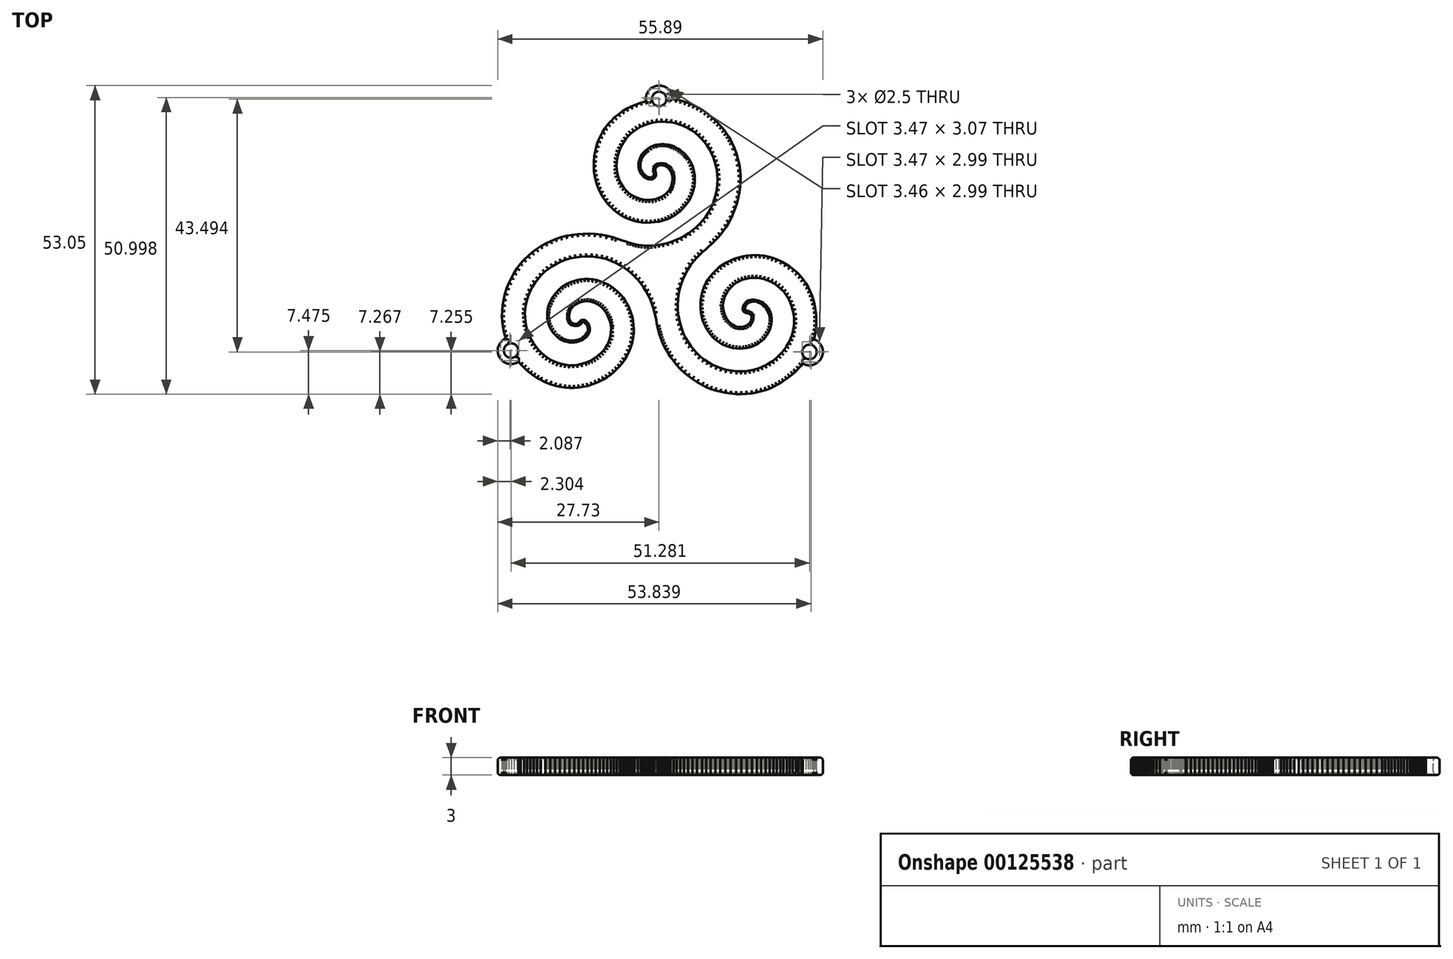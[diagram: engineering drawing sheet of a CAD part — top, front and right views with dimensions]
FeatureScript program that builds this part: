
annotation { "Feature Type Name" : "Feature", "Feature Type Description" : "" }
export const myFeature = defineFeature(function(context is Context, id is Id, definition is map)
    precondition{}
    {
        {
            var Q0;
            Q0=qCreatedBy(makeId("Top.planeOp"),FACE);
            var sketch = newSketch(context, id + "F0", { "sketchPlane" : qUnion([Q0])});
            skLineSegment(sketch, "E0", {"start": v(-0.47, 25.3) * mm, "end": v(-1.4, 25.16) * mm});
            skLineSegment(sketch, "E1", {"start": v(-1.4, 25.16) * mm, "end": v(-2.3, 24.96) * mm});
            skLineSegment(sketch, "E2", {"start": v(-2.3, 24.96) * mm, "end": v(-3.16, 24.7) * mm});
            skLineSegment(sketch, "E3", {"start": v(-3.16, 24.7) * mm, "end": v(-4, 24.4) * mm});
            skLineSegment(sketch, "E4", {"start": v(-4, 24.4) * mm, "end": v(-4.8, 24.06) * mm});
            skLineSegment(sketch, "E5", {"start": v(-4.8, 24.06) * mm, "end": v(-5.57, 23.66) * mm});
            skLineSegment(sketch, "E6", {"start": v(-5.57, 23.66) * mm, "end": v(-6.3, 23.22) * mm});
            skLineSegment(sketch, "E7", {"start": v(-6.3, 23.22) * mm, "end": v(-7, 22.73) * mm});
            skLineSegment(sketch, "E8", {"start": v(-7, 22.73) * mm, "end": v(-7.64, 22.2) * mm});
            skLineSegment(sketch, "E9", {"start": v(-7.64, 22.2) * mm, "end": v(-8.24, 21.61) * mm});
            skLineSegment(sketch, "E10", {"start": v(-8.24, 21.61) * mm, "end": v(-8.8, 20.99) * mm});
            skLineSegment(sketch, "E11", {"start": v(-8.8, 20.99) * mm, "end": v(-9.3, 20.32) * mm});
            skLineSegment(sketch, "E12", {"start": v(-9.3, 20.32) * mm, "end": v(-9.76, 19.61) * mm});
            skLineSegment(sketch, "E13", {"start": v(-9.76, 19.61) * mm, "end": v(-10.15, 18.86) * mm});
            skLineSegment(sketch, "E14", {"start": v(-10.15, 18.86) * mm, "end": v(-10.5, 18.07) * mm});
            skLineSegment(sketch, "E15", {"start": v(-10.5, 18.07) * mm, "end": v(-10.78, 17.24) * mm});
            skLineSegment(sketch, "E16", {"start": v(-10.78, 17.24) * mm, "end": v(-11, 16.37) * mm});
            skLineSegment(sketch, "E17", {"start": v(-11, 16.37) * mm, "end": v(-11.16, 15.47) * mm});
            skLineSegment(sketch, "E18", {"start": v(-11.16, 15.47) * mm, "end": v(-11.24, 14.63) * mm});
            skLineSegment(sketch, "E19", {"start": v(-11.24, 14.63) * mm, "end": v(-11.25, 13.8) * mm});
            skLineSegment(sketch, "E20", {"start": v(-11.25, 13.8) * mm, "end": v(-11.2, 12.98) * mm});
            skLineSegment(sketch, "E21", {"start": v(-11.2, 12.98) * mm, "end": v(-11.08, 12.18) * mm});
            skLineSegment(sketch, "E22", {"start": v(-11.08, 12.18) * mm, "end": v(-10.91, 11.4) * mm});
            skLineSegment(sketch, "E23", {"start": v(-10.91, 11.4) * mm, "end": v(-10.68, 10.64) * mm});
            skLineSegment(sketch, "E24", {"start": v(-10.68, 10.64) * mm, "end": v(-10.4, 9.9) * mm});
            skLineSegment(sketch, "E25", {"start": v(-10.4, 9.9) * mm, "end": v(-10.07, 9.2) * mm});
            skLineSegment(sketch, "E26", {"start": v(-10.07, 9.2) * mm, "end": v(-9.68, 8.53) * mm});
            skLineSegment(sketch, "E27", {"start": v(-9.68, 8.53) * mm, "end": v(-9.25, 7.89) * mm});
            skLineSegment(sketch, "E28", {"start": v(-9.25, 7.89) * mm, "end": v(-8.78, 7.29) * mm});
            skLineSegment(sketch, "E29", {"start": v(-8.78, 7.29) * mm, "end": v(-8.27, 6.73) * mm});
            skLineSegment(sketch, "E30", {"start": v(-8.27, 6.73) * mm, "end": v(-7.71, 6.22) * mm});
            skLineSegment(sketch, "E31", {"start": v(-7.71, 6.22) * mm, "end": v(-7.12, 5.75) * mm});
            skLineSegment(sketch, "E32", {"start": v(-7.12, 5.75) * mm, "end": v(-6.5, 5.33) * mm});
            skLineSegment(sketch, "E33", {"start": v(-6.5, 5.33) * mm, "end": v(-5.85, 4.97) * mm});
            skLineSegment(sketch, "E34", {"start": v(-5.85, 4.97) * mm, "end": v(-5.17, 4.67) * mm});
            skLineSegment(sketch, "E35", {"start": v(-5.17, 4.67) * mm, "end": v(-4.46, 4.42) * mm});
            skLineSegment(sketch, "E36", {"start": v(-4.46, 4.42) * mm, "end": v(-3.73, 4.24) * mm});
            skLineSegment(sketch, "E37", {"start": v(-3.73, 4.24) * mm, "end": v(-2.98, 4.12) * mm});
            skLineSegment(sketch, "E38", {"start": v(-2.98, 4.12) * mm, "end": v(-2.2, 4.08) * mm});
            skLineSegment(sketch, "E39", {"start": v(-2.2, 4.08) * mm, "end": v(-1.44, 4.1) * mm});
            skLineSegment(sketch, "E40", {"start": v(-1.44, 4.1) * mm, "end": v(-0.72, 4.15) * mm});
            skLineSegment(sketch, "E41", {"start": v(-0.72, 4.15) * mm, "end": v(-0.04, 4.26) * mm});
            skLineSegment(sketch, "E42", {"start": v(-0.04, 4.26) * mm, "end": v(0.6, 4.42) * mm});
            skLineSegment(sketch, "E43", {"start": v(0.6, 4.42) * mm, "end": v(1.2, 4.61) * mm});
            skLineSegment(sketch, "E44", {"start": v(1.2, 4.61) * mm, "end": v(1.75, 4.85) * mm});
            skLineSegment(sketch, "E45", {"start": v(1.75, 4.85) * mm, "end": v(2.28, 5.12) * mm});
            skLineSegment(sketch, "E46", {"start": v(2.28, 5.12) * mm, "end": v(2.77, 5.42) * mm});
            skLineSegment(sketch, "E47", {"start": v(2.77, 5.42) * mm, "end": v(3.23, 5.75) * mm});
            skLineSegment(sketch, "E48", {"start": v(3.23, 5.75) * mm, "end": v(3.66, 6.12) * mm});
            skLineSegment(sketch, "E49", {"start": v(3.66, 6.12) * mm, "end": v(4.06, 6.5) * mm});
            skLineSegment(sketch, "E50", {"start": v(4.06, 6.5) * mm, "end": v(4.43, 6.91) * mm});
            skLineSegment(sketch, "E51", {"start": v(4.43, 6.91) * mm, "end": v(4.77, 7.34) * mm});
            skLineSegment(sketch, "E52", {"start": v(4.77, 7.34) * mm, "end": v(5.13, 7.87) * mm});
            skLineSegment(sketch, "E53", {"start": v(5.13, 7.87) * mm, "end": v(5.44, 8.43) * mm});
            skLineSegment(sketch, "E54", {"start": v(5.44, 8.43) * mm, "end": v(5.7, 9.02) * mm});
            skLineSegment(sketch, "E55", {"start": v(5.7, 9.02) * mm, "end": v(5.9, 9.63) * mm});
            skLineSegment(sketch, "E56", {"start": v(5.9, 9.63) * mm, "end": v(6.03, 10.25) * mm});
            skLineSegment(sketch, "E57", {"start": v(6.03, 10.25) * mm, "end": v(6.11, 10.89) * mm});
            skLineSegment(sketch, "E58", {"start": v(6.11, 10.89) * mm, "end": v(6.14, 11.53) * mm});
            skLineSegment(sketch, "E59", {"start": v(6.14, 11.53) * mm, "end": v(6.1, 12.17) * mm});
            skLineSegment(sketch, "E60", {"start": v(6.1, 12.17) * mm, "end": v(6.01, 12.8) * mm});
            skLineSegment(sketch, "E61", {"start": v(6.01, 12.8) * mm, "end": v(5.86, 13.43) * mm});
            skLineSegment(sketch, "E62", {"start": v(5.86, 13.43) * mm, "end": v(5.64, 14.04) * mm});
            skLineSegment(sketch, "E63", {"start": v(5.64, 14.04) * mm, "end": v(5.36, 14.62) * mm});
            skLineSegment(sketch, "E64", {"start": v(5.36, 14.62) * mm, "end": v(5.02, 15.18) * mm});
            skLineSegment(sketch, "E65", {"start": v(5.02, 15.18) * mm, "end": v(4.78, 15.5) * mm});
            skLineSegment(sketch, "E66", {"start": v(4.78, 15.5) * mm, "end": v(4.5, 15.82) * mm});
            skLineSegment(sketch, "E67", {"start": v(4.5, 15.82) * mm, "end": v(4.2, 16.12) * mm});
            skLineSegment(sketch, "E68", {"start": v(4.2, 16.12) * mm, "end": v(3.85, 16.4) * mm});
            skLineSegment(sketch, "E69", {"start": v(3.85, 16.4) * mm, "end": v(3.48, 16.67) * mm});
            skLineSegment(sketch, "E70", {"start": v(3.48, 16.67) * mm, "end": v(3.09, 16.9) * mm});
            skLineSegment(sketch, "E71", {"start": v(3.09, 16.9) * mm, "end": v(2.67, 17.12) * mm});
            skLineSegment(sketch, "E72", {"start": v(2.67, 17.12) * mm, "end": v(2.23, 17.3) * mm});
            skLineSegment(sketch, "E73", {"start": v(2.23, 17.3) * mm, "end": v(1.78, 17.44) * mm});
            skLineSegment(sketch, "E74", {"start": v(1.78, 17.44) * mm, "end": v(1.31, 17.54) * mm});
            skLineSegment(sketch, "E75", {"start": v(1.31, 17.54) * mm, "end": v(0.83, 17.6) * mm});
            skLineSegment(sketch, "E76", {"start": v(0.83, 17.6) * mm, "end": v(0.35, 17.6) * mm});
            skLineSegment(sketch, "E77", {"start": v(0.35, 17.6) * mm, "end": v(-0.14, 17.55) * mm});
            skLineSegment(sketch, "E78", {"start": v(-0.14, 17.55) * mm, "end": v(-0.63, 17.44) * mm});
            skLineSegment(sketch, "E79", {"start": v(-0.63, 17.44) * mm, "end": v(-1.12, 17.26) * mm});
            skLineSegment(sketch, "E80", {"start": v(-1.12, 17.26) * mm, "end": v(-1.6, 17.02) * mm});
            skLineSegment(sketch, "E81", {"start": v(-1.6, 17.02) * mm, "end": v(-2.09, 16.7) * mm});
            skLineSegment(sketch, "E82", {"start": v(-2.09, 16.7) * mm, "end": v(-2.3, 16.53) * mm});
            skLineSegment(sketch, "E83", {"start": v(-2.3, 16.53) * mm, "end": v(-2.53, 16.31) * mm});
            skLineSegment(sketch, "E84", {"start": v(-2.53, 16.31) * mm, "end": v(-2.75, 16.07) * mm});
            skLineSegment(sketch, "E85", {"start": v(-2.75, 16.07) * mm, "end": v(-2.96, 15.79) * mm});
            skLineSegment(sketch, "E86", {"start": v(-2.96, 15.79) * mm, "end": v(-3.15, 15.48) * mm});
            skLineSegment(sketch, "E87", {"start": v(-3.15, 15.48) * mm, "end": v(-3.3, 15.14) * mm});
            skLineSegment(sketch, "E88", {"start": v(-3.3, 15.14) * mm, "end": v(-3.44, 14.79) * mm});
            skLineSegment(sketch, "E89", {"start": v(-3.44, 14.79) * mm, "end": v(-3.52, 14.4) * mm});
            skLineSegment(sketch, "E90", {"start": v(-3.52, 14.4) * mm, "end": v(-3.56, 14.01) * mm});
            skLineSegment(sketch, "E91", {"start": v(-3.56, 14.01) * mm, "end": v(-3.54, 13.6) * mm});
            skLineSegment(sketch, "E92", {"start": v(-3.54, 13.6) * mm, "end": v(-3.45, 13.17) * mm});
            skLineSegment(sketch, "E93", {"start": v(-3.45, 13.17) * mm, "end": v(-3.32, 12.8) * mm});
            skLineSegment(sketch, "E94", {"start": v(-3.32, 12.8) * mm, "end": v(-3.14, 12.5) * mm});
            skLineSegment(sketch, "E95", {"start": v(-3.14, 12.5) * mm, "end": v(-2.93, 12.22) * mm});
            skLineSegment(sketch, "E96", {"start": v(-2.93, 12.22) * mm, "end": v(-2.69, 11.99) * mm});
            skLineSegment(sketch, "E97", {"start": v(-2.69, 11.99) * mm, "end": v(-2.43, 11.8) * mm});
            skLineSegment(sketch, "E98", {"start": v(-2.43, 11.8) * mm, "end": v(-2.16, 11.66) * mm});
            skLineSegment(sketch, "E99", {"start": v(-2.16, 11.66) * mm, "end": v(-1.89, 11.57) * mm});
            skLineSegment(sketch, "E100", {"start": v(-1.89, 11.57) * mm, "end": v(-1.62, 11.52) * mm});
            skLineSegment(sketch, "E101", {"start": v(-1.62, 11.52) * mm, "end": v(-1.36, 11.52) * mm});
            skLineSegment(sketch, "E102", {"start": v(-1.36, 11.52) * mm, "end": v(-1.13, 11.56) * mm});
            skLineSegment(sketch, "E103", {"start": v(-1.13, 11.56) * mm, "end": v(-0.92, 11.65) * mm});
            skLineSegment(sketch, "E104", {"start": v(-0.92, 11.65) * mm, "end": v(-0.74, 11.79) * mm});
            skLineSegment(sketch, "E105", {"start": v(-0.74, 11.79) * mm, "end": v(-0.61, 11.97) * mm});
            skLineSegment(sketch, "E106", {"start": v(-0.61, 11.97) * mm, "end": v(-0.53, 12.2) * mm});
            skLineSegment(sketch, "E107", {"start": v(-0.53, 12.2) * mm, "end": v(-0.52, 12.33) * mm});
            skLineSegment(sketch, "E108", {"start": v(-0.52, 12.33) * mm, "end": v(-0.54, 12.48) * mm});
            skLineSegment(sketch, "E109", {"start": v(-0.54, 12.48) * mm, "end": v(-0.57, 12.62) * mm});
            skLineSegment(sketch, "E110", {"start": v(-0.57, 12.62) * mm, "end": v(-0.6, 12.78) * mm});
            skLineSegment(sketch, "E111", {"start": v(-0.6, 12.78) * mm, "end": v(-0.64, 12.94) * mm});
            skLineSegment(sketch, "E112", {"start": v(-0.64, 12.94) * mm, "end": v(-0.67, 13.1) * mm});
            skLineSegment(sketch, "E113", {"start": v(-0.67, 13.1) * mm, "end": v(-0.67, 13.25) * mm});
            skLineSegment(sketch, "E114", {"start": v(-0.67, 13.25) * mm, "end": v(-0.64, 13.4) * mm});
            skLineSegment(sketch, "E115", {"start": v(-0.64, 13.4) * mm, "end": v(-0.58, 13.55) * mm});
            skLineSegment(sketch, "E116", {"start": v(-0.58, 13.55) * mm, "end": v(-0.47, 13.68) * mm});
            skLineSegment(sketch, "E117", {"start": v(-0.47, 13.68) * mm, "end": v(-0.31, 13.8) * mm});
            skLineSegment(sketch, "E118", {"start": v(-0.31, 13.8) * mm, "end": v(-0.08, 13.9) * mm});
            skLineSegment(sketch, "E119", {"start": v(-0.08, 13.9) * mm, "end": v(0.21, 13.97) * mm});
            skLineSegment(sketch, "E120", {"start": v(0.21, 13.97) * mm, "end": v(0.5, 13.97) * mm});
            skLineSegment(sketch, "E121", {"start": v(0.5, 13.97) * mm, "end": v(0.77, 13.92) * mm});
            skLineSegment(sketch, "E122", {"start": v(0.77, 13.92) * mm, "end": v(1.02, 13.83) * mm});
            skLineSegment(sketch, "E123", {"start": v(1.02, 13.83) * mm, "end": v(1.25, 13.7) * mm});
            skLineSegment(sketch, "E124", {"start": v(1.25, 13.7) * mm, "end": v(1.45, 13.56) * mm});
            skLineSegment(sketch, "E125", {"start": v(1.45, 13.56) * mm, "end": v(1.62, 13.4) * mm});
            skLineSegment(sketch, "E126", {"start": v(1.62, 13.4) * mm, "end": v(1.76, 13.26) * mm});
            skLineSegment(sketch, "E127", {"start": v(1.76, 13.26) * mm, "end": v(1.97, 12.96) * mm});
            skLineSegment(sketch, "E128", {"start": v(1.97, 12.96) * mm, "end": v(2.12, 12.63) * mm});
            skLineSegment(sketch, "E129", {"start": v(2.12, 12.63) * mm, "end": v(2.23, 12.27) * mm});
            skLineSegment(sketch, "E130", {"start": v(2.23, 12.27) * mm, "end": v(2.29, 11.9) * mm});
            skLineSegment(sketch, "E131", {"start": v(2.29, 11.9) * mm, "end": v(2.3, 11.53) * mm});
            skLineSegment(sketch, "E132", {"start": v(2.3, 11.53) * mm, "end": v(2.27, 11.16) * mm});
            skLineSegment(sketch, "E133", {"start": v(2.27, 11.16) * mm, "end": v(2.2, 10.8) * mm});
            skLineSegment(sketch, "E134", {"start": v(2.2, 10.8) * mm, "end": v(2.1, 10.44) * mm});
            skLineSegment(sketch, "E135", {"start": v(2.1, 10.44) * mm, "end": v(1.96, 10.1) * mm});
            skLineSegment(sketch, "E136", {"start": v(1.96, 10.1) * mm, "end": v(1.8, 9.8) * mm});
            skLineSegment(sketch, "E137", {"start": v(1.8, 9.8) * mm, "end": v(1.6, 9.53) * mm});
            skLineSegment(sketch, "E138", {"start": v(1.6, 9.53) * mm, "end": v(1.21, 9.12) * mm});
            skLineSegment(sketch, "E139", {"start": v(1.21, 9.12) * mm, "end": v(0.8, 8.78) * mm});
            skLineSegment(sketch, "E140", {"start": v(0.8, 8.78) * mm, "end": v(0.34, 8.5) * mm});
            skLineSegment(sketch, "E141", {"start": v(0.34, 8.5) * mm, "end": v(-0.14, 8.28) * mm});
            skLineSegment(sketch, "E142", {"start": v(-0.14, 8.28) * mm, "end": v(-0.64, 8.13) * mm});
            skLineSegment(sketch, "E143", {"start": v(-0.64, 8.13) * mm, "end": v(-1.16, 8.03) * mm});
            skLineSegment(sketch, "E144", {"start": v(-1.16, 8.03) * mm, "end": v(-1.69, 7.98) * mm});
            skLineSegment(sketch, "E145", {"start": v(-1.69, 7.98) * mm, "end": v(-2.22, 8) * mm});
            skLineSegment(sketch, "E146", {"start": v(-2.22, 8) * mm, "end": v(-2.75, 8.06) * mm});
            skLineSegment(sketch, "E147", {"start": v(-2.75, 8.06) * mm, "end": v(-3.27, 8.18) * mm});
            skLineSegment(sketch, "E148", {"start": v(-3.27, 8.18) * mm, "end": v(-3.78, 8.35) * mm});
            skLineSegment(sketch, "E149", {"start": v(-3.78, 8.35) * mm, "end": v(-4.27, 8.57) * mm});
            skLineSegment(sketch, "E150", {"start": v(-4.27, 8.57) * mm, "end": v(-4.73, 8.84) * mm});
            skLineSegment(sketch, "E151", {"start": v(-4.73, 8.84) * mm, "end": v(-5.17, 9.16) * mm});
            skLineSegment(sketch, "E152", {"start": v(-5.17, 9.16) * mm, "end": v(-5.57, 9.52) * mm});
            skLineSegment(sketch, "E153", {"start": v(-5.57, 9.52) * mm, "end": v(-5.99, 9.98) * mm});
            skLineSegment(sketch, "E154", {"start": v(-5.99, 9.98) * mm, "end": v(-6.34, 10.47) * mm});
            skLineSegment(sketch, "E155", {"start": v(-6.34, 10.47) * mm, "end": v(-6.64, 10.99) * mm});
            skLineSegment(sketch, "E156", {"start": v(-6.64, 10.99) * mm, "end": v(-6.89, 11.53) * mm});
            skLineSegment(sketch, "E157", {"start": v(-6.89, 11.53) * mm, "end": v(-7.08, 12.1) * mm});
            skLineSegment(sketch, "E158", {"start": v(-7.08, 12.1) * mm, "end": v(-7.21, 12.68) * mm});
            skLineSegment(sketch, "E159", {"start": v(-7.21, 12.68) * mm, "end": v(-7.3, 13.27) * mm});
            skLineSegment(sketch, "E160", {"start": v(-7.3, 13.27) * mm, "end": v(-7.32, 13.87) * mm});
            skLineSegment(sketch, "E161", {"start": v(-7.32, 13.87) * mm, "end": v(-7.3, 14.47) * mm});
            skLineSegment(sketch, "E162", {"start": v(-7.3, 14.47) * mm, "end": v(-7.22, 15.07) * mm});
            skLineSegment(sketch, "E163", {"start": v(-7.22, 15.07) * mm, "end": v(-7.1, 15.67) * mm});
            skLineSegment(sketch, "E164", {"start": v(-7.1, 15.67) * mm, "end": v(-6.92, 16.26) * mm});
            skLineSegment(sketch, "E165", {"start": v(-6.92, 16.26) * mm, "end": v(-6.7, 16.84) * mm});
            skLineSegment(sketch, "E166", {"start": v(-6.7, 16.84) * mm, "end": v(-6.42, 17.4) * mm});
            skLineSegment(sketch, "E167", {"start": v(-6.42, 17.4) * mm, "end": v(-6.1, 17.95) * mm});
            skLineSegment(sketch, "E168", {"start": v(-6.1, 17.95) * mm, "end": v(-5.73, 18.47) * mm});
            skLineSegment(sketch, "E169", {"start": v(-5.73, 18.47) * mm, "end": v(-5.32, 18.96) * mm});
            skLineSegment(sketch, "E170", {"start": v(-5.32, 18.96) * mm, "end": v(-4.85, 19.41) * mm});
            skLineSegment(sketch, "E171", {"start": v(-4.85, 19.41) * mm, "end": v(-4.35, 19.84) * mm});
            skLineSegment(sketch, "E172", {"start": v(-4.35, 19.84) * mm, "end": v(-3.8, 20.22) * mm});
            skLineSegment(sketch, "E173", {"start": v(-3.8, 20.22) * mm, "end": v(-3.2, 20.55) * mm});
            skLineSegment(sketch, "E174", {"start": v(-3.2, 20.55) * mm, "end": v(-2.57, 20.84) * mm});
            skLineSegment(sketch, "E175", {"start": v(-2.57, 20.84) * mm, "end": v(-1.89, 21.08) * mm});
            skLineSegment(sketch, "E176", {"start": v(-1.89, 21.08) * mm, "end": v(-1.17, 21.26) * mm});
            skLineSegment(sketch, "E177", {"start": v(-1.17, 21.26) * mm, "end": v(-0.4, 21.38) * mm});
            skLineSegment(sketch, "E178", {"start": v(-0.4, 21.38) * mm, "end": v(0.42, 21.43) * mm});
            skLineSegment(sketch, "E179", {"start": v(0.42, 21.43) * mm, "end": v(1.23, 21.42) * mm});
            skLineSegment(sketch, "E180", {"start": v(1.23, 21.42) * mm, "end": v(2.02, 21.33) * mm});
            skLineSegment(sketch, "E181", {"start": v(2.02, 21.33) * mm, "end": v(2.78, 21.18) * mm});
            skLineSegment(sketch, "E182", {"start": v(2.78, 21.18) * mm, "end": v(3.52, 20.97) * mm});
            skLineSegment(sketch, "E183", {"start": v(3.52, 20.97) * mm, "end": v(4.23, 20.7) * mm});
            skLineSegment(sketch, "E184", {"start": v(4.23, 20.7) * mm, "end": v(4.9, 20.36) * mm});
            skLineSegment(sketch, "E185", {"start": v(4.9, 20.36) * mm, "end": v(5.55, 19.98) * mm});
            skLineSegment(sketch, "E186", {"start": v(5.55, 19.98) * mm, "end": v(6.16, 19.54) * mm});
            skLineSegment(sketch, "E187", {"start": v(6.16, 19.54) * mm, "end": v(6.74, 19.06) * mm});
            skLineSegment(sketch, "E188", {"start": v(6.74, 19.06) * mm, "end": v(7.28, 18.53) * mm});
            skLineSegment(sketch, "E189", {"start": v(7.28, 18.53) * mm, "end": v(7.77, 17.97) * mm});
            skLineSegment(sketch, "E190", {"start": v(7.77, 17.97) * mm, "end": v(8.22, 17.36) * mm});
            skLineSegment(sketch, "E191", {"start": v(8.22, 17.36) * mm, "end": v(8.63, 16.72) * mm});
            skLineSegment(sketch, "E192", {"start": v(8.63, 16.72) * mm, "end": v(8.99, 16.05) * mm});
            skLineSegment(sketch, "E193", {"start": v(8.99, 16.05) * mm, "end": v(9.3, 15.35) * mm});
            skLineSegment(sketch, "E194", {"start": v(9.3, 15.35) * mm, "end": v(9.56, 14.63) * mm});
            skLineSegment(sketch, "E195", {"start": v(9.56, 14.63) * mm, "end": v(9.76, 13.88) * mm});
            skLineSegment(sketch, "E196", {"start": v(9.76, 13.88) * mm, "end": v(9.91, 13.12) * mm});
            skLineSegment(sketch, "E197", {"start": v(9.91, 13.12) * mm, "end": v(10, 12.34) * mm});
            skLineSegment(sketch, "E198", {"start": v(10, 12.34) * mm, "end": v(10.04, 11.54) * mm});
            skLineSegment(sketch, "E199", {"start": v(10.04, 11.54) * mm, "end": v(10, 10.64) * mm});
            skLineSegment(sketch, "E200", {"start": v(10, 10.64) * mm, "end": v(9.9, 9.77) * mm});
            skLineSegment(sketch, "E201", {"start": v(9.9, 9.77) * mm, "end": v(9.73, 8.92) * mm});
            skLineSegment(sketch, "E202", {"start": v(9.73, 8.92) * mm, "end": v(9.5, 8.1) * mm});
            skLineSegment(sketch, "E203", {"start": v(9.5, 8.1) * mm, "end": v(9.2, 7.32) * mm});
            skLineSegment(sketch, "E204", {"start": v(9.2, 7.32) * mm, "end": v(8.86, 6.56) * mm});
            skLineSegment(sketch, "E205", {"start": v(8.86, 6.56) * mm, "end": v(8.45, 5.84) * mm});
            skLineSegment(sketch, "E206", {"start": v(8.45, 5.84) * mm, "end": v(8, 5.15) * mm});
            skLineSegment(sketch, "E207", {"start": v(8, 5.15) * mm, "end": v(7.5, 4.5) * mm});
            skLineSegment(sketch, "E208", {"start": v(7.5, 4.5) * mm, "end": v(6.95, 3.88) * mm});
            skLineSegment(sketch, "E209", {"start": v(6.95, 3.88) * mm, "end": v(6.37, 3.31) * mm});
            skLineSegment(sketch, "E210", {"start": v(6.37, 3.31) * mm, "end": v(5.75, 2.78) * mm});
            skLineSegment(sketch, "E211", {"start": v(5.75, 2.78) * mm, "end": v(5.09, 2.3) * mm});
            skLineSegment(sketch, "E212", {"start": v(5.09, 2.3) * mm, "end": v(4.4, 1.85) * mm});
            skLineSegment(sketch, "E213", {"start": v(4.4, 1.85) * mm, "end": v(3.69, 1.46) * mm});
            skLineSegment(sketch, "E214", {"start": v(3.69, 1.46) * mm, "end": v(2.95, 1.12) * mm});
            skLineSegment(sketch, "E215", {"start": v(2.95, 1.12) * mm, "end": v(2.19, 0.82) * mm});
            skLineSegment(sketch, "E216", {"start": v(2.19, 0.82) * mm, "end": v(1.4, 0.58) * mm});
            skLineSegment(sketch, "E217", {"start": v(1.4, 0.58) * mm, "end": v(0.61, 0.4) * mm});
            skLineSegment(sketch, "E218", {"start": v(0.61, 0.4) * mm, "end": v(-0.1, 0.27) * mm});
            skLineSegment(sketch, "E219", {"start": v(-0.1, 0.27) * mm, "end": v(-0.75, 0.19) * mm});
            skLineSegment(sketch, "E220", {"start": v(-0.75, 0.19) * mm, "end": v(-1.36, 0.14) * mm});
            skLineSegment(sketch, "E221", {"start": v(-1.36, 0.14) * mm, "end": v(-1.93, 0.12) * mm});
            skLineSegment(sketch, "E222", {"start": v(-1.93, 0.12) * mm, "end": v(-2.46, 0.14) * mm});
            skLineSegment(sketch, "E223", {"start": v(-2.46, 0.14) * mm, "end": v(-2.98, 0.18) * mm});
            skLineSegment(sketch, "E224", {"start": v(-2.98, 0.18) * mm, "end": v(-3.47, 0.25) * mm});
            skLineSegment(sketch, "E225", {"start": v(-3.47, 0.25) * mm, "end": v(-3.94, 0.34) * mm});
            skLineSegment(sketch, "E226", {"start": v(-3.94, 0.34) * mm, "end": v(-4.41, 0.45) * mm});
            skLineSegment(sketch, "E227", {"start": v(-4.41, 0.45) * mm, "end": v(-4.88, 0.58) * mm});
            skLineSegment(sketch, "E228", {"start": v(-4.88, 0.58) * mm, "end": v(-5.35, 0.72) * mm});
            skLineSegment(sketch, "E229", {"start": v(-5.35, 0.72) * mm, "end": v(-5.83, 0.87) * mm});
            skLineSegment(sketch, "E230", {"start": v(-5.83, 0.87) * mm, "end": v(-6.33, 1.03) * mm});
            skLineSegment(sketch, "E231", {"start": v(-6.33, 1.03) * mm, "end": v(-6.85, 1.2) * mm});
            skLineSegment(sketch, "E232", {"start": v(-6.85, 1.2) * mm, "end": v(-7.4, 1.38) * mm});
            skLineSegment(sketch, "E233", {"start": v(-7.4, 1.38) * mm, "end": v(-7.99, 1.55) * mm});
            skLineSegment(sketch, "E234", {"start": v(-7.99, 1.55) * mm, "end": v(-9, 1.8) * mm});
            skLineSegment(sketch, "E235", {"start": v(-9, 1.8) * mm, "end": v(-10.02, 2) * mm});
            skLineSegment(sketch, "E236", {"start": v(-10.02, 2) * mm, "end": v(-11.03, 2.12) * mm});
            skLineSegment(sketch, "E237", {"start": v(-11.03, 2.12) * mm, "end": v(-12.04, 2.18) * mm});
            skLineSegment(sketch, "E238", {"start": v(-12.04, 2.18) * mm, "end": v(-13.03, 2.18) * mm});
            skLineSegment(sketch, "E239", {"start": v(-13.03, 2.18) * mm, "end": v(-14.01, 2.12) * mm});
            skLineSegment(sketch, "E240", {"start": v(-14.01, 2.12) * mm, "end": v(-14.98, 2) * mm});
            skLineSegment(sketch, "E241", {"start": v(-14.98, 2) * mm, "end": v(-15.93, 1.8) * mm});
            skLineSegment(sketch, "E242", {"start": v(-15.93, 1.8) * mm, "end": v(-16.86, 1.56) * mm});
            skLineSegment(sketch, "E243", {"start": v(-16.86, 1.56) * mm, "end": v(-17.76, 1.27) * mm});
            skLineSegment(sketch, "E244", {"start": v(-17.76, 1.27) * mm, "end": v(-18.64, 0.91) * mm});
            skLineSegment(sketch, "E245", {"start": v(-18.64, 0.91) * mm, "end": v(-19.49, 0.5) * mm});
            skLineSegment(sketch, "E246", {"start": v(-19.49, 0.5) * mm, "end": v(-20.3, 0.04) * mm});
            skLineSegment(sketch, "E247", {"start": v(-20.3, 0.04) * mm, "end": v(-21.1, -0.47) * mm});
            skLineSegment(sketch, "E248", {"start": v(-21.1, -0.47) * mm, "end": v(-21.84, -1.04) * mm});
            skLineSegment(sketch, "E249", {"start": v(-21.84, -1.04) * mm, "end": v(-22.55, -1.65) * mm});
            skLineSegment(sketch, "E250", {"start": v(-22.55, -1.65) * mm, "end": v(-23.22, -2.31) * mm});
            skLineSegment(sketch, "E251", {"start": v(-23.22, -2.31) * mm, "end": v(-23.84, -3.02) * mm});
            skLineSegment(sketch, "E252", {"start": v(-23.84, -3.02) * mm, "end": v(-24.41, -3.77) * mm});
            skLineSegment(sketch, "E253", {"start": v(-24.41, -3.77) * mm, "end": v(-24.94, -4.57) * mm});
            skLineSegment(sketch, "E254", {"start": v(-24.94, -4.57) * mm, "end": v(-25.41, -5.4) * mm});
            skLineSegment(sketch, "E255", {"start": v(-25.41, -5.4) * mm, "end": v(-25.83, -6.29) * mm});
            skLineSegment(sketch, "E256", {"start": v(-25.83, -6.29) * mm, "end": v(-26.2, -7.2) * mm});
            skLineSegment(sketch, "E257", {"start": v(-26.2, -7.2) * mm, "end": v(-26.5, -8.17) * mm});
            skLineSegment(sketch, "E258", {"start": v(-26.5, -8.17) * mm, "end": v(-26.74, -9.17) * mm});
            skLineSegment(sketch, "E259", {"start": v(-26.74, -9.17) * mm, "end": v(-26.9, -10.14) * mm});
            skLineSegment(sketch, "E260", {"start": v(-26.9, -10.14) * mm, "end": v(-26.99, -11.1) * mm});
            skLineSegment(sketch, "E261", {"start": v(-26.99, -11.1) * mm, "end": v(-27.01, -12.02) * mm});
            skLineSegment(sketch, "E262", {"start": v(-27.01, -12.02) * mm, "end": v(-26.97, -12.92) * mm});
            skLineSegment(sketch, "E263", {"start": v(-26.97, -12.92) * mm, "end": v(-26.87, -13.8) * mm});
            skLineSegment(sketch, "E264", {"start": v(-26.87, -13.8) * mm, "end": v(-26.7, -14.64) * mm});
            skLineSegment(sketch, "E265", {"start": v(-26.7, -14.64) * mm, "end": v(-26.49, -15.46) * mm});
            skLineSegment(sketch, "E266", {"start": v(-26.49, -15.46) * mm, "end": v(-26.22, -16.25) * mm});
            skLineSegment(sketch, "E267", {"start": v(-26.22, -16.25) * mm, "end": v(-25.91, -17) * mm});
            skLineSegment(sketch, "E268", {"start": v(-25.91, -17) * mm, "end": v(-25.55, -17.73) * mm});
            skLineSegment(sketch, "E269", {"start": v(-25.55, -17.73) * mm, "end": v(-25.16, -18.42) * mm});
            skLineSegment(sketch, "E270", {"start": v(-25.16, -18.42) * mm, "end": v(-24.72, -19.08) * mm});
            skLineSegment(sketch, "E271", {"start": v(-24.72, -19.08) * mm, "end": v(-24.26, -19.7) * mm});
            skLineSegment(sketch, "E272", {"start": v(-24.26, -19.7) * mm, "end": v(-23.76, -20.28) * mm});
            skLineSegment(sketch, "E273", {"start": v(-23.76, -20.28) * mm, "end": v(-23.24, -20.83) * mm});
            skLineSegment(sketch, "E274", {"start": v(-23.24, -20.83) * mm, "end": v(-22.7, -21.33) * mm});
            skLineSegment(sketch, "E275", {"start": v(-22.7, -21.33) * mm, "end": v(-22.14, -21.8) * mm});
            skLineSegment(sketch, "E276", {"start": v(-22.14, -21.8) * mm, "end": v(-21.57, -22.22) * mm});
            skLineSegment(sketch, "E277", {"start": v(-21.57, -22.22) * mm, "end": v(-20.98, -22.6) * mm});
            skLineSegment(sketch, "E278", {"start": v(-20.98, -22.6) * mm, "end": v(-20.38, -22.94) * mm});
            skLineSegment(sketch, "E279", {"start": v(-20.38, -22.94) * mm, "end": v(-19.55, -23.35) * mm});
            skLineSegment(sketch, "E280", {"start": v(-19.55, -23.35) * mm, "end": v(-18.7, -23.68) * mm});
            skLineSegment(sketch, "E281", {"start": v(-18.7, -23.68) * mm, "end": v(-17.87, -23.94) * mm});
            skLineSegment(sketch, "E282", {"start": v(-17.87, -23.94) * mm, "end": v(-17.05, -24.13) * mm});
            skLineSegment(sketch, "E283", {"start": v(-17.05, -24.13) * mm, "end": v(-16.22, -24.25) * mm});
            skLineSegment(sketch, "E284", {"start": v(-16.22, -24.25) * mm, "end": v(-15.41, -24.32) * mm});
            skLineSegment(sketch, "E285", {"start": v(-15.41, -24.32) * mm, "end": v(-14.61, -24.32) * mm});
            skLineSegment(sketch, "E286", {"start": v(-14.61, -24.32) * mm, "end": v(-13.83, -24.26) * mm});
            skLineSegment(sketch, "E287", {"start": v(-13.83, -24.26) * mm, "end": v(-13.06, -24.15) * mm});
            skLineSegment(sketch, "E288", {"start": v(-13.06, -24.15) * mm, "end": v(-12.31, -23.98) * mm});
            skLineSegment(sketch, "E289", {"start": v(-12.31, -23.98) * mm, "end": v(-11.58, -23.77) * mm});
            skLineSegment(sketch, "E290", {"start": v(-11.58, -23.77) * mm, "end": v(-10.88, -23.5) * mm});
            skLineSegment(sketch, "E291", {"start": v(-10.88, -23.5) * mm, "end": v(-10.2, -23.2) * mm});
            skLineSegment(sketch, "E292", {"start": v(-10.2, -23.2) * mm, "end": v(-9.54, -22.86) * mm});
            skLineSegment(sketch, "E293", {"start": v(-9.54, -22.86) * mm, "end": v(-8.92, -22.47) * mm});
            skLineSegment(sketch, "E294", {"start": v(-8.92, -22.47) * mm, "end": v(-8.33, -22.05) * mm});
            skLineSegment(sketch, "E295", {"start": v(-8.33, -22.05) * mm, "end": v(-7.77, -21.6) * mm});
            skLineSegment(sketch, "E296", {"start": v(-7.77, -21.6) * mm, "end": v(-7.25, -21.1) * mm});
            skLineSegment(sketch, "E297", {"start": v(-7.25, -21.1) * mm, "end": v(-6.77, -20.59) * mm});
            skLineSegment(sketch, "E298", {"start": v(-6.77, -20.59) * mm, "end": v(-6.33, -20.05) * mm});
            skLineSegment(sketch, "E299", {"start": v(-6.33, -20.05) * mm, "end": v(-5.94, -19.48) * mm});
            skLineSegment(sketch, "E300", {"start": v(-5.94, -19.48) * mm, "end": v(-5.5, -18.75) * mm});
            skLineSegment(sketch, "E301", {"start": v(-5.5, -18.75) * mm, "end": v(-5.14, -18.01) * mm});
            skLineSegment(sketch, "E302", {"start": v(-5.14, -18.01) * mm, "end": v(-4.85, -17.26) * mm});
            skLineSegment(sketch, "E303", {"start": v(-4.85, -17.26) * mm, "end": v(-4.63, -16.5) * mm});
            skLineSegment(sketch, "E304", {"start": v(-4.63, -16.5) * mm, "end": v(-4.48, -15.75) * mm});
            skLineSegment(sketch, "E305", {"start": v(-4.48, -15.75) * mm, "end": v(-4.4, -15) * mm});
            skLineSegment(sketch, "E306", {"start": v(-4.4, -15) * mm, "end": v(-4.37, -14.24) * mm});
            skLineSegment(sketch, "E307", {"start": v(-4.37, -14.24) * mm, "end": v(-4.4, -13.5) * mm});
            skLineSegment(sketch, "E308", {"start": v(-4.4, -13.5) * mm, "end": v(-4.5, -12.78) * mm});
            skLineSegment(sketch, "E309", {"start": v(-4.5, -12.78) * mm, "end": v(-4.65, -12.06) * mm});
            skLineSegment(sketch, "E310", {"start": v(-4.65, -12.06) * mm, "end": v(-4.85, -11.37) * mm});
            skLineSegment(sketch, "E311", {"start": v(-4.85, -11.37) * mm, "end": v(-5.1, -10.7) * mm});
            skLineSegment(sketch, "E312", {"start": v(-5.1, -10.7) * mm, "end": v(-5.4, -10.06) * mm});
            skLineSegment(sketch, "E313", {"start": v(-5.4, -10.06) * mm, "end": v(-5.76, -9.44) * mm});
            skLineSegment(sketch, "E314", {"start": v(-5.76, -9.44) * mm, "end": v(-6.16, -8.86) * mm});
            skLineSegment(sketch, "E315", {"start": v(-6.16, -8.86) * mm, "end": v(-6.6, -8.32) * mm});
            skLineSegment(sketch, "E316", {"start": v(-6.6, -8.32) * mm, "end": v(-7.07, -7.81) * mm});
            skLineSegment(sketch, "E317", {"start": v(-7.07, -7.81) * mm, "end": v(-7.6, -7.35) * mm});
            skLineSegment(sketch, "E318", {"start": v(-7.6, -7.35) * mm, "end": v(-8.15, -6.94) * mm});
            skLineSegment(sketch, "E319", {"start": v(-8.15, -6.94) * mm, "end": v(-8.73, -6.58) * mm});
            skLineSegment(sketch, "E320", {"start": v(-8.73, -6.58) * mm, "end": v(-9.36, -6.27) * mm});
            skLineSegment(sketch, "E321", {"start": v(-9.36, -6.27) * mm, "end": v(-10, -6.02) * mm});
            skLineSegment(sketch, "E322", {"start": v(-10, -6.02) * mm, "end": v(-10.73, -5.82) * mm});
            skLineSegment(sketch, "E323", {"start": v(-10.73, -5.82) * mm, "end": v(-11.44, -5.68) * mm});
            skLineSegment(sketch, "E324", {"start": v(-11.44, -5.68) * mm, "end": v(-12.14, -5.61) * mm});
            skLineSegment(sketch, "E325", {"start": v(-12.14, -5.61) * mm, "end": v(-12.8, -5.61) * mm});
            skLineSegment(sketch, "E326", {"start": v(-12.8, -5.61) * mm, "end": v(-13.46, -5.67) * mm});
            skLineSegment(sketch, "E327", {"start": v(-13.46, -5.67) * mm, "end": v(-14.08, -5.78) * mm});
            skLineSegment(sketch, "E328", {"start": v(-14.08, -5.78) * mm, "end": v(-14.68, -5.95) * mm});
            skLineSegment(sketch, "E329", {"start": v(-14.68, -5.95) * mm, "end": v(-15.26, -6.16) * mm});
            skLineSegment(sketch, "E330", {"start": v(-15.26, -6.16) * mm, "end": v(-15.8, -6.43) * mm});
            skLineSegment(sketch, "E331", {"start": v(-15.8, -6.43) * mm, "end": v(-16.3, -6.73) * mm});
            skLineSegment(sketch, "E332", {"start": v(-16.3, -6.73) * mm, "end": v(-16.79, -7.07) * mm});
            skLineSegment(sketch, "E333", {"start": v(-16.79, -7.07) * mm, "end": v(-17.23, -7.45) * mm});
            skLineSegment(sketch, "E334", {"start": v(-17.23, -7.45) * mm, "end": v(-17.63, -7.86) * mm});
            skLineSegment(sketch, "E335", {"start": v(-17.63, -7.86) * mm, "end": v(-18, -8.3) * mm});
            skLineSegment(sketch, "E336", {"start": v(-18, -8.3) * mm, "end": v(-18.31, -8.76) * mm});
            skLineSegment(sketch, "E337", {"start": v(-18.31, -8.76) * mm, "end": v(-18.59, -9.24) * mm});
            skLineSegment(sketch, "E338", {"start": v(-18.59, -9.24) * mm, "end": v(-18.82, -9.74) * mm});
            skLineSegment(sketch, "E339", {"start": v(-18.82, -9.74) * mm, "end": v(-19, -10.25) * mm});
            skLineSegment(sketch, "E340", {"start": v(-19, -10.25) * mm, "end": v(-19.14, -10.78) * mm});
            skLineSegment(sketch, "E341", {"start": v(-19.14, -10.78) * mm, "end": v(-19.22, -11.3) * mm});
            skLineSegment(sketch, "E342", {"start": v(-19.22, -11.3) * mm, "end": v(-19.25, -11.84) * mm});
            skLineSegment(sketch, "E343", {"start": v(-19.25, -11.84) * mm, "end": v(-19.23, -12.37) * mm});
            skLineSegment(sketch, "E344", {"start": v(-19.23, -12.37) * mm, "end": v(-19.14, -12.9) * mm});
            skLineSegment(sketch, "E345", {"start": v(-19.14, -12.9) * mm, "end": v(-19, -13.41) * mm});
            skLineSegment(sketch, "E346", {"start": v(-19, -13.41) * mm, "end": v(-18.8, -13.92) * mm});
            skLineSegment(sketch, "E347", {"start": v(-18.8, -13.92) * mm, "end": v(-18.53, -14.41) * mm});
            skLineSegment(sketch, "E348", {"start": v(-18.53, -14.41) * mm, "end": v(-18.2, -14.88) * mm});
            skLineSegment(sketch, "E349", {"start": v(-18.2, -14.88) * mm, "end": v(-17.8, -15.33) * mm});
            skLineSegment(sketch, "E350", {"start": v(-17.8, -15.33) * mm, "end": v(-17.43, -15.66) * mm});
            skLineSegment(sketch, "E351", {"start": v(-17.43, -15.66) * mm, "end": v(-17.05, -15.93) * mm});
            skLineSegment(sketch, "E352", {"start": v(-17.05, -15.93) * mm, "end": v(-16.65, -16.14) * mm});
            skLineSegment(sketch, "E353", {"start": v(-16.65, -16.14) * mm, "end": v(-16.24, -16.3) * mm});
            skLineSegment(sketch, "E354", {"start": v(-16.24, -16.3) * mm, "end": v(-15.82, -16.42) * mm});
            skLineSegment(sketch, "E355", {"start": v(-15.82, -16.42) * mm, "end": v(-15.4, -16.5) * mm});
            skLineSegment(sketch, "E356", {"start": v(-15.4, -16.5) * mm, "end": v(-15, -16.51) * mm});
            skLineSegment(sketch, "E357", {"start": v(-15, -16.51) * mm, "end": v(-14.58, -16.5) * mm});
            skLineSegment(sketch, "E358", {"start": v(-14.58, -16.5) * mm, "end": v(-14.19, -16.44) * mm});
            skLineSegment(sketch, "E359", {"start": v(-14.19, -16.44) * mm, "end": v(-13.8, -16.34) * mm});
            skLineSegment(sketch, "E360", {"start": v(-13.8, -16.34) * mm, "end": v(-13.45, -16.21) * mm});
            skLineSegment(sketch, "E361", {"start": v(-13.45, -16.21) * mm, "end": v(-13.12, -16.05) * mm});
            skLineSegment(sketch, "E362", {"start": v(-13.12, -16.05) * mm, "end": v(-12.82, -15.85) * mm});
            skLineSegment(sketch, "E363", {"start": v(-12.82, -15.85) * mm, "end": v(-12.55, -15.62) * mm});
            skLineSegment(sketch, "E364", {"start": v(-12.55, -15.62) * mm, "end": v(-12.33, -15.37) * mm});
            skLineSegment(sketch, "E365", {"start": v(-12.33, -15.37) * mm, "end": v(-12.15, -15.1) * mm});
            skLineSegment(sketch, "E366", {"start": v(-12.15, -15.1) * mm, "end": v(-12.02, -14.8) * mm});
            skLineSegment(sketch, "E367", {"start": v(-12.02, -14.8) * mm, "end": v(-11.95, -14.47) * mm});
            skLineSegment(sketch, "E368", {"start": v(-11.95, -14.47) * mm, "end": v(-11.93, -14.13) * mm});
            skLineSegment(sketch, "E369", {"start": v(-11.93, -14.13) * mm, "end": v(-11.98, -13.77) * mm});
            skLineSegment(sketch, "E370", {"start": v(-11.98, -13.77) * mm, "end": v(-12.1, -13.4) * mm});
            skLineSegment(sketch, "E371", {"start": v(-12.1, -13.4) * mm, "end": v(-12.17, -13.24) * mm});
            skLineSegment(sketch, "E372", {"start": v(-12.17, -13.24) * mm, "end": v(-12.28, -13.08) * mm});
            skLineSegment(sketch, "E373", {"start": v(-12.28, -13.08) * mm, "end": v(-12.4, -12.94) * mm});
            skLineSegment(sketch, "E374", {"start": v(-12.4, -12.94) * mm, "end": v(-12.55, -12.8) * mm});
            skLineSegment(sketch, "E375", {"start": v(-12.55, -12.8) * mm, "end": v(-12.71, -12.7) * mm});
            skLineSegment(sketch, "E376", {"start": v(-12.71, -12.7) * mm, "end": v(-12.89, -12.64) * mm});
            skLineSegment(sketch, "E377", {"start": v(-12.89, -12.64) * mm, "end": v(-13.07, -12.62) * mm});
            skLineSegment(sketch, "E378", {"start": v(-13.07, -12.62) * mm, "end": v(-13.25, -12.64) * mm});
            skLineSegment(sketch, "E379", {"start": v(-13.25, -12.64) * mm, "end": v(-13.44, -12.72) * mm});
            skLineSegment(sketch, "E380", {"start": v(-13.44, -12.72) * mm, "end": v(-13.62, -12.87) * mm});
            skLineSegment(sketch, "E381", {"start": v(-13.62, -12.87) * mm, "end": v(-13.72, -12.98) * mm});
            skLineSegment(sketch, "E382", {"start": v(-13.72, -12.98) * mm, "end": v(-13.8, -13.08) * mm});
            skLineSegment(sketch, "E383", {"start": v(-13.8, -13.08) * mm, "end": v(-13.87, -13.17) * mm});
            skLineSegment(sketch, "E384", {"start": v(-13.87, -13.17) * mm, "end": v(-13.95, -13.24) * mm});
            skLineSegment(sketch, "E385", {"start": v(-13.95, -13.24) * mm, "end": v(-14.05, -13.3) * mm});
            skLineSegment(sketch, "E386", {"start": v(-14.05, -13.3) * mm, "end": v(-14.19, -13.33) * mm});
            skLineSegment(sketch, "E387", {"start": v(-14.19, -13.33) * mm, "end": v(-14.38, -13.34) * mm});
            skLineSegment(sketch, "E388", {"start": v(-14.38, -13.34) * mm, "end": v(-14.65, -13.3) * mm});
            skLineSegment(sketch, "E389", {"start": v(-14.65, -13.3) * mm, "end": v(-14.88, -13.2) * mm});
            skLineSegment(sketch, "E390", {"start": v(-14.88, -13.2) * mm, "end": v(-15.08, -13.06) * mm});
            skLineSegment(sketch, "E391", {"start": v(-15.08, -13.06) * mm, "end": v(-15.24, -12.87) * mm});
            skLineSegment(sketch, "E392", {"start": v(-15.24, -12.87) * mm, "end": v(-15.36, -12.65) * mm});
            skLineSegment(sketch, "E393", {"start": v(-15.36, -12.65) * mm, "end": v(-15.45, -12.39) * mm});
            skLineSegment(sketch, "E394", {"start": v(-15.45, -12.39) * mm, "end": v(-15.5, -12.1) * mm});
            skLineSegment(sketch, "E395", {"start": v(-15.5, -12.1) * mm, "end": v(-15.49, -11.81) * mm});
            skLineSegment(sketch, "E396", {"start": v(-15.49, -11.81) * mm, "end": v(-15.44, -11.5) * mm});
            skLineSegment(sketch, "E397", {"start": v(-15.44, -11.5) * mm, "end": v(-15.35, -11.2) * mm});
            skLineSegment(sketch, "E398", {"start": v(-15.35, -11.2) * mm, "end": v(-15.2, -10.89) * mm});
            skLineSegment(sketch, "E399", {"start": v(-15.2, -10.89) * mm, "end": v(-15.02, -10.6) * mm});
            skLineSegment(sketch, "E400", {"start": v(-15.02, -10.6) * mm, "end": v(-14.77, -10.31) * mm});
            skLineSegment(sketch, "E401", {"start": v(-14.77, -10.31) * mm, "end": v(-14.47, -10.06) * mm});
            skLineSegment(sketch, "E402", {"start": v(-14.47, -10.06) * mm, "end": v(-14.12, -9.84) * mm});
            skLineSegment(sketch, "E403", {"start": v(-14.12, -9.84) * mm, "end": v(-13.7, -9.65) * mm});
            skLineSegment(sketch, "E404", {"start": v(-13.7, -9.65) * mm, "end": v(-13.22, -9.5) * mm});
            skLineSegment(sketch, "E405", {"start": v(-13.22, -9.5) * mm, "end": v(-12.76, -9.43) * mm});
            skLineSegment(sketch, "E406", {"start": v(-12.76, -9.43) * mm, "end": v(-12.3, -9.42) * mm});
            skLineSegment(sketch, "E407", {"start": v(-12.3, -9.42) * mm, "end": v(-11.86, -9.47) * mm});
            skLineSegment(sketch, "E408", {"start": v(-11.86, -9.47) * mm, "end": v(-11.43, -9.57) * mm});
            skLineSegment(sketch, "E409", {"start": v(-11.43, -9.57) * mm, "end": v(-11.02, -9.72) * mm});
            skLineSegment(sketch, "E410", {"start": v(-11.02, -9.72) * mm, "end": v(-10.64, -9.92) * mm});
            skLineSegment(sketch, "E411", {"start": v(-10.64, -9.92) * mm, "end": v(-10.27, -10.17) * mm});
            skLineSegment(sketch, "E412", {"start": v(-10.27, -10.17) * mm, "end": v(-9.93, -10.45) * mm});
            skLineSegment(sketch, "E413", {"start": v(-9.93, -10.45) * mm, "end": v(-9.62, -10.77) * mm});
            skLineSegment(sketch, "E414", {"start": v(-9.62, -10.77) * mm, "end": v(-9.33, -11.12) * mm});
            skLineSegment(sketch, "E415", {"start": v(-9.33, -11.12) * mm, "end": v(-9.08, -11.5) * mm});
            skLineSegment(sketch, "E416", {"start": v(-9.08, -11.5) * mm, "end": v(-8.85, -11.9) * mm});
            skLineSegment(sketch, "E417", {"start": v(-8.85, -11.9) * mm, "end": v(-8.66, -12.3) * mm});
            skLineSegment(sketch, "E418", {"start": v(-8.66, -12.3) * mm, "end": v(-8.5, -12.74) * mm});
            skLineSegment(sketch, "E419", {"start": v(-8.5, -12.74) * mm, "end": v(-8.38, -13.18) * mm});
            skLineSegment(sketch, "E420", {"start": v(-8.38, -13.18) * mm, "end": v(-8.3, -13.63) * mm});
            skLineSegment(sketch, "E421", {"start": v(-8.3, -13.63) * mm, "end": v(-8.27, -14.07) * mm});
            skLineSegment(sketch, "E422", {"start": v(-8.27, -14.07) * mm, "end": v(-8.28, -14.71) * mm});
            skLineSegment(sketch, "E423", {"start": v(-8.28, -14.71) * mm, "end": v(-8.36, -15.32) * mm});
            skLineSegment(sketch, "E424", {"start": v(-8.36, -15.32) * mm, "end": v(-8.5, -15.9) * mm});
            skLineSegment(sketch, "E425", {"start": v(-8.5, -15.9) * mm, "end": v(-8.7, -16.45) * mm});
            skLineSegment(sketch, "E426", {"start": v(-8.7, -16.45) * mm, "end": v(-8.96, -16.96) * mm});
            skLineSegment(sketch, "E427", {"start": v(-8.96, -16.96) * mm, "end": v(-9.26, -17.45) * mm});
            skLineSegment(sketch, "E428", {"start": v(-9.26, -17.45) * mm, "end": v(-9.6, -17.9) * mm});
            skLineSegment(sketch, "E429", {"start": v(-9.6, -17.9) * mm, "end": v(-9.97, -18.3) * mm});
            skLineSegment(sketch, "E430", {"start": v(-9.97, -18.3) * mm, "end": v(-10.38, -18.69) * mm});
            skLineSegment(sketch, "E431", {"start": v(-10.38, -18.69) * mm, "end": v(-10.81, -19.03) * mm});
            skLineSegment(sketch, "E432", {"start": v(-10.81, -19.03) * mm, "end": v(-11.26, -19.33) * mm});
            skLineSegment(sketch, "E433", {"start": v(-11.26, -19.33) * mm, "end": v(-11.72, -19.6) * mm});
            skLineSegment(sketch, "E434", {"start": v(-11.72, -19.6) * mm, "end": v(-12.2, -19.82) * mm});
            skLineSegment(sketch, "E435", {"start": v(-12.2, -19.82) * mm, "end": v(-12.66, -20) * mm});
            skLineSegment(sketch, "E436", {"start": v(-12.66, -20) * mm, "end": v(-13.38, -20.22) * mm});
            skLineSegment(sketch, "E437", {"start": v(-13.38, -20.22) * mm, "end": v(-14.1, -20.36) * mm});
            skLineSegment(sketch, "E438", {"start": v(-14.1, -20.36) * mm, "end": v(-14.8, -20.43) * mm});
            skLineSegment(sketch, "E439", {"start": v(-14.8, -20.43) * mm, "end": v(-15.48, -20.43) * mm});
            skLineSegment(sketch, "E440", {"start": v(-15.48, -20.43) * mm, "end": v(-16.16, -20.36) * mm});
            skLineSegment(sketch, "E441", {"start": v(-16.16, -20.36) * mm, "end": v(-16.81, -20.22) * mm});
            skLineSegment(sketch, "E442", {"start": v(-16.81, -20.22) * mm, "end": v(-17.45, -20.03) * mm});
            skLineSegment(sketch, "E443", {"start": v(-17.45, -20.03) * mm, "end": v(-18.06, -19.78) * mm});
            skLineSegment(sketch, "E444", {"start": v(-18.06, -19.78) * mm, "end": v(-18.65, -19.48) * mm});
            skLineSegment(sketch, "E445", {"start": v(-18.65, -19.48) * mm, "end": v(-19.21, -19.13) * mm});
            skLineSegment(sketch, "E446", {"start": v(-19.21, -19.13) * mm, "end": v(-19.75, -18.73) * mm});
            skLineSegment(sketch, "E447", {"start": v(-19.75, -18.73) * mm, "end": v(-20.25, -18.29) * mm});
            skLineSegment(sketch, "E448", {"start": v(-20.25, -18.29) * mm, "end": v(-20.72, -17.8) * mm});
            skLineSegment(sketch, "E449", {"start": v(-20.72, -17.8) * mm, "end": v(-21.15, -17.29) * mm});
            skLineSegment(sketch, "E450", {"start": v(-21.15, -17.29) * mm, "end": v(-21.55, -16.73) * mm});
            skLineSegment(sketch, "E451", {"start": v(-21.55, -16.73) * mm, "end": v(-21.9, -16.15) * mm});
            skLineSegment(sketch, "E452", {"start": v(-21.9, -16.15) * mm, "end": v(-22.21, -15.54) * mm});
            skLineSegment(sketch, "E453", {"start": v(-22.21, -15.54) * mm, "end": v(-22.48, -14.91) * mm});
            skLineSegment(sketch, "E454", {"start": v(-22.48, -14.91) * mm, "end": v(-22.7, -14.26) * mm});
            skLineSegment(sketch, "E455", {"start": v(-22.7, -14.26) * mm, "end": v(-22.87, -13.6) * mm});
            skLineSegment(sketch, "E456", {"start": v(-22.87, -13.6) * mm, "end": v(-23, -12.9) * mm});
            skLineSegment(sketch, "E457", {"start": v(-23, -12.9) * mm, "end": v(-23.06, -12.21) * mm});
            skLineSegment(sketch, "E458", {"start": v(-23.06, -12.21) * mm, "end": v(-23.07, -11.51) * mm});
            skLineSegment(sketch, "E459", {"start": v(-23.07, -11.51) * mm, "end": v(-23.03, -10.8) * mm});
            skLineSegment(sketch, "E460", {"start": v(-23.03, -10.8) * mm, "end": v(-22.9, -9.98) * mm});
            skLineSegment(sketch, "E461", {"start": v(-22.9, -9.98) * mm, "end": v(-22.7, -9.17) * mm});
            skLineSegment(sketch, "E462", {"start": v(-22.7, -9.17) * mm, "end": v(-22.45, -8.39) * mm});
            skLineSegment(sketch, "E463", {"start": v(-22.45, -8.39) * mm, "end": v(-22.13, -7.63) * mm});
            skLineSegment(sketch, "E464", {"start": v(-22.13, -7.63) * mm, "end": v(-21.75, -6.91) * mm});
            skLineSegment(sketch, "E465", {"start": v(-21.75, -6.91) * mm, "end": v(-21.32, -6.22) * mm});
            skLineSegment(sketch, "E466", {"start": v(-21.32, -6.22) * mm, "end": v(-20.83, -5.58) * mm});
            skLineSegment(sketch, "E467", {"start": v(-20.83, -5.58) * mm, "end": v(-20.29, -4.97) * mm});
            skLineSegment(sketch, "E468", {"start": v(-20.29, -4.97) * mm, "end": v(-19.7, -4.4) * mm});
            skLineSegment(sketch, "E469", {"start": v(-19.7, -4.4) * mm, "end": v(-19.06, -3.88) * mm});
            skLineSegment(sketch, "E470", {"start": v(-19.06, -3.88) * mm, "end": v(-18.38, -3.4) * mm});
            skLineSegment(sketch, "E471", {"start": v(-18.38, -3.4) * mm, "end": v(-17.65, -2.99) * mm});
            skLineSegment(sketch, "E472", {"start": v(-17.65, -2.99) * mm, "end": v(-16.89, -2.62) * mm});
            skLineSegment(sketch, "E473", {"start": v(-16.89, -2.62) * mm, "end": v(-16.09, -2.32) * mm});
            skLineSegment(sketch, "E474", {"start": v(-16.09, -2.32) * mm, "end": v(-15.25, -2.07) * mm});
            skLineSegment(sketch, "E475", {"start": v(-15.25, -2.07) * mm, "end": v(-14.38, -1.88) * mm});
            skLineSegment(sketch, "E476", {"start": v(-14.38, -1.88) * mm, "end": v(-13.48, -1.76) * mm});
            skLineSegment(sketch, "E477", {"start": v(-13.48, -1.76) * mm, "end": v(-12.56, -1.71) * mm});
            skLineSegment(sketch, "E478", {"start": v(-12.56, -1.71) * mm, "end": v(-11.6, -1.73) * mm});
            skLineSegment(sketch, "E479", {"start": v(-11.6, -1.73) * mm, "end": v(-10.74, -1.82) * mm});
            skLineSegment(sketch, "E480", {"start": v(-10.74, -1.82) * mm, "end": v(-9.9, -1.97) * mm});
            skLineSegment(sketch, "E481", {"start": v(-9.9, -1.97) * mm, "end": v(-9.1, -2.18) * mm});
            skLineSegment(sketch, "E482", {"start": v(-9.1, -2.18) * mm, "end": v(-8.3, -2.46) * mm});
            skLineSegment(sketch, "E483", {"start": v(-8.3, -2.46) * mm, "end": v(-7.55, -2.78) * mm});
            skLineSegment(sketch, "E484", {"start": v(-7.55, -2.78) * mm, "end": v(-6.82, -3.16) * mm});
            skLineSegment(sketch, "E485", {"start": v(-6.82, -3.16) * mm, "end": v(-6.13, -3.6) * mm});
            skLineSegment(sketch, "E486", {"start": v(-6.13, -3.6) * mm, "end": v(-5.46, -4.07) * mm});
            skLineSegment(sketch, "E487", {"start": v(-5.46, -4.07) * mm, "end": v(-4.83, -4.59) * mm});
            skLineSegment(sketch, "E488", {"start": v(-4.83, -4.59) * mm, "end": v(-4.24, -5.15) * mm});
            skLineSegment(sketch, "E489", {"start": v(-4.24, -5.15) * mm, "end": v(-3.69, -5.74) * mm});
            skLineSegment(sketch, "E490", {"start": v(-3.69, -5.74) * mm, "end": v(-3.17, -6.37) * mm});
            skLineSegment(sketch, "E491", {"start": v(-3.17, -6.37) * mm, "end": v(-2.7, -7.02) * mm});
            skLineSegment(sketch, "E492", {"start": v(-2.7, -7.02) * mm, "end": v(-2.26, -7.7) * mm});
            skLineSegment(sketch, "E493", {"start": v(-2.26, -7.7) * mm, "end": v(-1.87, -8.41) * mm});
            skLineSegment(sketch, "E494", {"start": v(-1.87, -8.41) * mm, "end": v(-1.53, -9.14) * mm});
            skLineSegment(sketch, "E495", {"start": v(-1.53, -9.14) * mm, "end": v(-1.23, -9.88) * mm});
            skLineSegment(sketch, "E496", {"start": v(-1.23, -9.88) * mm, "end": v(-0.98, -10.63) * mm});
            skLineSegment(sketch, "E497", {"start": v(-0.98, -10.63) * mm, "end": v(-0.78, -11.4) * mm});
            skLineSegment(sketch, "E498", {"start": v(-0.78, -11.4) * mm, "end": v(-0.64, -12.04) * mm});
            skLineSegment(sketch, "E499", {"start": v(-0.64, -12.04) * mm, "end": v(-0.51, -12.65) * mm});
            skLineSegment(sketch, "E500", {"start": v(-0.51, -12.65) * mm, "end": v(-0.4, -13.22) * mm});
            skLineSegment(sketch, "E501", {"start": v(-0.4, -13.22) * mm, "end": v(-0.28, -13.76) * mm});
            skLineSegment(sketch, "E502", {"start": v(-0.28, -13.76) * mm, "end": v(-0.17, -14.28) * mm});
            skLineSegment(sketch, "E503", {"start": v(-0.17, -14.28) * mm, "end": v(-0.04, -14.78) * mm});
            skLineSegment(sketch, "E504", {"start": v(-0.04, -14.78) * mm, "end": v(0.1, -15.27) * mm});
            skLineSegment(sketch, "E505", {"start": v(0.1, -15.27) * mm, "end": v(0.25, -15.76) * mm});
            skLineSegment(sketch, "E506", {"start": v(0.25, -15.76) * mm, "end": v(0.43, -16.26) * mm});
            skLineSegment(sketch, "E507", {"start": v(0.43, -16.26) * mm, "end": v(0.65, -16.76) * mm});
            skLineSegment(sketch, "E508", {"start": v(0.65, -16.76) * mm, "end": v(0.9, -17.28) * mm});
            skLineSegment(sketch, "E509", {"start": v(0.9, -17.28) * mm, "end": v(1.2, -17.82) * mm});
            skLineSegment(sketch, "E510", {"start": v(1.2, -17.82) * mm, "end": v(1.54, -18.38) * mm});
            skLineSegment(sketch, "E511", {"start": v(1.54, -18.38) * mm, "end": v(1.93, -18.99) * mm});
            skLineSegment(sketch, "E512", {"start": v(1.93, -18.99) * mm, "end": v(2.47, -19.72) * mm});
            skLineSegment(sketch, "E513", {"start": v(2.47, -19.72) * mm, "end": v(3.03, -20.42) * mm});
            skLineSegment(sketch, "E514", {"start": v(3.03, -20.42) * mm, "end": v(3.63, -21.06) * mm});
            skLineSegment(sketch, "E515", {"start": v(3.63, -21.06) * mm, "end": v(4.27, -21.67) * mm});
            skLineSegment(sketch, "E516", {"start": v(4.27, -21.67) * mm, "end": v(4.96, -22.25) * mm});
            skLineSegment(sketch, "E517", {"start": v(4.96, -22.25) * mm, "end": v(5.7, -22.8) * mm});
            skLineSegment(sketch, "E518", {"start": v(5.7, -22.8) * mm, "end": v(6.5, -23.33) * mm});
            skLineSegment(sketch, "E519", {"start": v(6.5, -23.33) * mm, "end": v(7.39, -23.83) * mm});
            skLineSegment(sketch, "E520", {"start": v(7.39, -23.83) * mm, "end": v(8.1, -24.18) * mm});
            skLineSegment(sketch, "E521", {"start": v(8.1, -24.18) * mm, "end": v(8.86, -24.5) * mm});
            skLineSegment(sketch, "E522", {"start": v(8.86, -24.5) * mm, "end": v(9.67, -24.76) * mm});
            skLineSegment(sketch, "E523", {"start": v(9.67, -24.76) * mm, "end": v(10.52, -25) * mm});
            skLineSegment(sketch, "E524", {"start": v(10.52, -25) * mm, "end": v(11.4, -25.17) * mm});
            skLineSegment(sketch, "E525", {"start": v(11.4, -25.17) * mm, "end": v(12.3, -25.3) * mm});
            skLineSegment(sketch, "E526", {"start": v(12.3, -25.3) * mm, "end": v(13.21, -25.38) * mm});
            skLineSegment(sketch, "E527", {"start": v(13.21, -25.38) * mm, "end": v(14.13, -25.4) * mm});
            skLineSegment(sketch, "E528", {"start": v(14.13, -25.4) * mm, "end": v(15.04, -25.36) * mm});
            skLineSegment(sketch, "E529", {"start": v(15.04, -25.36) * mm, "end": v(15.94, -25.25) * mm});
            skLineSegment(sketch, "E530", {"start": v(15.94, -25.25) * mm, "end": v(16.79, -25.1) * mm});
            skLineSegment(sketch, "E531", {"start": v(16.79, -25.1) * mm, "end": v(17.57, -24.9) * mm});
            skLineSegment(sketch, "E532", {"start": v(17.57, -24.9) * mm, "end": v(18.3, -24.68) * mm});
            skLineSegment(sketch, "E533", {"start": v(18.3, -24.68) * mm, "end": v(18.99, -24.43) * mm});
            skLineSegment(sketch, "E534", {"start": v(18.99, -24.43) * mm, "end": v(19.63, -24.15) * mm});
            skLineSegment(sketch, "E535", {"start": v(19.63, -24.15) * mm, "end": v(20.24, -23.84) * mm});
            skLineSegment(sketch, "E536", {"start": v(20.24, -23.84) * mm, "end": v(20.82, -23.5) * mm});
            skLineSegment(sketch, "E537", {"start": v(20.82, -23.5) * mm, "end": v(21.37, -23.14) * mm});
            skLineSegment(sketch, "E538", {"start": v(21.37, -23.14) * mm, "end": v(21.91, -22.76) * mm});
            skLineSegment(sketch, "E539", {"start": v(21.91, -22.76) * mm, "end": v(22.44, -22.37) * mm});
            skLineSegment(sketch, "E540", {"start": v(22.44, -22.37) * mm, "end": v(22.96, -21.95) * mm});
            skLineSegment(sketch, "E541", {"start": v(22.96, -21.95) * mm, "end": v(23.49, -21.49) * mm});
            skLineSegment(sketch, "E542", {"start": v(23.49, -21.49) * mm, "end": v(23.98, -20.98) * mm});
            skLineSegment(sketch, "E543", {"start": v(23.98, -20.98) * mm, "end": v(24.44, -20.44) * mm});
            skLineSegment(sketch, "E544", {"start": v(24.44, -20.44) * mm, "end": v(24.87, -19.86) * mm});
            skLineSegment(sketch, "E545", {"start": v(24.87, -19.86) * mm, "end": v(25.26, -19.25) * mm});
            skLineSegment(sketch, "E546", {"start": v(25.26, -19.25) * mm, "end": v(25.61, -18.62) * mm});
            skLineSegment(sketch, "E547", {"start": v(25.61, -18.62) * mm, "end": v(25.93, -17.95) * mm});
            skLineSegment(sketch, "E548", {"start": v(25.93, -17.95) * mm, "end": v(26.2, -17.27) * mm});
            skLineSegment(sketch, "E549", {"start": v(26.2, -17.27) * mm, "end": v(26.44, -16.57) * mm});
            skLineSegment(sketch, "E550", {"start": v(26.44, -16.57) * mm, "end": v(26.64, -15.85) * mm});
            skLineSegment(sketch, "E551", {"start": v(26.64, -15.85) * mm, "end": v(26.8, -15.11) * mm});
            skLineSegment(sketch, "E552", {"start": v(26.8, -15.11) * mm, "end": v(26.9, -14.37) * mm});
            skLineSegment(sketch, "E553", {"start": v(26.9, -14.37) * mm, "end": v(26.98, -13.62) * mm});
            skLineSegment(sketch, "E554", {"start": v(26.98, -13.62) * mm, "end": v(27.01, -12.86) * mm});
            skLineSegment(sketch, "E555", {"start": v(27.01, -12.86) * mm, "end": v(27, -12.1) * mm});
            skLineSegment(sketch, "E556", {"start": v(27, -12.1) * mm, "end": v(26.94, -11.35) * mm});
            skLineSegment(sketch, "E557", {"start": v(26.94, -11.35) * mm, "end": v(26.84, -10.6) * mm});
            skLineSegment(sketch, "E558", {"start": v(26.84, -10.6) * mm, "end": v(26.69, -9.86) * mm});
            skLineSegment(sketch, "E559", {"start": v(26.69, -9.86) * mm, "end": v(26.5, -9.12) * mm});
            skLineSegment(sketch, "E560", {"start": v(26.5, -9.12) * mm, "end": v(26.25, -8.4) * mm});
            skLineSegment(sketch, "E561", {"start": v(26.25, -8.4) * mm, "end": v(25.95, -7.7) * mm});
            skLineSegment(sketch, "E562", {"start": v(25.95, -7.7) * mm, "end": v(25.61, -7.02) * mm});
            skLineSegment(sketch, "E563", {"start": v(25.61, -7.02) * mm, "end": v(25.22, -6.36) * mm});
            skLineSegment(sketch, "E564", {"start": v(25.22, -6.36) * mm, "end": v(24.78, -5.72) * mm});
            skLineSegment(sketch, "E565", {"start": v(24.78, -5.72) * mm, "end": v(24.29, -5.11) * mm});
            skLineSegment(sketch, "E566", {"start": v(24.29, -5.11) * mm, "end": v(23.74, -4.54) * mm});
            skLineSegment(sketch, "E567", {"start": v(23.74, -4.54) * mm, "end": v(23.15, -4) * mm});
            skLineSegment(sketch, "E568", {"start": v(23.15, -4) * mm, "end": v(22.5, -3.49) * mm});
            skLineSegment(sketch, "E569", {"start": v(22.5, -3.49) * mm, "end": v(21.79, -3.03) * mm});
            skLineSegment(sketch, "E570", {"start": v(21.79, -3.03) * mm, "end": v(21.03, -2.6) * mm});
            skLineSegment(sketch, "E571", {"start": v(21.03, -2.6) * mm, "end": v(20.21, -2.23) * mm});
            skLineSegment(sketch, "E572", {"start": v(20.21, -2.23) * mm, "end": v(19.5, -1.97) * mm});
            skLineSegment(sketch, "E573", {"start": v(19.5, -1.97) * mm, "end": v(18.78, -1.77) * mm});
            skLineSegment(sketch, "E574", {"start": v(18.78, -1.77) * mm, "end": v(18.05, -1.62) * mm});
            skLineSegment(sketch, "E575", {"start": v(18.05, -1.62) * mm, "end": v(17.3, -1.53) * mm});
            skLineSegment(sketch, "E576", {"start": v(17.3, -1.53) * mm, "end": v(16.57, -1.5) * mm});
            skLineSegment(sketch, "E577", {"start": v(16.57, -1.5) * mm, "end": v(15.83, -1.52) * mm});
            skLineSegment(sketch, "E578", {"start": v(15.83, -1.52) * mm, "end": v(15.09, -1.6) * mm});
            skLineSegment(sketch, "E579", {"start": v(15.09, -1.6) * mm, "end": v(14.36, -1.72) * mm});
            skLineSegment(sketch, "E580", {"start": v(14.36, -1.72) * mm, "end": v(13.65, -1.9) * mm});
            skLineSegment(sketch, "E581", {"start": v(13.65, -1.9) * mm, "end": v(12.95, -2.12) * mm});
            skLineSegment(sketch, "E582", {"start": v(12.95, -2.12) * mm, "end": v(12.27, -2.4) * mm});
            skLineSegment(sketch, "E583", {"start": v(12.27, -2.4) * mm, "end": v(11.62, -2.73) * mm});
            skLineSegment(sketch, "E584", {"start": v(11.62, -2.73) * mm, "end": v(11, -3.1) * mm});
            skLineSegment(sketch, "E585", {"start": v(11, -3.1) * mm, "end": v(10.4, -3.53) * mm});
            skLineSegment(sketch, "E586", {"start": v(10.4, -3.53) * mm, "end": v(9.84, -4) * mm});
            skLineSegment(sketch, "E587", {"start": v(9.84, -4) * mm, "end": v(9.32, -4.51) * mm});
            skLineSegment(sketch, "E588", {"start": v(9.32, -4.51) * mm, "end": v(8.85, -5.07) * mm});
            skLineSegment(sketch, "E589", {"start": v(8.85, -5.07) * mm, "end": v(8.42, -5.67) * mm});
            skLineSegment(sketch, "E590", {"start": v(8.42, -5.67) * mm, "end": v(8.05, -6.32) * mm});
            skLineSegment(sketch, "E591", {"start": v(8.05, -6.32) * mm, "end": v(7.73, -7) * mm});
            skLineSegment(sketch, "E592", {"start": v(7.73, -7) * mm, "end": v(7.47, -7.74) * mm});
            skLineSegment(sketch, "E593", {"start": v(7.47, -7.74) * mm, "end": v(7.28, -8.5) * mm});
            skLineSegment(sketch, "E594", {"start": v(7.28, -8.5) * mm, "end": v(7.15, -9.25) * mm});
            skLineSegment(sketch, "E595", {"start": v(7.15, -9.25) * mm, "end": v(7.1, -9.98) * mm});
            skLineSegment(sketch, "E596", {"start": v(7.1, -9.98) * mm, "end": v(7.1, -10.68) * mm});
            skLineSegment(sketch, "E597", {"start": v(7.1, -10.68) * mm, "end": v(7.17, -11.36) * mm});
            skLineSegment(sketch, "E598", {"start": v(7.17, -11.36) * mm, "end": v(7.3, -12.01) * mm});
            skLineSegment(sketch, "E599", {"start": v(7.3, -12.01) * mm, "end": v(7.47, -12.64) * mm});
            skLineSegment(sketch, "E600", {"start": v(7.47, -12.64) * mm, "end": v(7.68, -13.23) * mm});
            skLineSegment(sketch, "E601", {"start": v(7.68, -13.23) * mm, "end": v(7.94, -13.79) * mm});
            skLineSegment(sketch, "E602", {"start": v(7.94, -13.79) * mm, "end": v(8.24, -14.31) * mm});
            skLineSegment(sketch, "E603", {"start": v(8.24, -14.31) * mm, "end": v(8.57, -14.8) * mm});
            skLineSegment(sketch, "E604", {"start": v(8.57, -14.8) * mm, "end": v(8.93, -15.26) * mm});
            skLineSegment(sketch, "E605", {"start": v(8.93, -15.26) * mm, "end": v(9.3, -15.67) * mm});
            skLineSegment(sketch, "E606", {"start": v(9.3, -15.67) * mm, "end": v(9.71, -16.04) * mm});
            skLineSegment(sketch, "E607", {"start": v(9.71, -16.04) * mm, "end": v(10.26, -16.46) * mm});
            skLineSegment(sketch, "E608", {"start": v(10.26, -16.46) * mm, "end": v(10.83, -16.8) * mm});
            skLineSegment(sketch, "E609", {"start": v(10.83, -16.8) * mm, "end": v(11.42, -17.1) * mm});
            skLineSegment(sketch, "E610", {"start": v(11.42, -17.1) * mm, "end": v(12.02, -17.3) * mm});
            skLineSegment(sketch, "E611", {"start": v(12.02, -17.3) * mm, "end": v(12.62, -17.46) * mm});
            skLineSegment(sketch, "E612", {"start": v(12.62, -17.46) * mm, "end": v(13.23, -17.55) * mm});
            skLineSegment(sketch, "E613", {"start": v(13.23, -17.55) * mm, "end": v(13.84, -17.58) * mm});
            skLineSegment(sketch, "E614", {"start": v(13.84, -17.58) * mm, "end": v(14.44, -17.56) * mm});
            skLineSegment(sketch, "E615", {"start": v(14.44, -17.56) * mm, "end": v(15.03, -17.47) * mm});
            skLineSegment(sketch, "E616", {"start": v(15.03, -17.47) * mm, "end": v(15.6, -17.33) * mm});
            skLineSegment(sketch, "E617", {"start": v(15.6, -17.33) * mm, "end": v(16.15, -17.14) * mm});
            skLineSegment(sketch, "E618", {"start": v(16.15, -17.14) * mm, "end": v(16.67, -16.9) * mm});
            skLineSegment(sketch, "E619", {"start": v(16.67, -16.9) * mm, "end": v(17.16, -16.61) * mm});
            skLineSegment(sketch, "E620", {"start": v(17.16, -16.61) * mm, "end": v(17.61, -16.27) * mm});
            skLineSegment(sketch, "E621", {"start": v(17.61, -16.27) * mm, "end": v(18.02, -15.89) * mm});
            skLineSegment(sketch, "E622", {"start": v(18.02, -15.89) * mm, "end": v(18.39, -15.46) * mm});
            skLineSegment(sketch, "E623", {"start": v(18.39, -15.46) * mm, "end": v(18.7, -14.99) * mm});
            skLineSegment(sketch, "E624", {"start": v(18.7, -14.99) * mm, "end": v(18.95, -14.48) * mm});
            skLineSegment(sketch, "E625", {"start": v(18.95, -14.48) * mm, "end": v(19.15, -13.93) * mm});
            skLineSegment(sketch, "E626", {"start": v(19.15, -13.93) * mm, "end": v(19.27, -13.34) * mm});
            skLineSegment(sketch, "E627", {"start": v(19.27, -13.34) * mm, "end": v(19.33, -12.79) * mm});
            skLineSegment(sketch, "E628", {"start": v(19.33, -12.79) * mm, "end": v(19.32, -12.27) * mm});
            skLineSegment(sketch, "E629", {"start": v(19.32, -12.27) * mm, "end": v(19.25, -11.79) * mm});
            skLineSegment(sketch, "E630", {"start": v(19.25, -11.79) * mm, "end": v(19.13, -11.35) * mm});
            skLineSegment(sketch, "E631", {"start": v(19.13, -11.35) * mm, "end": v(18.96, -10.95) * mm});
            skLineSegment(sketch, "E632", {"start": v(18.96, -10.95) * mm, "end": v(18.75, -10.58) * mm});
            skLineSegment(sketch, "E633", {"start": v(18.75, -10.58) * mm, "end": v(18.5, -10.26) * mm});
            skLineSegment(sketch, "E634", {"start": v(18.5, -10.26) * mm, "end": v(18.23, -9.98) * mm});
            skLineSegment(sketch, "E635", {"start": v(18.23, -9.98) * mm, "end": v(17.93, -9.74) * mm});
            skLineSegment(sketch, "E636", {"start": v(17.93, -9.74) * mm, "end": v(17.6, -9.54) * mm});
            skLineSegment(sketch, "E637", {"start": v(17.6, -9.54) * mm, "end": v(17.28, -9.38) * mm});
            skLineSegment(sketch, "E638", {"start": v(17.28, -9.38) * mm, "end": v(16.94, -9.26) * mm});
            skLineSegment(sketch, "E639", {"start": v(16.94, -9.26) * mm, "end": v(16.6, -9.19) * mm});
            skLineSegment(sketch, "E640", {"start": v(16.6, -9.19) * mm, "end": v(16.26, -9.15) * mm});
            skLineSegment(sketch, "E641", {"start": v(16.26, -9.15) * mm, "end": v(15.94, -9.16) * mm});
            skLineSegment(sketch, "E642", {"start": v(15.94, -9.16) * mm, "end": v(15.63, -9.2) * mm});
            skLineSegment(sketch, "E643", {"start": v(15.63, -9.2) * mm, "end": v(15.34, -9.3) * mm});
            skLineSegment(sketch, "E644", {"start": v(15.34, -9.3) * mm, "end": v(15.08, -9.43) * mm});
            skLineSegment(sketch, "E645", {"start": v(15.08, -9.43) * mm, "end": v(14.85, -9.6) * mm});
            skLineSegment(sketch, "E646", {"start": v(14.85, -9.6) * mm, "end": v(14.66, -9.82) * mm});
            skLineSegment(sketch, "E647", {"start": v(14.66, -9.82) * mm, "end": v(14.52, -10.08) * mm});
            skLineSegment(sketch, "E648", {"start": v(14.52, -10.08) * mm, "end": v(14.43, -10.39) * mm});
            skLineSegment(sketch, "E649", {"start": v(14.43, -10.39) * mm, "end": v(14.39, -10.65) * mm});
            skLineSegment(sketch, "E650", {"start": v(14.39, -10.65) * mm, "end": v(14.39, -10.87) * mm});
            skLineSegment(sketch, "E651", {"start": v(14.39, -10.87) * mm, "end": v(14.42, -11.04) * mm});
            skLineSegment(sketch, "E652", {"start": v(14.42, -11.04) * mm, "end": v(14.48, -11.17) * mm});
            skLineSegment(sketch, "E653", {"start": v(14.48, -11.17) * mm, "end": v(14.57, -11.27) * mm});
            skLineSegment(sketch, "E654", {"start": v(14.57, -11.27) * mm, "end": v(14.68, -11.34) * mm});
            skLineSegment(sketch, "E655", {"start": v(14.68, -11.34) * mm, "end": v(14.8, -11.4) * mm});
            skLineSegment(sketch, "E656", {"start": v(14.8, -11.4) * mm, "end": v(14.94, -11.44) * mm});
            skLineSegment(sketch, "E657", {"start": v(14.94, -11.44) * mm, "end": v(15.08, -11.47) * mm});
            skLineSegment(sketch, "E658", {"start": v(15.08, -11.47) * mm, "end": v(15.21, -11.5) * mm});
            skLineSegment(sketch, "E659", {"start": v(15.21, -11.5) * mm, "end": v(15.34, -11.53) * mm});
            skLineSegment(sketch, "E660", {"start": v(15.34, -11.53) * mm, "end": v(15.46, -11.57) * mm});
            skLineSegment(sketch, "E661", {"start": v(15.46, -11.57) * mm, "end": v(15.57, -11.62) * mm});
            skLineSegment(sketch, "E662", {"start": v(15.57, -11.62) * mm, "end": v(15.72, -11.76) * mm});
            skLineSegment(sketch, "E663", {"start": v(15.72, -11.76) * mm, "end": v(15.82, -11.92) * mm});
            skLineSegment(sketch, "E664", {"start": v(15.82, -11.92) * mm, "end": v(15.88, -12.1) * mm});
            skLineSegment(sketch, "E665", {"start": v(15.88, -12.1) * mm, "end": v(15.89, -12.3) * mm});
            skLineSegment(sketch, "E666", {"start": v(15.89, -12.3) * mm, "end": v(15.86, -12.5) * mm});
            skLineSegment(sketch, "E667", {"start": v(15.86, -12.5) * mm, "end": v(15.8, -12.7) * mm});
            skLineSegment(sketch, "E668", {"start": v(15.8, -12.7) * mm, "end": v(15.71, -12.88) * mm});
            skLineSegment(sketch, "E669", {"start": v(15.71, -12.88) * mm, "end": v(15.6, -13.06) * mm});
            skLineSegment(sketch, "E670", {"start": v(15.6, -13.06) * mm, "end": v(15.48, -13.22) * mm});
            skLineSegment(sketch, "E671", {"start": v(15.48, -13.22) * mm, "end": v(15.35, -13.36) * mm});
            skLineSegment(sketch, "E672", {"start": v(15.35, -13.36) * mm, "end": v(15.04, -13.59) * mm});
            skLineSegment(sketch, "E673", {"start": v(15.04, -13.59) * mm, "end": v(14.7, -13.75) * mm});
            skLineSegment(sketch, "E674", {"start": v(14.7, -13.75) * mm, "end": v(14.37, -13.84) * mm});
            skLineSegment(sketch, "E675", {"start": v(14.37, -13.84) * mm, "end": v(14.02, -13.88) * mm});
            skLineSegment(sketch, "E676", {"start": v(14.02, -13.88) * mm, "end": v(13.67, -13.85) * mm});
            skLineSegment(sketch, "E677", {"start": v(13.67, -13.85) * mm, "end": v(13.32, -13.77) * mm});
            skLineSegment(sketch, "E678", {"start": v(13.32, -13.77) * mm, "end": v(12.98, -13.63) * mm});
            skLineSegment(sketch, "E679", {"start": v(12.98, -13.63) * mm, "end": v(12.65, -13.45) * mm});
            skLineSegment(sketch, "E680", {"start": v(12.65, -13.45) * mm, "end": v(12.33, -13.22) * mm});
            skLineSegment(sketch, "E681", {"start": v(12.33, -13.22) * mm, "end": v(12.04, -12.95) * mm});
            skLineSegment(sketch, "E682", {"start": v(12.04, -12.95) * mm, "end": v(11.77, -12.64) * mm});
            skLineSegment(sketch, "E683", {"start": v(11.77, -12.64) * mm, "end": v(11.54, -12.3) * mm});
            skLineSegment(sketch, "E684", {"start": v(11.54, -12.3) * mm, "end": v(11.33, -11.91) * mm});
            skLineSegment(sketch, "E685", {"start": v(11.33, -11.91) * mm, "end": v(11.17, -11.5) * mm});
            skLineSegment(sketch, "E686", {"start": v(11.17, -11.5) * mm, "end": v(11.05, -11.07) * mm});
            skLineSegment(sketch, "E687", {"start": v(11.05, -11.07) * mm, "end": v(10.98, -10.62) * mm});
            skLineSegment(sketch, "E688", {"start": v(10.98, -10.62) * mm, "end": v(10.96, -10.15) * mm});
            skLineSegment(sketch, "E689", {"start": v(10.96, -10.15) * mm, "end": v(11, -9.66) * mm});
            skLineSegment(sketch, "E690", {"start": v(11, -9.66) * mm, "end": v(11.1, -9.16) * mm});
            skLineSegment(sketch, "E691", {"start": v(11.1, -9.16) * mm, "end": v(11.27, -8.65) * mm});
            skLineSegment(sketch, "E692", {"start": v(11.27, -8.65) * mm, "end": v(11.49, -8.18) * mm});
            skLineSegment(sketch, "E693", {"start": v(11.49, -8.18) * mm, "end": v(11.76, -7.73) * mm});
            skLineSegment(sketch, "E694", {"start": v(11.76, -7.73) * mm, "end": v(12.07, -7.31) * mm});
            skLineSegment(sketch, "E695", {"start": v(12.07, -7.31) * mm, "end": v(12.44, -6.92) * mm});
            skLineSegment(sketch, "E696", {"start": v(12.44, -6.92) * mm, "end": v(12.85, -6.57) * mm});
            skLineSegment(sketch, "E697", {"start": v(12.85, -6.57) * mm, "end": v(13.3, -6.25) * mm});
            skLineSegment(sketch, "E698", {"start": v(13.3, -6.25) * mm, "end": v(13.79, -5.97) * mm});
            skLineSegment(sketch, "E699", {"start": v(13.79, -5.97) * mm, "end": v(14.3, -5.74) * mm});
            skLineSegment(sketch, "E700", {"start": v(14.3, -5.74) * mm, "end": v(14.86, -5.57) * mm});
            skLineSegment(sketch, "E701", {"start": v(14.86, -5.57) * mm, "end": v(15.44, -5.45) * mm});
            skLineSegment(sketch, "E702", {"start": v(15.44, -5.45) * mm, "end": v(16.05, -5.39) * mm});
            skLineSegment(sketch, "E703", {"start": v(16.05, -5.39) * mm, "end": v(16.68, -5.39) * mm});
            skLineSegment(sketch, "E704", {"start": v(16.68, -5.39) * mm, "end": v(17.33, -5.46) * mm});
            skLineSegment(sketch, "E705", {"start": v(17.33, -5.46) * mm, "end": v(18, -5.6) * mm});
            skLineSegment(sketch, "E706", {"start": v(18, -5.6) * mm, "end": v(18.65, -5.82) * mm});
            skLineSegment(sketch, "E707", {"start": v(18.65, -5.82) * mm, "end": v(19.27, -6.1) * mm});
            skLineSegment(sketch, "E708", {"start": v(19.27, -6.1) * mm, "end": v(19.85, -6.44) * mm});
            skLineSegment(sketch, "E709", {"start": v(19.85, -6.44) * mm, "end": v(20.4, -6.84) * mm});
            skLineSegment(sketch, "E710", {"start": v(20.4, -6.84) * mm, "end": v(20.92, -7.29) * mm});
            skLineSegment(sketch, "E711", {"start": v(20.92, -7.29) * mm, "end": v(21.4, -7.79) * mm});
            skLineSegment(sketch, "E712", {"start": v(21.4, -7.79) * mm, "end": v(21.82, -8.33) * mm});
            skLineSegment(sketch, "E713", {"start": v(21.82, -8.33) * mm, "end": v(22.2, -8.93) * mm});
            skLineSegment(sketch, "E714", {"start": v(22.2, -8.93) * mm, "end": v(22.51, -9.56) * mm});
            skLineSegment(sketch, "E715", {"start": v(22.51, -9.56) * mm, "end": v(22.77, -10.23) * mm});
            skLineSegment(sketch, "E716", {"start": v(22.77, -10.23) * mm, "end": v(22.97, -10.93) * mm});
            skLineSegment(sketch, "E717", {"start": v(22.97, -10.93) * mm, "end": v(23.11, -11.7) * mm});
            skLineSegment(sketch, "E718", {"start": v(23.11, -11.7) * mm, "end": v(23.18, -12.46) * mm});
            skLineSegment(sketch, "E719", {"start": v(23.18, -12.46) * mm, "end": v(23.18, -13.2) * mm});
            skLineSegment(sketch, "E720", {"start": v(23.18, -13.2) * mm, "end": v(23.11, -13.93) * mm});
            skLineSegment(sketch, "E721", {"start": v(23.11, -13.93) * mm, "end": v(22.98, -14.63) * mm});
            skLineSegment(sketch, "E722", {"start": v(22.98, -14.63) * mm, "end": v(22.78, -15.32) * mm});
            skLineSegment(sketch, "E723", {"start": v(22.78, -15.32) * mm, "end": v(22.53, -15.98) * mm});
            skLineSegment(sketch, "E724", {"start": v(22.53, -15.98) * mm, "end": v(22.23, -16.6) * mm});
            skLineSegment(sketch, "E725", {"start": v(22.23, -16.6) * mm, "end": v(21.87, -17.21) * mm});
            skLineSegment(sketch, "E726", {"start": v(21.87, -17.21) * mm, "end": v(21.47, -17.78) * mm});
            skLineSegment(sketch, "E727", {"start": v(21.47, -17.78) * mm, "end": v(21.02, -18.32) * mm});
            skLineSegment(sketch, "E728", {"start": v(21.02, -18.32) * mm, "end": v(20.53, -18.83) * mm});
            skLineSegment(sketch, "E729", {"start": v(20.53, -18.83) * mm, "end": v(20, -19.3) * mm});
            skLineSegment(sketch, "E730", {"start": v(20, -19.3) * mm, "end": v(19.43, -19.73) * mm});
            skLineSegment(sketch, "E731", {"start": v(19.43, -19.73) * mm, "end": v(18.84, -20.11) * mm});
            skLineSegment(sketch, "E732", {"start": v(18.84, -20.11) * mm, "end": v(18.21, -20.46) * mm});
            skLineSegment(sketch, "E733", {"start": v(18.21, -20.46) * mm, "end": v(17.56, -20.76) * mm});
            skLineSegment(sketch, "E734", {"start": v(17.56, -20.76) * mm, "end": v(16.89, -21) * mm});
            skLineSegment(sketch, "E735", {"start": v(16.89, -21) * mm, "end": v(16.2, -21.2) * mm});
            skLineSegment(sketch, "E736", {"start": v(16.2, -21.2) * mm, "end": v(15.5, -21.36) * mm});
            skLineSegment(sketch, "E737", {"start": v(15.5, -21.36) * mm, "end": v(14.77, -21.45) * mm});
            skLineSegment(sketch, "E738", {"start": v(14.77, -21.45) * mm, "end": v(14.04, -21.49) * mm});
            skLineSegment(sketch, "E739", {"start": v(14.04, -21.49) * mm, "end": v(13.3, -21.47) * mm});
            skLineSegment(sketch, "E740", {"start": v(13.3, -21.47) * mm, "end": v(12.4, -21.37) * mm});
            skLineSegment(sketch, "E741", {"start": v(12.4, -21.37) * mm, "end": v(11.53, -21.2) * mm});
            skLineSegment(sketch, "E742", {"start": v(11.53, -21.2) * mm, "end": v(10.69, -20.97) * mm});
            skLineSegment(sketch, "E743", {"start": v(10.69, -20.97) * mm, "end": v(9.89, -20.67) * mm});
            skLineSegment(sketch, "E744", {"start": v(9.89, -20.67) * mm, "end": v(9.12, -20.3) * mm});
            skLineSegment(sketch, "E745", {"start": v(9.12, -20.3) * mm, "end": v(8.4, -19.9) * mm});
            skLineSegment(sketch, "E746", {"start": v(8.4, -19.9) * mm, "end": v(7.7, -19.42) * mm});
            skLineSegment(sketch, "E747", {"start": v(7.7, -19.42) * mm, "end": v(7.06, -18.9) * mm});
            skLineSegment(sketch, "E748", {"start": v(7.06, -18.9) * mm, "end": v(6.46, -18.34) * mm});
            skLineSegment(sketch, "E749", {"start": v(6.46, -18.34) * mm, "end": v(5.9, -17.73) * mm});
            skLineSegment(sketch, "E750", {"start": v(5.9, -17.73) * mm, "end": v(5.4, -17.08) * mm});
            skLineSegment(sketch, "E751", {"start": v(5.4, -17.08) * mm, "end": v(4.94, -16.4) * mm});
            skLineSegment(sketch, "E752", {"start": v(4.94, -16.4) * mm, "end": v(4.53, -15.67) * mm});
            skLineSegment(sketch, "E753", {"start": v(4.53, -15.67) * mm, "end": v(4.17, -14.92) * mm});
            skLineSegment(sketch, "E754", {"start": v(4.17, -14.92) * mm, "end": v(3.86, -14.15) * mm});
            skLineSegment(sketch, "E755", {"start": v(3.86, -14.15) * mm, "end": v(3.61, -13.35) * mm});
            skLineSegment(sketch, "E756", {"start": v(3.61, -13.35) * mm, "end": v(3.42, -12.53) * mm});
            skLineSegment(sketch, "E757", {"start": v(3.42, -12.53) * mm, "end": v(3.28, -11.7) * mm});
            skLineSegment(sketch, "E758", {"start": v(3.28, -11.7) * mm, "end": v(3.2, -10.85) * mm});
            skLineSegment(sketch, "E759", {"start": v(3.2, -10.85) * mm, "end": v(3.19, -9.99) * mm});
            skLineSegment(sketch, "E760", {"start": v(3.19, -9.99) * mm, "end": v(3.23, -9.12) * mm});
            skLineSegment(sketch, "E761", {"start": v(3.23, -9.12) * mm, "end": v(3.34, -8.26) * mm});
            skLineSegment(sketch, "E762", {"start": v(3.34, -8.26) * mm, "end": v(3.52, -7.4) * mm});
            skLineSegment(sketch, "E763", {"start": v(3.52, -7.4) * mm, "end": v(3.76, -6.53) * mm});
            skLineSegment(sketch, "E764", {"start": v(3.76, -6.53) * mm, "end": v(4.08, -5.67) * mm});
            skLineSegment(sketch, "E765", {"start": v(4.08, -5.67) * mm, "end": v(4.46, -4.83) * mm});
            skLineSegment(sketch, "E766", {"start": v(4.46, -4.83) * mm, "end": v(4.91, -4) * mm});
            skLineSegment(sketch, "E767", {"start": v(4.91, -4) * mm, "end": v(5.44, -3.18) * mm});
            skLineSegment(sketch, "E768", {"start": v(5.44, -3.18) * mm, "end": v(5.92, -2.55) * mm});
            skLineSegment(sketch, "E769", {"start": v(5.92, -2.55) * mm, "end": v(6.42, -1.98) * mm});
            skLineSegment(sketch, "E770", {"start": v(6.42, -1.98) * mm, "end": v(6.93, -1.46) * mm});
            skLineSegment(sketch, "E771", {"start": v(6.93, -1.46) * mm, "end": v(7.46, -0.96) * mm});
            skLineSegment(sketch, "E772", {"start": v(7.46, -0.96) * mm, "end": v(7.99, -0.5) * mm});
            skLineSegment(sketch, "E773", {"start": v(7.99, -0.5) * mm, "end": v(8.52, -0.03) * mm});
            skLineSegment(sketch, "E774", {"start": v(8.52, -0.03) * mm, "end": v(9.05, 0.44) * mm});
            skLineSegment(sketch, "E775", {"start": v(9.05, 0.44) * mm, "end": v(9.56, 0.92) * mm});
            skLineSegment(sketch, "E776", {"start": v(9.56, 0.92) * mm, "end": v(10.07, 1.44) * mm});
            skLineSegment(sketch, "E777", {"start": v(10.07, 1.44) * mm, "end": v(10.56, 2) * mm});
            skLineSegment(sketch, "E778", {"start": v(10.56, 2) * mm, "end": v(11.08, 2.7) * mm});
            skLineSegment(sketch, "E779", {"start": v(11.08, 2.7) * mm, "end": v(11.57, 3.43) * mm});
            skLineSegment(sketch, "E780", {"start": v(11.57, 3.43) * mm, "end": v(12.03, 4.2) * mm});
            skLineSegment(sketch, "E781", {"start": v(12.03, 4.2) * mm, "end": v(12.44, 4.99) * mm});
            skLineSegment(sketch, "E782", {"start": v(12.44, 4.99) * mm, "end": v(12.8, 5.8) * mm});
            skLineSegment(sketch, "E783", {"start": v(12.8, 5.8) * mm, "end": v(13.13, 6.65) * mm});
            skLineSegment(sketch, "E784", {"start": v(13.13, 6.65) * mm, "end": v(13.4, 7.52) * mm});
            skLineSegment(sketch, "E785", {"start": v(13.4, 7.52) * mm, "end": v(13.62, 8.41) * mm});
            skLineSegment(sketch, "E786", {"start": v(13.62, 8.41) * mm, "end": v(13.8, 9.32) * mm});
            skLineSegment(sketch, "E787", {"start": v(13.8, 9.32) * mm, "end": v(13.9, 10.24) * mm});
            skLineSegment(sketch, "E788", {"start": v(13.9, 10.24) * mm, "end": v(13.97, 11.17) * mm});
            skLineSegment(sketch, "E789", {"start": v(13.97, 11.17) * mm, "end": v(13.96, 12.1) * mm});
            skLineSegment(sketch, "E790", {"start": v(13.96, 12.1) * mm, "end": v(13.9, 13.05) * mm});
            skLineSegment(sketch, "E791", {"start": v(13.9, 13.05) * mm, "end": v(13.76, 14) * mm});
            skLineSegment(sketch, "E792", {"start": v(13.76, 14) * mm, "end": v(13.57, 14.95) * mm});
            skLineSegment(sketch, "E793", {"start": v(13.57, 14.95) * mm, "end": v(13.3, 15.9) * mm});
            skLineSegment(sketch, "E794", {"start": v(13.3, 15.9) * mm, "end": v(12.96, 16.84) * mm});
            skLineSegment(sketch, "E795", {"start": v(12.96, 16.84) * mm, "end": v(12.54, 17.78) * mm});
            skLineSegment(sketch, "E796", {"start": v(12.54, 17.78) * mm, "end": v(12.26, 18.32) * mm});
            skLineSegment(sketch, "E797", {"start": v(12.26, 18.32) * mm, "end": v(11.94, 18.87) * mm});
            skLineSegment(sketch, "E798", {"start": v(11.94, 18.87) * mm, "end": v(11.57, 19.42) * mm});
            skLineSegment(sketch, "E799", {"start": v(11.57, 19.42) * mm, "end": v(11.17, 19.97) * mm});
            skLineSegment(sketch, "E800", {"start": v(11.17, 19.97) * mm, "end": v(10.73, 20.51) * mm});
            skLineSegment(sketch, "E801", {"start": v(10.73, 20.51) * mm, "end": v(10.26, 21.05) * mm});
            skLineSegment(sketch, "E802", {"start": v(10.26, 21.05) * mm, "end": v(9.75, 21.57) * mm});
            skLineSegment(sketch, "E803", {"start": v(9.75, 21.57) * mm, "end": v(9.2, 22.08) * mm});
            skLineSegment(sketch, "E804", {"start": v(9.2, 22.08) * mm, "end": v(8.62, 22.57) * mm});
            skLineSegment(sketch, "E805", {"start": v(8.62, 22.57) * mm, "end": v(8, 23.03) * mm});
            skLineSegment(sketch, "E806", {"start": v(8, 23.03) * mm, "end": v(7.37, 23.46) * mm});
            skLineSegment(sketch, "E807", {"start": v(7.37, 23.46) * mm, "end": v(6.7, 23.86) * mm});
            skLineSegment(sketch, "E808", {"start": v(6.7, 23.86) * mm, "end": v(6, 24.23) * mm});
            skLineSegment(sketch, "E809", {"start": v(6, 24.23) * mm, "end": v(5.27, 24.55) * mm});
            skLineSegment(sketch, "E810", {"start": v(5.27, 24.55) * mm, "end": v(4.52, 24.83) * mm});
            skLineSegment(sketch, "E811", {"start": v(4.52, 24.83) * mm, "end": v(3.74, 25.05) * mm});
            skLineSegment(sketch, "E812", {"start": v(3.74, 25.05) * mm, "end": v(2.94, 25.23) * mm});
            skLineSegment(sketch, "E813", {"start": v(2.94, 25.23) * mm, "end": v(2.12, 25.34) * mm});
            skLineSegment(sketch, "E814", {"start": v(2.12, 25.34) * mm, "end": v(1.27, 25.4) * mm});
            skLineSegment(sketch, "E815", {"start": v(1.27, 25.4) * mm, "end": v(0.41, 25.39) * mm});
            skLineSegment(sketch, "E816", {"start": v(0.41, 25.39) * mm, "end": v(-0.47, 25.3) * mm});
            skSolve(sketch);
        }
        {
            var Q0;
            Q0=makeQuery(id+"F0.imprint","IMPRINT",FACE,{"disambiguationData":[TD([[makeQuery(id+"F0.imprint","IMPRINT",EDGE,{"derivedFrom":sQuery(id+"F0.wireOp",EDGE,"E0")}),1.0]])]});
            extrude(context, id + "F1", {"entities" : qUnion([Q0]), "depth" : 3 * mm});
        }
        {
            var Q0;
            Q0=makeQuery(id+"F1.opExtrude","CAP_FACE",FACE,{"disambiguationData":[OSD([sQuery(id+"F0.wireOp",EDGE,"E0"),sQuery(id+"F0.wireOp",EDGE,"E1"),sQuery(id+"F0.wireOp",EDGE,"E2"),sQuery(id+"F0.wireOp",EDGE,"E3"),sQuery(id+"F0.wireOp",EDGE,"E4"),sQuery(id+"F0.wireOp",EDGE,"E5"),sQuery(id+"F0.wireOp",EDGE,"E6"),sQuery(id+"F0.wireOp",EDGE,"E7"),sQuery(id+"F0.wireOp",EDGE,"E8"),sQuery(id+"F0.wireOp",EDGE,"E9"),sQuery(id+"F0.wireOp",EDGE,"E10"),sQuery(id+"F0.wireOp",EDGE,"E11"),sQuery(id+"F0.wireOp",EDGE,"E12"),sQuery(id+"F0.wireOp",EDGE,"E13"),sQuery(id+"F0.wireOp",EDGE,"E14"),sQuery(id+"F0.wireOp",EDGE,"E15"),sQuery(id+"F0.wireOp",EDGE,"E16"),sQuery(id+"F0.wireOp",EDGE,"E17"),sQuery(id+"F0.wireOp",EDGE,"E18"),sQuery(id+"F0.wireOp",EDGE,"E19"),sQuery(id+"F0.wireOp",EDGE,"E20"),sQuery(id+"F0.wireOp",EDGE,"E21"),sQuery(id+"F0.wireOp",EDGE,"E22"),sQuery(id+"F0.wireOp",EDGE,"E23"),sQuery(id+"F0.wireOp",EDGE,"E24"),sQuery(id+"F0.wireOp",EDGE,"E25"),sQuery(id+"F0.wireOp",EDGE,"E26"),sQuery(id+"F0.wireOp",EDGE,"E27"),sQuery(id+"F0.wireOp",EDGE,"E28"),sQuery(id+"F0.wireOp",EDGE,"E29"),sQuery(id+"F0.wireOp",EDGE,"E30"),sQuery(id+"F0.wireOp",EDGE,"E31"),sQuery(id+"F0.wireOp",EDGE,"E32"),sQuery(id+"F0.wireOp",EDGE,"E33"),sQuery(id+"F0.wireOp",EDGE,"E34"),sQuery(id+"F0.wireOp",EDGE,"E35"),sQuery(id+"F0.wireOp",EDGE,"E36"),sQuery(id+"F0.wireOp",EDGE,"E37"),sQuery(id+"F0.wireOp",EDGE,"E38"),sQuery(id+"F0.wireOp",EDGE,"E39"),sQuery(id+"F0.wireOp",EDGE,"E40"),sQuery(id+"F0.wireOp",EDGE,"E41"),sQuery(id+"F0.wireOp",EDGE,"E42"),sQuery(id+"F0.wireOp",EDGE,"E43"),sQuery(id+"F0.wireOp",EDGE,"E44"),sQuery(id+"F0.wireOp",EDGE,"E45"),sQuery(id+"F0.wireOp",EDGE,"E46"),sQuery(id+"F0.wireOp",EDGE,"E47"),sQuery(id+"F0.wireOp",EDGE,"E48"),sQuery(id+"F0.wireOp",EDGE,"E49"),sQuery(id+"F0.wireOp",EDGE,"E50"),sQuery(id+"F0.wireOp",EDGE,"E51"),sQuery(id+"F0.wireOp",EDGE,"E52"),sQuery(id+"F0.wireOp",EDGE,"E53"),sQuery(id+"F0.wireOp",EDGE,"E54"),sQuery(id+"F0.wireOp",EDGE,"E55"),sQuery(id+"F0.wireOp",EDGE,"E56"),sQuery(id+"F0.wireOp",EDGE,"E57"),sQuery(id+"F0.wireOp",EDGE,"E58"),sQuery(id+"F0.wireOp",EDGE,"E59"),sQuery(id+"F0.wireOp",EDGE,"E60"),sQuery(id+"F0.wireOp",EDGE,"E61"),sQuery(id+"F0.wireOp",EDGE,"E62"),sQuery(id+"F0.wireOp",EDGE,"E63"),sQuery(id+"F0.wireOp",EDGE,"E64"),sQuery(id+"F0.wireOp",EDGE,"E65"),sQuery(id+"F0.wireOp",EDGE,"E66"),sQuery(id+"F0.wireOp",EDGE,"E67"),sQuery(id+"F0.wireOp",EDGE,"E68"),sQuery(id+"F0.wireOp",EDGE,"E69"),sQuery(id+"F0.wireOp",EDGE,"E70"),sQuery(id+"F0.wireOp",EDGE,"E71"),sQuery(id+"F0.wireOp",EDGE,"E72"),sQuery(id+"F0.wireOp",EDGE,"E73"),sQuery(id+"F0.wireOp",EDGE,"E74"),sQuery(id+"F0.wireOp",EDGE,"E75"),sQuery(id+"F0.wireOp",EDGE,"E76"),sQuery(id+"F0.wireOp",EDGE,"E77"),sQuery(id+"F0.wireOp",EDGE,"E78"),sQuery(id+"F0.wireOp",EDGE,"E79"),sQuery(id+"F0.wireOp",EDGE,"E80"),sQuery(id+"F0.wireOp",EDGE,"E81"),sQuery(id+"F0.wireOp",EDGE,"E82"),sQuery(id+"F0.wireOp",EDGE,"E83"),sQuery(id+"F0.wireOp",EDGE,"E84"),sQuery(id+"F0.wireOp",EDGE,"E85"),sQuery(id+"F0.wireOp",EDGE,"E86"),sQuery(id+"F0.wireOp",EDGE,"E87"),sQuery(id+"F0.wireOp",EDGE,"E88"),sQuery(id+"F0.wireOp",EDGE,"E89"),sQuery(id+"F0.wireOp",EDGE,"E90"),sQuery(id+"F0.wireOp",EDGE,"E91"),sQuery(id+"F0.wireOp",EDGE,"E92"),sQuery(id+"F0.wireOp",EDGE,"E93"),sQuery(id+"F0.wireOp",EDGE,"E94"),sQuery(id+"F0.wireOp",EDGE,"E95"),sQuery(id+"F0.wireOp",EDGE,"E96"),sQuery(id+"F0.wireOp",EDGE,"E97"),sQuery(id+"F0.wireOp",EDGE,"E98"),sQuery(id+"F0.wireOp",EDGE,"E99"),sQuery(id+"F0.wireOp",EDGE,"E100"),sQuery(id+"F0.wireOp",EDGE,"E101"),sQuery(id+"F0.wireOp",EDGE,"E102"),sQuery(id+"F0.wireOp",EDGE,"E103"),sQuery(id+"F0.wireOp",EDGE,"E104"),sQuery(id+"F0.wireOp",EDGE,"E105"),sQuery(id+"F0.wireOp",EDGE,"E106"),sQuery(id+"F0.wireOp",EDGE,"E107"),sQuery(id+"F0.wireOp",EDGE,"E108"),sQuery(id+"F0.wireOp",EDGE,"E109"),sQuery(id+"F0.wireOp",EDGE,"E110"),sQuery(id+"F0.wireOp",EDGE,"E111"),sQuery(id+"F0.wireOp",EDGE,"E112"),sQuery(id+"F0.wireOp",EDGE,"E113"),sQuery(id+"F0.wireOp",EDGE,"E114"),sQuery(id+"F0.wireOp",EDGE,"E115"),sQuery(id+"F0.wireOp",EDGE,"E116"),sQuery(id+"F0.wireOp",EDGE,"E117"),sQuery(id+"F0.wireOp",EDGE,"E118"),sQuery(id+"F0.wireOp",EDGE,"E119"),sQuery(id+"F0.wireOp",EDGE,"E120"),sQuery(id+"F0.wireOp",EDGE,"E121"),sQuery(id+"F0.wireOp",EDGE,"E122"),sQuery(id+"F0.wireOp",EDGE,"E123"),sQuery(id+"F0.wireOp",EDGE,"E124"),sQuery(id+"F0.wireOp",EDGE,"E125"),sQuery(id+"F0.wireOp",EDGE,"E126"),sQuery(id+"F0.wireOp",EDGE,"E127"),sQuery(id+"F0.wireOp",EDGE,"E128"),sQuery(id+"F0.wireOp",EDGE,"E129"),sQuery(id+"F0.wireOp",EDGE,"E130"),sQuery(id+"F0.wireOp",EDGE,"E131"),sQuery(id+"F0.wireOp",EDGE,"E132"),sQuery(id+"F0.wireOp",EDGE,"E133"),sQuery(id+"F0.wireOp",EDGE,"E134"),sQuery(id+"F0.wireOp",EDGE,"E135"),sQuery(id+"F0.wireOp",EDGE,"E136"),sQuery(id+"F0.wireOp",EDGE,"E137"),sQuery(id+"F0.wireOp",EDGE,"E138"),sQuery(id+"F0.wireOp",EDGE,"E139"),sQuery(id+"F0.wireOp",EDGE,"E140"),sQuery(id+"F0.wireOp",EDGE,"E141"),sQuery(id+"F0.wireOp",EDGE,"E142"),sQuery(id+"F0.wireOp",EDGE,"E143"),sQuery(id+"F0.wireOp",EDGE,"E144"),sQuery(id+"F0.wireOp",EDGE,"E145"),sQuery(id+"F0.wireOp",EDGE,"E146"),sQuery(id+"F0.wireOp",EDGE,"E147"),sQuery(id+"F0.wireOp",EDGE,"E148"),sQuery(id+"F0.wireOp",EDGE,"E149"),sQuery(id+"F0.wireOp",EDGE,"E150"),sQuery(id+"F0.wireOp",EDGE,"E151"),sQuery(id+"F0.wireOp",EDGE,"E152"),sQuery(id+"F0.wireOp",EDGE,"E153"),sQuery(id+"F0.wireOp",EDGE,"E154"),sQuery(id+"F0.wireOp",EDGE,"E155"),sQuery(id+"F0.wireOp",EDGE,"E156"),sQuery(id+"F0.wireOp",EDGE,"E157"),sQuery(id+"F0.wireOp",EDGE,"E158"),sQuery(id+"F0.wireOp",EDGE,"E159"),sQuery(id+"F0.wireOp",EDGE,"E160"),sQuery(id+"F0.wireOp",EDGE,"E161"),sQuery(id+"F0.wireOp",EDGE,"E162"),sQuery(id+"F0.wireOp",EDGE,"E163"),sQuery(id+"F0.wireOp",EDGE,"E164"),sQuery(id+"F0.wireOp",EDGE,"E165"),sQuery(id+"F0.wireOp",EDGE,"E166"),sQuery(id+"F0.wireOp",EDGE,"E167"),sQuery(id+"F0.wireOp",EDGE,"E168"),sQuery(id+"F0.wireOp",EDGE,"E169"),sQuery(id+"F0.wireOp",EDGE,"E170"),sQuery(id+"F0.wireOp",EDGE,"E171"),sQuery(id+"F0.wireOp",EDGE,"E172"),sQuery(id+"F0.wireOp",EDGE,"E173"),sQuery(id+"F0.wireOp",EDGE,"E174"),sQuery(id+"F0.wireOp",EDGE,"E175"),sQuery(id+"F0.wireOp",EDGE,"E176"),sQuery(id+"F0.wireOp",EDGE,"E177"),sQuery(id+"F0.wireOp",EDGE,"E178"),sQuery(id+"F0.wireOp",EDGE,"E179"),sQuery(id+"F0.wireOp",EDGE,"E180"),sQuery(id+"F0.wireOp",EDGE,"E181"),sQuery(id+"F0.wireOp",EDGE,"E182"),sQuery(id+"F0.wireOp",EDGE,"E183"),sQuery(id+"F0.wireOp",EDGE,"E184"),sQuery(id+"F0.wireOp",EDGE,"E185"),sQuery(id+"F0.wireOp",EDGE,"E186"),sQuery(id+"F0.wireOp",EDGE,"E187"),sQuery(id+"F0.wireOp",EDGE,"E188"),sQuery(id+"F0.wireOp",EDGE,"E189"),sQuery(id+"F0.wireOp",EDGE,"E190"),sQuery(id+"F0.wireOp",EDGE,"E191"),sQuery(id+"F0.wireOp",EDGE,"E192"),sQuery(id+"F0.wireOp",EDGE,"E193"),sQuery(id+"F0.wireOp",EDGE,"E194"),sQuery(id+"F0.wireOp",EDGE,"E195"),sQuery(id+"F0.wireOp",EDGE,"E196"),sQuery(id+"F0.wireOp",EDGE,"E197"),sQuery(id+"F0.wireOp",EDGE,"E198"),sQuery(id+"F0.wireOp",EDGE,"E199"),sQuery(id+"F0.wireOp",EDGE,"E200"),sQuery(id+"F0.wireOp",EDGE,"E201"),sQuery(id+"F0.wireOp",EDGE,"E202"),sQuery(id+"F0.wireOp",EDGE,"E203"),sQuery(id+"F0.wireOp",EDGE,"E204"),sQuery(id+"F0.wireOp",EDGE,"E205"),sQuery(id+"F0.wireOp",EDGE,"E206"),sQuery(id+"F0.wireOp",EDGE,"E207"),sQuery(id+"F0.wireOp",EDGE,"E208"),sQuery(id+"F0.wireOp",EDGE,"E209"),sQuery(id+"F0.wireOp",EDGE,"E210"),sQuery(id+"F0.wireOp",EDGE,"E211"),sQuery(id+"F0.wireOp",EDGE,"E212"),sQuery(id+"F0.wireOp",EDGE,"E213"),sQuery(id+"F0.wireOp",EDGE,"E214"),sQuery(id+"F0.wireOp",EDGE,"E215"),sQuery(id+"F0.wireOp",EDGE,"E216"),sQuery(id+"F0.wireOp",EDGE,"E217"),sQuery(id+"F0.wireOp",EDGE,"E218"),sQuery(id+"F0.wireOp",EDGE,"E219"),sQuery(id+"F0.wireOp",EDGE,"E220"),sQuery(id+"F0.wireOp",EDGE,"E221"),sQuery(id+"F0.wireOp",EDGE,"E222"),sQuery(id+"F0.wireOp",EDGE,"E223"),sQuery(id+"F0.wireOp",EDGE,"E224"),sQuery(id+"F0.wireOp",EDGE,"E225"),sQuery(id+"F0.wireOp",EDGE,"E226"),sQuery(id+"F0.wireOp",EDGE,"E227"),sQuery(id+"F0.wireOp",EDGE,"E228"),sQuery(id+"F0.wireOp",EDGE,"E229"),sQuery(id+"F0.wireOp",EDGE,"E230"),sQuery(id+"F0.wireOp",EDGE,"E231"),sQuery(id+"F0.wireOp",EDGE,"E232"),sQuery(id+"F0.wireOp",EDGE,"E233"),sQuery(id+"F0.wireOp",EDGE,"E234"),sQuery(id+"F0.wireOp",EDGE,"E235"),sQuery(id+"F0.wireOp",EDGE,"E236"),sQuery(id+"F0.wireOp",EDGE,"E237"),sQuery(id+"F0.wireOp",EDGE,"E238"),sQuery(id+"F0.wireOp",EDGE,"E239"),sQuery(id+"F0.wireOp",EDGE,"E240"),sQuery(id+"F0.wireOp",EDGE,"E241"),sQuery(id+"F0.wireOp",EDGE,"E242"),sQuery(id+"F0.wireOp",EDGE,"E243"),sQuery(id+"F0.wireOp",EDGE,"E244"),sQuery(id+"F0.wireOp",EDGE,"E245"),sQuery(id+"F0.wireOp",EDGE,"E246"),sQuery(id+"F0.wireOp",EDGE,"E247"),sQuery(id+"F0.wireOp",EDGE,"E248"),sQuery(id+"F0.wireOp",EDGE,"E249"),sQuery(id+"F0.wireOp",EDGE,"E250"),sQuery(id+"F0.wireOp",EDGE,"E251"),sQuery(id+"F0.wireOp",EDGE,"E252"),sQuery(id+"F0.wireOp",EDGE,"E253"),sQuery(id+"F0.wireOp",EDGE,"E254"),sQuery(id+"F0.wireOp",EDGE,"E255"),sQuery(id+"F0.wireOp",EDGE,"E256"),sQuery(id+"F0.wireOp",EDGE,"E257"),sQuery(id+"F0.wireOp",EDGE,"E258"),sQuery(id+"F0.wireOp",EDGE,"E259"),sQuery(id+"F0.wireOp",EDGE,"E260"),sQuery(id+"F0.wireOp",EDGE,"E261"),sQuery(id+"F0.wireOp",EDGE,"E262"),sQuery(id+"F0.wireOp",EDGE,"E263"),sQuery(id+"F0.wireOp",EDGE,"E264"),sQuery(id+"F0.wireOp",EDGE,"E265"),sQuery(id+"F0.wireOp",EDGE,"E266"),sQuery(id+"F0.wireOp",EDGE,"E267"),sQuery(id+"F0.wireOp",EDGE,"E268"),sQuery(id+"F0.wireOp",EDGE,"E269"),sQuery(id+"F0.wireOp",EDGE,"E270"),sQuery(id+"F0.wireOp",EDGE,"E271"),sQuery(id+"F0.wireOp",EDGE,"E272"),sQuery(id+"F0.wireOp",EDGE,"E273"),sQuery(id+"F0.wireOp",EDGE,"E274"),sQuery(id+"F0.wireOp",EDGE,"E275"),sQuery(id+"F0.wireOp",EDGE,"E276"),sQuery(id+"F0.wireOp",EDGE,"E277"),sQuery(id+"F0.wireOp",EDGE,"E278"),sQuery(id+"F0.wireOp",EDGE,"E279"),sQuery(id+"F0.wireOp",EDGE,"E280"),sQuery(id+"F0.wireOp",EDGE,"E281"),sQuery(id+"F0.wireOp",EDGE,"E282"),sQuery(id+"F0.wireOp",EDGE,"E283"),sQuery(id+"F0.wireOp",EDGE,"E284"),sQuery(id+"F0.wireOp",EDGE,"E285"),sQuery(id+"F0.wireOp",EDGE,"E286"),sQuery(id+"F0.wireOp",EDGE,"E287"),sQuery(id+"F0.wireOp",EDGE,"E288"),sQuery(id+"F0.wireOp",EDGE,"E289"),sQuery(id+"F0.wireOp",EDGE,"E290"),sQuery(id+"F0.wireOp",EDGE,"E291"),sQuery(id+"F0.wireOp",EDGE,"E292"),sQuery(id+"F0.wireOp",EDGE,"E293"),sQuery(id+"F0.wireOp",EDGE,"E294"),sQuery(id+"F0.wireOp",EDGE,"E295"),sQuery(id+"F0.wireOp",EDGE,"E296"),sQuery(id+"F0.wireOp",EDGE,"E297"),sQuery(id+"F0.wireOp",EDGE,"E298"),sQuery(id+"F0.wireOp",EDGE,"E299"),sQuery(id+"F0.wireOp",EDGE,"E300"),sQuery(id+"F0.wireOp",EDGE,"E301"),sQuery(id+"F0.wireOp",EDGE,"E302"),sQuery(id+"F0.wireOp",EDGE,"E303"),sQuery(id+"F0.wireOp",EDGE,"E304"),sQuery(id+"F0.wireOp",EDGE,"E305"),sQuery(id+"F0.wireOp",EDGE,"E306"),sQuery(id+"F0.wireOp",EDGE,"E307"),sQuery(id+"F0.wireOp",EDGE,"E308"),sQuery(id+"F0.wireOp",EDGE,"E309"),sQuery(id+"F0.wireOp",EDGE,"E310"),sQuery(id+"F0.wireOp",EDGE,"E311"),sQuery(id+"F0.wireOp",EDGE,"E312"),sQuery(id+"F0.wireOp",EDGE,"E313"),sQuery(id+"F0.wireOp",EDGE,"E314"),sQuery(id+"F0.wireOp",EDGE,"E315"),sQuery(id+"F0.wireOp",EDGE,"E316"),sQuery(id+"F0.wireOp",EDGE,"E317"),sQuery(id+"F0.wireOp",EDGE,"E318"),sQuery(id+"F0.wireOp",EDGE,"E319"),sQuery(id+"F0.wireOp",EDGE,"E320"),sQuery(id+"F0.wireOp",EDGE,"E321"),sQuery(id+"F0.wireOp",EDGE,"E322"),sQuery(id+"F0.wireOp",EDGE,"E323"),sQuery(id+"F0.wireOp",EDGE,"E324"),sQuery(id+"F0.wireOp",EDGE,"E325"),sQuery(id+"F0.wireOp",EDGE,"E326"),sQuery(id+"F0.wireOp",EDGE,"E327"),sQuery(id+"F0.wireOp",EDGE,"E328"),sQuery(id+"F0.wireOp",EDGE,"E329"),sQuery(id+"F0.wireOp",EDGE,"E330"),sQuery(id+"F0.wireOp",EDGE,"E331"),sQuery(id+"F0.wireOp",EDGE,"E332"),sQuery(id+"F0.wireOp",EDGE,"E333"),sQuery(id+"F0.wireOp",EDGE,"E334"),sQuery(id+"F0.wireOp",EDGE,"E335"),sQuery(id+"F0.wireOp",EDGE,"E336"),sQuery(id+"F0.wireOp",EDGE,"E337"),sQuery(id+"F0.wireOp",EDGE,"E338"),sQuery(id+"F0.wireOp",EDGE,"E339"),sQuery(id+"F0.wireOp",EDGE,"E340"),sQuery(id+"F0.wireOp",EDGE,"E341"),sQuery(id+"F0.wireOp",EDGE,"E342"),sQuery(id+"F0.wireOp",EDGE,"E343"),sQuery(id+"F0.wireOp",EDGE,"E344"),sQuery(id+"F0.wireOp",EDGE,"E345"),sQuery(id+"F0.wireOp",EDGE,"E346"),sQuery(id+"F0.wireOp",EDGE,"E347"),sQuery(id+"F0.wireOp",EDGE,"E348"),sQuery(id+"F0.wireOp",EDGE,"E349"),sQuery(id+"F0.wireOp",EDGE,"E350"),sQuery(id+"F0.wireOp",EDGE,"E351"),sQuery(id+"F0.wireOp",EDGE,"E352"),sQuery(id+"F0.wireOp",EDGE,"E353"),sQuery(id+"F0.wireOp",EDGE,"E354"),sQuery(id+"F0.wireOp",EDGE,"E355"),sQuery(id+"F0.wireOp",EDGE,"E356"),sQuery(id+"F0.wireOp",EDGE,"E357"),sQuery(id+"F0.wireOp",EDGE,"E358"),sQuery(id+"F0.wireOp",EDGE,"E359"),sQuery(id+"F0.wireOp",EDGE,"E360"),sQuery(id+"F0.wireOp",EDGE,"E361"),sQuery(id+"F0.wireOp",EDGE,"E362"),sQuery(id+"F0.wireOp",EDGE,"E363"),sQuery(id+"F0.wireOp",EDGE,"E364"),sQuery(id+"F0.wireOp",EDGE,"E365"),sQuery(id+"F0.wireOp",EDGE,"E366"),sQuery(id+"F0.wireOp",EDGE,"E367"),sQuery(id+"F0.wireOp",EDGE,"E368"),sQuery(id+"F0.wireOp",EDGE,"E369"),sQuery(id+"F0.wireOp",EDGE,"E370"),sQuery(id+"F0.wireOp",EDGE,"E371"),sQuery(id+"F0.wireOp",EDGE,"E372"),sQuery(id+"F0.wireOp",EDGE,"E373"),sQuery(id+"F0.wireOp",EDGE,"E374"),sQuery(id+"F0.wireOp",EDGE,"E375"),sQuery(id+"F0.wireOp",EDGE,"E376"),sQuery(id+"F0.wireOp",EDGE,"E377"),sQuery(id+"F0.wireOp",EDGE,"E378"),sQuery(id+"F0.wireOp",EDGE,"E379"),sQuery(id+"F0.wireOp",EDGE,"E380"),sQuery(id+"F0.wireOp",EDGE,"E381"),sQuery(id+"F0.wireOp",EDGE,"E382"),sQuery(id+"F0.wireOp",EDGE,"E383"),sQuery(id+"F0.wireOp",EDGE,"E384"),sQuery(id+"F0.wireOp",EDGE,"E385"),sQuery(id+"F0.wireOp",EDGE,"E386"),sQuery(id+"F0.wireOp",EDGE,"E387"),sQuery(id+"F0.wireOp",EDGE,"E388"),sQuery(id+"F0.wireOp",EDGE,"E389"),sQuery(id+"F0.wireOp",EDGE,"E390"),sQuery(id+"F0.wireOp",EDGE,"E391"),sQuery(id+"F0.wireOp",EDGE,"E392"),sQuery(id+"F0.wireOp",EDGE,"E393"),sQuery(id+"F0.wireOp",EDGE,"E394"),sQuery(id+"F0.wireOp",EDGE,"E395"),sQuery(id+"F0.wireOp",EDGE,"E396"),sQuery(id+"F0.wireOp",EDGE,"E397"),sQuery(id+"F0.wireOp",EDGE,"E398"),sQuery(id+"F0.wireOp",EDGE,"E399"),sQuery(id+"F0.wireOp",EDGE,"E400"),sQuery(id+"F0.wireOp",EDGE,"E401"),sQuery(id+"F0.wireOp",EDGE,"E402"),sQuery(id+"F0.wireOp",EDGE,"E403"),sQuery(id+"F0.wireOp",EDGE,"E404"),sQuery(id+"F0.wireOp",EDGE,"E405"),sQuery(id+"F0.wireOp",EDGE,"E406"),sQuery(id+"F0.wireOp",EDGE,"E407"),sQuery(id+"F0.wireOp",EDGE,"E408"),sQuery(id+"F0.wireOp",EDGE,"E409"),sQuery(id+"F0.wireOp",EDGE,"E410"),sQuery(id+"F0.wireOp",EDGE,"E411"),sQuery(id+"F0.wireOp",EDGE,"E412"),sQuery(id+"F0.wireOp",EDGE,"E413"),sQuery(id+"F0.wireOp",EDGE,"E414"),sQuery(id+"F0.wireOp",EDGE,"E415"),sQuery(id+"F0.wireOp",EDGE,"E416"),sQuery(id+"F0.wireOp",EDGE,"E417"),sQuery(id+"F0.wireOp",EDGE,"E418"),sQuery(id+"F0.wireOp",EDGE,"E419"),sQuery(id+"F0.wireOp",EDGE,"E420"),sQuery(id+"F0.wireOp",EDGE,"E421"),sQuery(id+"F0.wireOp",EDGE,"E422"),sQuery(id+"F0.wireOp",EDGE,"E423"),sQuery(id+"F0.wireOp",EDGE,"E424"),sQuery(id+"F0.wireOp",EDGE,"E425"),sQuery(id+"F0.wireOp",EDGE,"E426"),sQuery(id+"F0.wireOp",EDGE,"E427"),sQuery(id+"F0.wireOp",EDGE,"E428"),sQuery(id+"F0.wireOp",EDGE,"E429"),sQuery(id+"F0.wireOp",EDGE,"E430"),sQuery(id+"F0.wireOp",EDGE,"E431"),sQuery(id+"F0.wireOp",EDGE,"E432"),sQuery(id+"F0.wireOp",EDGE,"E433"),sQuery(id+"F0.wireOp",EDGE,"E434"),sQuery(id+"F0.wireOp",EDGE,"E435"),sQuery(id+"F0.wireOp",EDGE,"E436"),sQuery(id+"F0.wireOp",EDGE,"E437"),sQuery(id+"F0.wireOp",EDGE,"E438"),sQuery(id+"F0.wireOp",EDGE,"E439"),sQuery(id+"F0.wireOp",EDGE,"E440"),sQuery(id+"F0.wireOp",EDGE,"E441"),sQuery(id+"F0.wireOp",EDGE,"E442"),sQuery(id+"F0.wireOp",EDGE,"E443"),sQuery(id+"F0.wireOp",EDGE,"E444"),sQuery(id+"F0.wireOp",EDGE,"E445"),sQuery(id+"F0.wireOp",EDGE,"E446"),sQuery(id+"F0.wireOp",EDGE,"E447"),sQuery(id+"F0.wireOp",EDGE,"E448"),sQuery(id+"F0.wireOp",EDGE,"E449"),sQuery(id+"F0.wireOp",EDGE,"E450"),sQuery(id+"F0.wireOp",EDGE,"E451"),sQuery(id+"F0.wireOp",EDGE,"E452"),sQuery(id+"F0.wireOp",EDGE,"E453"),sQuery(id+"F0.wireOp",EDGE,"E454"),sQuery(id+"F0.wireOp",EDGE,"E455"),sQuery(id+"F0.wireOp",EDGE,"E456"),sQuery(id+"F0.wireOp",EDGE,"E457"),sQuery(id+"F0.wireOp",EDGE,"E458"),sQuery(id+"F0.wireOp",EDGE,"E459"),sQuery(id+"F0.wireOp",EDGE,"E460"),sQuery(id+"F0.wireOp",EDGE,"E461"),sQuery(id+"F0.wireOp",EDGE,"E462"),sQuery(id+"F0.wireOp",EDGE,"E463"),sQuery(id+"F0.wireOp",EDGE,"E464"),sQuery(id+"F0.wireOp",EDGE,"E465"),sQuery(id+"F0.wireOp",EDGE,"E466"),sQuery(id+"F0.wireOp",EDGE,"E467"),sQuery(id+"F0.wireOp",EDGE,"E468"),sQuery(id+"F0.wireOp",EDGE,"E469"),sQuery(id+"F0.wireOp",EDGE,"E470"),sQuery(id+"F0.wireOp",EDGE,"E471"),sQuery(id+"F0.wireOp",EDGE,"E472"),sQuery(id+"F0.wireOp",EDGE,"E473"),sQuery(id+"F0.wireOp",EDGE,"E474"),sQuery(id+"F0.wireOp",EDGE,"E475"),sQuery(id+"F0.wireOp",EDGE,"E476"),sQuery(id+"F0.wireOp",EDGE,"E477"),sQuery(id+"F0.wireOp",EDGE,"E478"),sQuery(id+"F0.wireOp",EDGE,"E479"),sQuery(id+"F0.wireOp",EDGE,"E480"),sQuery(id+"F0.wireOp",EDGE,"E481"),sQuery(id+"F0.wireOp",EDGE,"E482"),sQuery(id+"F0.wireOp",EDGE,"E483"),sQuery(id+"F0.wireOp",EDGE,"E484"),sQuery(id+"F0.wireOp",EDGE,"E485"),sQuery(id+"F0.wireOp",EDGE,"E486"),sQuery(id+"F0.wireOp",EDGE,"E487"),sQuery(id+"F0.wireOp",EDGE,"E488"),sQuery(id+"F0.wireOp",EDGE,"E489"),sQuery(id+"F0.wireOp",EDGE,"E490"),sQuery(id+"F0.wireOp",EDGE,"E491"),sQuery(id+"F0.wireOp",EDGE,"E492"),sQuery(id+"F0.wireOp",EDGE,"E493"),sQuery(id+"F0.wireOp",EDGE,"E494"),sQuery(id+"F0.wireOp",EDGE,"E495"),sQuery(id+"F0.wireOp",EDGE,"E496"),sQuery(id+"F0.wireOp",EDGE,"E497"),sQuery(id+"F0.wireOp",EDGE,"E498"),sQuery(id+"F0.wireOp",EDGE,"E499"),sQuery(id+"F0.wireOp",EDGE,"E500"),sQuery(id+"F0.wireOp",EDGE,"E501"),sQuery(id+"F0.wireOp",EDGE,"E502"),sQuery(id+"F0.wireOp",EDGE,"E503"),sQuery(id+"F0.wireOp",EDGE,"E504"),sQuery(id+"F0.wireOp",EDGE,"E505"),sQuery(id+"F0.wireOp",EDGE,"E506"),sQuery(id+"F0.wireOp",EDGE,"E507"),sQuery(id+"F0.wireOp",EDGE,"E508"),sQuery(id+"F0.wireOp",EDGE,"E509"),sQuery(id+"F0.wireOp",EDGE,"E510"),sQuery(id+"F0.wireOp",EDGE,"E511"),sQuery(id+"F0.wireOp",EDGE,"E512"),sQuery(id+"F0.wireOp",EDGE,"E513"),sQuery(id+"F0.wireOp",EDGE,"E514"),sQuery(id+"F0.wireOp",EDGE,"E515"),sQuery(id+"F0.wireOp",EDGE,"E516"),sQuery(id+"F0.wireOp",EDGE,"E517"),sQuery(id+"F0.wireOp",EDGE,"E518"),sQuery(id+"F0.wireOp",EDGE,"E519"),sQuery(id+"F0.wireOp",EDGE,"E520"),sQuery(id+"F0.wireOp",EDGE,"E521"),sQuery(id+"F0.wireOp",EDGE,"E522"),sQuery(id+"F0.wireOp",EDGE,"E523"),sQuery(id+"F0.wireOp",EDGE,"E524"),sQuery(id+"F0.wireOp",EDGE,"E525"),sQuery(id+"F0.wireOp",EDGE,"E526"),sQuery(id+"F0.wireOp",EDGE,"E527"),sQuery(id+"F0.wireOp",EDGE,"E528"),sQuery(id+"F0.wireOp",EDGE,"E529"),sQuery(id+"F0.wireOp",EDGE,"E530"),sQuery(id+"F0.wireOp",EDGE,"E531"),sQuery(id+"F0.wireOp",EDGE,"E532"),sQuery(id+"F0.wireOp",EDGE,"E533"),sQuery(id+"F0.wireOp",EDGE,"E534"),sQuery(id+"F0.wireOp",EDGE,"E535"),sQuery(id+"F0.wireOp",EDGE,"E536"),sQuery(id+"F0.wireOp",EDGE,"E537"),sQuery(id+"F0.wireOp",EDGE,"E538"),sQuery(id+"F0.wireOp",EDGE,"E539"),sQuery(id+"F0.wireOp",EDGE,"E540"),sQuery(id+"F0.wireOp",EDGE,"E541"),sQuery(id+"F0.wireOp",EDGE,"E542"),sQuery(id+"F0.wireOp",EDGE,"E543"),sQuery(id+"F0.wireOp",EDGE,"E544"),sQuery(id+"F0.wireOp",EDGE,"E545"),sQuery(id+"F0.wireOp",EDGE,"E546"),sQuery(id+"F0.wireOp",EDGE,"E547"),sQuery(id+"F0.wireOp",EDGE,"E548"),sQuery(id+"F0.wireOp",EDGE,"E549"),sQuery(id+"F0.wireOp",EDGE,"E550"),sQuery(id+"F0.wireOp",EDGE,"E551"),sQuery(id+"F0.wireOp",EDGE,"E552"),sQuery(id+"F0.wireOp",EDGE,"E553"),sQuery(id+"F0.wireOp",EDGE,"E554"),sQuery(id+"F0.wireOp",EDGE,"E555"),sQuery(id+"F0.wireOp",EDGE,"E556"),sQuery(id+"F0.wireOp",EDGE,"E557"),sQuery(id+"F0.wireOp",EDGE,"E558"),sQuery(id+"F0.wireOp",EDGE,"E559"),sQuery(id+"F0.wireOp",EDGE,"E560"),sQuery(id+"F0.wireOp",EDGE,"E561"),sQuery(id+"F0.wireOp",EDGE,"E562"),sQuery(id+"F0.wireOp",EDGE,"E563"),sQuery(id+"F0.wireOp",EDGE,"E564"),sQuery(id+"F0.wireOp",EDGE,"E565"),sQuery(id+"F0.wireOp",EDGE,"E566"),sQuery(id+"F0.wireOp",EDGE,"E567"),sQuery(id+"F0.wireOp",EDGE,"E568"),sQuery(id+"F0.wireOp",EDGE,"E569"),sQuery(id+"F0.wireOp",EDGE,"E570"),sQuery(id+"F0.wireOp",EDGE,"E571"),sQuery(id+"F0.wireOp",EDGE,"E572"),sQuery(id+"F0.wireOp",EDGE,"E573"),sQuery(id+"F0.wireOp",EDGE,"E574"),sQuery(id+"F0.wireOp",EDGE,"E575"),sQuery(id+"F0.wireOp",EDGE,"E576"),sQuery(id+"F0.wireOp",EDGE,"E577"),sQuery(id+"F0.wireOp",EDGE,"E578"),sQuery(id+"F0.wireOp",EDGE,"E579"),sQuery(id+"F0.wireOp",EDGE,"E580"),sQuery(id+"F0.wireOp",EDGE,"E581"),sQuery(id+"F0.wireOp",EDGE,"E582"),sQuery(id+"F0.wireOp",EDGE,"E583"),sQuery(id+"F0.wireOp",EDGE,"E584"),sQuery(id+"F0.wireOp",EDGE,"E585"),sQuery(id+"F0.wireOp",EDGE,"E586"),sQuery(id+"F0.wireOp",EDGE,"E587"),sQuery(id+"F0.wireOp",EDGE,"E588"),sQuery(id+"F0.wireOp",EDGE,"E589"),sQuery(id+"F0.wireOp",EDGE,"E590"),sQuery(id+"F0.wireOp",EDGE,"E591"),sQuery(id+"F0.wireOp",EDGE,"E592"),sQuery(id+"F0.wireOp",EDGE,"E593"),sQuery(id+"F0.wireOp",EDGE,"E594"),sQuery(id+"F0.wireOp",EDGE,"E595"),sQuery(id+"F0.wireOp",EDGE,"E596"),sQuery(id+"F0.wireOp",EDGE,"E597"),sQuery(id+"F0.wireOp",EDGE,"E598"),sQuery(id+"F0.wireOp",EDGE,"E599"),sQuery(id+"F0.wireOp",EDGE,"E600"),sQuery(id+"F0.wireOp",EDGE,"E601"),sQuery(id+"F0.wireOp",EDGE,"E602"),sQuery(id+"F0.wireOp",EDGE,"E603"),sQuery(id+"F0.wireOp",EDGE,"E604"),sQuery(id+"F0.wireOp",EDGE,"E605"),sQuery(id+"F0.wireOp",EDGE,"E606"),sQuery(id+"F0.wireOp",EDGE,"E607"),sQuery(id+"F0.wireOp",EDGE,"E608"),sQuery(id+"F0.wireOp",EDGE,"E609"),sQuery(id+"F0.wireOp",EDGE,"E610"),sQuery(id+"F0.wireOp",EDGE,"E611"),sQuery(id+"F0.wireOp",EDGE,"E612"),sQuery(id+"F0.wireOp",EDGE,"E613"),sQuery(id+"F0.wireOp",EDGE,"E614"),sQuery(id+"F0.wireOp",EDGE,"E615"),sQuery(id+"F0.wireOp",EDGE,"E616"),sQuery(id+"F0.wireOp",EDGE,"E617"),sQuery(id+"F0.wireOp",EDGE,"E618"),sQuery(id+"F0.wireOp",EDGE,"E619"),sQuery(id+"F0.wireOp",EDGE,"E620"),sQuery(id+"F0.wireOp",EDGE,"E621"),sQuery(id+"F0.wireOp",EDGE,"E622"),sQuery(id+"F0.wireOp",EDGE,"E623"),sQuery(id+"F0.wireOp",EDGE,"E624"),sQuery(id+"F0.wireOp",EDGE,"E625"),sQuery(id+"F0.wireOp",EDGE,"E626"),sQuery(id+"F0.wireOp",EDGE,"E627"),sQuery(id+"F0.wireOp",EDGE,"E628"),sQuery(id+"F0.wireOp",EDGE,"E629"),sQuery(id+"F0.wireOp",EDGE,"E630"),sQuery(id+"F0.wireOp",EDGE,"E631"),sQuery(id+"F0.wireOp",EDGE,"E632"),sQuery(id+"F0.wireOp",EDGE,"E633"),sQuery(id+"F0.wireOp",EDGE,"E634"),sQuery(id+"F0.wireOp",EDGE,"E635"),sQuery(id+"F0.wireOp",EDGE,"E636"),sQuery(id+"F0.wireOp",EDGE,"E637"),sQuery(id+"F0.wireOp",EDGE,"E638"),sQuery(id+"F0.wireOp",EDGE,"E639"),sQuery(id+"F0.wireOp",EDGE,"E640"),sQuery(id+"F0.wireOp",EDGE,"E641"),sQuery(id+"F0.wireOp",EDGE,"E642"),sQuery(id+"F0.wireOp",EDGE,"E643"),sQuery(id+"F0.wireOp",EDGE,"E644"),sQuery(id+"F0.wireOp",EDGE,"E645"),sQuery(id+"F0.wireOp",EDGE,"E646"),sQuery(id+"F0.wireOp",EDGE,"E647"),sQuery(id+"F0.wireOp",EDGE,"E648"),sQuery(id+"F0.wireOp",EDGE,"E649"),sQuery(id+"F0.wireOp",EDGE,"E650"),sQuery(id+"F0.wireOp",EDGE,"E651"),sQuery(id+"F0.wireOp",EDGE,"E652"),sQuery(id+"F0.wireOp",EDGE,"E653"),sQuery(id+"F0.wireOp",EDGE,"E654"),sQuery(id+"F0.wireOp",EDGE,"E655"),sQuery(id+"F0.wireOp",EDGE,"E656"),sQuery(id+"F0.wireOp",EDGE,"E657"),sQuery(id+"F0.wireOp",EDGE,"E658"),sQuery(id+"F0.wireOp",EDGE,"E659"),sQuery(id+"F0.wireOp",EDGE,"E660"),sQuery(id+"F0.wireOp",EDGE,"E661"),sQuery(id+"F0.wireOp",EDGE,"E662"),sQuery(id+"F0.wireOp",EDGE,"E663"),sQuery(id+"F0.wireOp",EDGE,"E664"),sQuery(id+"F0.wireOp",EDGE,"E665"),sQuery(id+"F0.wireOp",EDGE,"E666"),sQuery(id+"F0.wireOp",EDGE,"E667"),sQuery(id+"F0.wireOp",EDGE,"E668"),sQuery(id+"F0.wireOp",EDGE,"E669"),sQuery(id+"F0.wireOp",EDGE,"E670"),sQuery(id+"F0.wireOp",EDGE,"E671"),sQuery(id+"F0.wireOp",EDGE,"E672"),sQuery(id+"F0.wireOp",EDGE,"E673"),sQuery(id+"F0.wireOp",EDGE,"E674"),sQuery(id+"F0.wireOp",EDGE,"E675"),sQuery(id+"F0.wireOp",EDGE,"E676"),sQuery(id+"F0.wireOp",EDGE,"E677"),sQuery(id+"F0.wireOp",EDGE,"E678"),sQuery(id+"F0.wireOp",EDGE,"E679"),sQuery(id+"F0.wireOp",EDGE,"E680"),sQuery(id+"F0.wireOp",EDGE,"E681"),sQuery(id+"F0.wireOp",EDGE,"E682"),sQuery(id+"F0.wireOp",EDGE,"E683"),sQuery(id+"F0.wireOp",EDGE,"E684"),sQuery(id+"F0.wireOp",EDGE,"E685"),sQuery(id+"F0.wireOp",EDGE,"E686"),sQuery(id+"F0.wireOp",EDGE,"E687"),sQuery(id+"F0.wireOp",EDGE,"E688"),sQuery(id+"F0.wireOp",EDGE,"E689"),sQuery(id+"F0.wireOp",EDGE,"E690"),sQuery(id+"F0.wireOp",EDGE,"E691"),sQuery(id+"F0.wireOp",EDGE,"E692"),sQuery(id+"F0.wireOp",EDGE,"E693"),sQuery(id+"F0.wireOp",EDGE,"E694"),sQuery(id+"F0.wireOp",EDGE,"E695"),sQuery(id+"F0.wireOp",EDGE,"E696"),sQuery(id+"F0.wireOp",EDGE,"E697"),sQuery(id+"F0.wireOp",EDGE,"E698"),sQuery(id+"F0.wireOp",EDGE,"E699"),sQuery(id+"F0.wireOp",EDGE,"E700"),sQuery(id+"F0.wireOp",EDGE,"E701"),sQuery(id+"F0.wireOp",EDGE,"E702"),sQuery(id+"F0.wireOp",EDGE,"E703"),sQuery(id+"F0.wireOp",EDGE,"E704"),sQuery(id+"F0.wireOp",EDGE,"E705"),sQuery(id+"F0.wireOp",EDGE,"E706"),sQuery(id+"F0.wireOp",EDGE,"E707"),sQuery(id+"F0.wireOp",EDGE,"E708"),sQuery(id+"F0.wireOp",EDGE,"E709"),sQuery(id+"F0.wireOp",EDGE,"E710"),sQuery(id+"F0.wireOp",EDGE,"E711"),sQuery(id+"F0.wireOp",EDGE,"E712"),sQuery(id+"F0.wireOp",EDGE,"E713"),sQuery(id+"F0.wireOp",EDGE,"E714"),sQuery(id+"F0.wireOp",EDGE,"E715"),sQuery(id+"F0.wireOp",EDGE,"E716"),sQuery(id+"F0.wireOp",EDGE,"E717"),sQuery(id+"F0.wireOp",EDGE,"E718"),sQuery(id+"F0.wireOp",EDGE,"E719"),sQuery(id+"F0.wireOp",EDGE,"E720"),sQuery(id+"F0.wireOp",EDGE,"E721"),sQuery(id+"F0.wireOp",EDGE,"E722"),sQuery(id+"F0.wireOp",EDGE,"E723"),sQuery(id+"F0.wireOp",EDGE,"E724"),sQuery(id+"F0.wireOp",EDGE,"E725"),sQuery(id+"F0.wireOp",EDGE,"E726"),sQuery(id+"F0.wireOp",EDGE,"E727"),sQuery(id+"F0.wireOp",EDGE,"E728"),sQuery(id+"F0.wireOp",EDGE,"E729"),sQuery(id+"F0.wireOp",EDGE,"E730"),sQuery(id+"F0.wireOp",EDGE,"E731"),sQuery(id+"F0.wireOp",EDGE,"E732"),sQuery(id+"F0.wireOp",EDGE,"E733"),sQuery(id+"F0.wireOp",EDGE,"E734"),sQuery(id+"F0.wireOp",EDGE,"E735"),sQuery(id+"F0.wireOp",EDGE,"E736"),sQuery(id+"F0.wireOp",EDGE,"E737"),sQuery(id+"F0.wireOp",EDGE,"E738"),sQuery(id+"F0.wireOp",EDGE,"E739"),sQuery(id+"F0.wireOp",EDGE,"E740"),sQuery(id+"F0.wireOp",EDGE,"E741"),sQuery(id+"F0.wireOp",EDGE,"E742"),sQuery(id+"F0.wireOp",EDGE,"E743"),sQuery(id+"F0.wireOp",EDGE,"E744"),sQuery(id+"F0.wireOp",EDGE,"E745"),sQuery(id+"F0.wireOp",EDGE,"E746"),sQuery(id+"F0.wireOp",EDGE,"E747"),sQuery(id+"F0.wireOp",EDGE,"E748"),sQuery(id+"F0.wireOp",EDGE,"E749"),sQuery(id+"F0.wireOp",EDGE,"E750"),sQuery(id+"F0.wireOp",EDGE,"E751"),sQuery(id+"F0.wireOp",EDGE,"E752"),sQuery(id+"F0.wireOp",EDGE,"E753"),sQuery(id+"F0.wireOp",EDGE,"E754"),sQuery(id+"F0.wireOp",EDGE,"E755"),sQuery(id+"F0.wireOp",EDGE,"E756"),sQuery(id+"F0.wireOp",EDGE,"E757"),sQuery(id+"F0.wireOp",EDGE,"E758"),sQuery(id+"F0.wireOp",EDGE,"E759"),sQuery(id+"F0.wireOp",EDGE,"E760"),sQuery(id+"F0.wireOp",EDGE,"E761"),sQuery(id+"F0.wireOp",EDGE,"E762"),sQuery(id+"F0.wireOp",EDGE,"E763"),sQuery(id+"F0.wireOp",EDGE,"E764"),sQuery(id+"F0.wireOp",EDGE,"E765"),sQuery(id+"F0.wireOp",EDGE,"E766"),sQuery(id+"F0.wireOp",EDGE,"E767"),sQuery(id+"F0.wireOp",EDGE,"E768"),sQuery(id+"F0.wireOp",EDGE,"E769"),sQuery(id+"F0.wireOp",EDGE,"E770"),sQuery(id+"F0.wireOp",EDGE,"E771"),sQuery(id+"F0.wireOp",EDGE,"E772"),sQuery(id+"F0.wireOp",EDGE,"E773"),sQuery(id+"F0.wireOp",EDGE,"E774"),sQuery(id+"F0.wireOp",EDGE,"E775"),sQuery(id+"F0.wireOp",EDGE,"E776"),sQuery(id+"F0.wireOp",EDGE,"E777"),sQuery(id+"F0.wireOp",EDGE,"E778"),sQuery(id+"F0.wireOp",EDGE,"E779"),sQuery(id+"F0.wireOp",EDGE,"E780"),sQuery(id+"F0.wireOp",EDGE,"E781"),sQuery(id+"F0.wireOp",EDGE,"E782"),sQuery(id+"F0.wireOp",EDGE,"E783"),sQuery(id+"F0.wireOp",EDGE,"E784"),sQuery(id+"F0.wireOp",EDGE,"E785"),sQuery(id+"F0.wireOp",EDGE,"E786"),sQuery(id+"F0.wireOp",EDGE,"E787"),sQuery(id+"F0.wireOp",EDGE,"E788"),sQuery(id+"F0.wireOp",EDGE,"E789"),sQuery(id+"F0.wireOp",EDGE,"E790"),sQuery(id+"F0.wireOp",EDGE,"E791"),sQuery(id+"F0.wireOp",EDGE,"E792"),sQuery(id+"F0.wireOp",EDGE,"E793"),sQuery(id+"F0.wireOp",EDGE,"E794"),sQuery(id+"F0.wireOp",EDGE,"E795"),sQuery(id+"F0.wireOp",EDGE,"E796"),sQuery(id+"F0.wireOp",EDGE,"E797"),sQuery(id+"F0.wireOp",EDGE,"E798"),sQuery(id+"F0.wireOp",EDGE,"E799"),sQuery(id+"F0.wireOp",EDGE,"E800"),sQuery(id+"F0.wireOp",EDGE,"E801"),sQuery(id+"F0.wireOp",EDGE,"E802"),sQuery(id+"F0.wireOp",EDGE,"E803"),sQuery(id+"F0.wireOp",EDGE,"E804"),sQuery(id+"F0.wireOp",EDGE,"E805"),sQuery(id+"F0.wireOp",EDGE,"E806"),sQuery(id+"F0.wireOp",EDGE,"E807"),sQuery(id+"F0.wireOp",EDGE,"E808"),sQuery(id+"F0.wireOp",EDGE,"E809"),sQuery(id+"F0.wireOp",EDGE,"E810"),sQuery(id+"F0.wireOp",EDGE,"E811"),sQuery(id+"F0.wireOp",EDGE,"E812"),sQuery(id+"F0.wireOp",EDGE,"E813"),sQuery(id+"F0.wireOp",EDGE,"E814"),sQuery(id+"F0.wireOp",EDGE,"E815"),sQuery(id+"F0.wireOp",EDGE,"E816")])],"isStart":false});
            var sketch = newSketch(context, id + "F2", { "sketchPlane" : qUnion([Q0])});
            skLineSegment(sketch, "E817", {"start": v(0, 31.25) * mm, "end": v(0, -3.23) * mm, "construction": true});
            skLineSegment(sketch, "E818", {"start": v(0, -3.23) * mm, "end": v(-37.38, -24.8) * mm, "construction": true});
            skLineSegment(sketch, "E819", {"start": v(0, -3.23) * mm, "end": v(36.68, -24.4) * mm, "construction": true});
            skCircle(sketch, "E820", {"center": v(-25.45, -17.92) * mm, "radius": 2.3 * mm});
            skCircle(sketch, "E821", {"center": v(0, 25.35) * mm, "radius": 1.25 * mm});
            skCircle(sketch, "E822", {"center": v(25.84, -18.15) * mm, "radius": 1.25 * mm});
            skCircle(sketch, "E823", {"center": v(25.84, -18.15) * mm, "radius": 2.3 * mm});
            skCircle(sketch, "E824", {"center": v(0, 25.35) * mm, "radius": 2.3 * mm});
            skCircle(sketch, "E825", {"center": v(-25.45, -17.92) * mm, "radius": 1.25 * mm});
            skSolve(sketch);
        }
        {
            var Q0;
            {var subQ1=makeQuery(id+"F1.opExtrude","CAP_EDGE",EDGE,{"disambiguationData":[OSD([sQuery(id+"F0.wireOp",EDGE,"E266")])],"isStart":false});var subQ5=sQuery(id+"F2.wireOp",EDGE,"E820");var subQ6=makeQuery(id+"F2.imprint","INTERSECT",VERTEX,{"derivedFrom":[subQ1,subQ5]});Q0=makeQuery(id+"F2.imprint","IMPRINT",FACE,{"disambiguationData":[TD([[makeQuery(id+"F2.imprint","IMPRINT",EDGE,{"disambiguationData":[TD([[subQ6,-1.0]])],"derivedFrom":subQ5}),1.0]])]});}
            var Q1;
            {var subQ0=sQuery(id+"F2.wireOp",EDGE,"E821");var subQ1=makeQuery(id+"F1.opExtrude","CAP_EDGE",EDGE,{"disambiguationData":[OSD([sQuery(id+"F0.wireOp",EDGE,"E1")])],"isStart":false});var subQ2=makeQuery(id+"F2.imprint","INTERSECT",VERTEX,{"derivedFrom":[subQ1,subQ0]});Q1=makeQuery(id+"F2.imprint","IMPRINT",FACE,{"disambiguationData":[TD([[makeQuery(id+"F2.imprint","IMPRINT",EDGE,{"disambiguationData":[TD([[subQ2,1.0]])],"derivedFrom":subQ0}),-1.0]])]});}
            var Q2;
            {var subQ0=makeQuery(id+"F1.opExtrude","CAP_EDGE",EDGE,{"disambiguationData":[OSD([sQuery(id+"F0.wireOp",EDGE,"E545")])],"isStart":false});var subQ3=sQuery(id+"F2.wireOp",EDGE,"E822");var subQ4=makeQuery(id+"F2.imprint","INTERSECT",VERTEX,{"derivedFrom":[subQ0,subQ3]});Q2=makeQuery(id+"F2.imprint","IMPRINT",FACE,{"disambiguationData":[TD([[makeQuery(id+"F2.imprint","IMPRINT",EDGE,{"disambiguationData":[TD([[subQ4,-1.0]])],"derivedFrom":subQ3}),-1.0]])]});}
            extrude(context, id + "F3", {"entities" : qUnion([Q0, Q1, Q2]), "operationType" : NewBodyOperationType.ADD, "oppositeDirection" : true, "depth" : 3 * mm});
        }
        {
            var Q0;
            {var subQ0=sQuery(id+"F0.wireOp",EDGE,"E550");var subQ1=sQuery(id+"F0.wireOp",EDGE,"E549");var subQ2=sQuery(id+"F0.wireOp",EDGE,"E545");var subQ3=sQuery(id+"F0.wireOp",EDGE,"E544");var subQ4=sQuery(id+"F0.wireOp",EDGE,"E814");var subQ5=sQuery(id+"F0.wireOp",EDGE,"E1");var subQ6=sQuery(id+"F0.wireOp",EDGE,"E271");var subQ7=sQuery(id+"F0.wireOp",EDGE,"E267");var subQ8=sQuery(id+"F0.wireOp",EDGE,"E266");Q0=makeQuery(id+"F3.boolean.opBoolean","MERGE",FACE,{"derivedFrom":[makeQuery(id+"F1.opExtrude","CAP_FACE",FACE,{"disambiguationData":[OSD([sQuery(id+"F0.wireOp",EDGE,"E0"),subQ5,sQuery(id+"F0.wireOp",EDGE,"E2"),sQuery(id+"F0.wireOp",EDGE,"E3"),sQuery(id+"F0.wireOp",EDGE,"E4"),sQuery(id+"F0.wireOp",EDGE,"E5"),sQuery(id+"F0.wireOp",EDGE,"E6"),sQuery(id+"F0.wireOp",EDGE,"E7"),sQuery(id+"F0.wireOp",EDGE,"E8"),sQuery(id+"F0.wireOp",EDGE,"E9"),sQuery(id+"F0.wireOp",EDGE,"E10"),sQuery(id+"F0.wireOp",EDGE,"E11"),sQuery(id+"F0.wireOp",EDGE,"E12"),sQuery(id+"F0.wireOp",EDGE,"E13"),sQuery(id+"F0.wireOp",EDGE,"E14"),sQuery(id+"F0.wireOp",EDGE,"E15"),sQuery(id+"F0.wireOp",EDGE,"E16"),sQuery(id+"F0.wireOp",EDGE,"E17"),sQuery(id+"F0.wireOp",EDGE,"E18"),sQuery(id+"F0.wireOp",EDGE,"E19"),sQuery(id+"F0.wireOp",EDGE,"E20"),sQuery(id+"F0.wireOp",EDGE,"E21"),sQuery(id+"F0.wireOp",EDGE,"E22"),sQuery(id+"F0.wireOp",EDGE,"E23"),sQuery(id+"F0.wireOp",EDGE,"E24"),sQuery(id+"F0.wireOp",EDGE,"E25"),sQuery(id+"F0.wireOp",EDGE,"E26"),sQuery(id+"F0.wireOp",EDGE,"E27"),sQuery(id+"F0.wireOp",EDGE,"E28"),sQuery(id+"F0.wireOp",EDGE,"E29"),sQuery(id+"F0.wireOp",EDGE,"E30"),sQuery(id+"F0.wireOp",EDGE,"E31"),sQuery(id+"F0.wireOp",EDGE,"E32"),sQuery(id+"F0.wireOp",EDGE,"E33"),sQuery(id+"F0.wireOp",EDGE,"E34"),sQuery(id+"F0.wireOp",EDGE,"E35"),sQuery(id+"F0.wireOp",EDGE,"E36"),sQuery(id+"F0.wireOp",EDGE,"E37"),sQuery(id+"F0.wireOp",EDGE,"E38"),sQuery(id+"F0.wireOp",EDGE,"E39"),sQuery(id+"F0.wireOp",EDGE,"E40"),sQuery(id+"F0.wireOp",EDGE,"E41"),sQuery(id+"F0.wireOp",EDGE,"E42"),sQuery(id+"F0.wireOp",EDGE,"E43"),sQuery(id+"F0.wireOp",EDGE,"E44"),sQuery(id+"F0.wireOp",EDGE,"E45"),sQuery(id+"F0.wireOp",EDGE,"E46"),sQuery(id+"F0.wireOp",EDGE,"E47"),sQuery(id+"F0.wireOp",EDGE,"E48"),sQuery(id+"F0.wireOp",EDGE,"E49"),sQuery(id+"F0.wireOp",EDGE,"E50"),sQuery(id+"F0.wireOp",EDGE,"E51"),sQuery(id+"F0.wireOp",EDGE,"E52"),sQuery(id+"F0.wireOp",EDGE,"E53"),sQuery(id+"F0.wireOp",EDGE,"E54"),sQuery(id+"F0.wireOp",EDGE,"E55"),sQuery(id+"F0.wireOp",EDGE,"E56"),sQuery(id+"F0.wireOp",EDGE,"E57"),sQuery(id+"F0.wireOp",EDGE,"E58"),sQuery(id+"F0.wireOp",EDGE,"E59"),sQuery(id+"F0.wireOp",EDGE,"E60"),sQuery(id+"F0.wireOp",EDGE,"E61"),sQuery(id+"F0.wireOp",EDGE,"E62"),sQuery(id+"F0.wireOp",EDGE,"E63"),sQuery(id+"F0.wireOp",EDGE,"E64"),sQuery(id+"F0.wireOp",EDGE,"E65"),sQuery(id+"F0.wireOp",EDGE,"E66"),sQuery(id+"F0.wireOp",EDGE,"E67"),sQuery(id+"F0.wireOp",EDGE,"E68"),sQuery(id+"F0.wireOp",EDGE,"E69"),sQuery(id+"F0.wireOp",EDGE,"E70"),sQuery(id+"F0.wireOp",EDGE,"E71"),sQuery(id+"F0.wireOp",EDGE,"E72"),sQuery(id+"F0.wireOp",EDGE,"E73"),sQuery(id+"F0.wireOp",EDGE,"E74"),sQuery(id+"F0.wireOp",EDGE,"E75"),sQuery(id+"F0.wireOp",EDGE,"E76"),sQuery(id+"F0.wireOp",EDGE,"E77"),sQuery(id+"F0.wireOp",EDGE,"E78"),sQuery(id+"F0.wireOp",EDGE,"E79"),sQuery(id+"F0.wireOp",EDGE,"E80"),sQuery(id+"F0.wireOp",EDGE,"E81"),sQuery(id+"F0.wireOp",EDGE,"E82"),sQuery(id+"F0.wireOp",EDGE,"E83"),sQuery(id+"F0.wireOp",EDGE,"E84"),sQuery(id+"F0.wireOp",EDGE,"E85"),sQuery(id+"F0.wireOp",EDGE,"E86"),sQuery(id+"F0.wireOp",EDGE,"E87"),sQuery(id+"F0.wireOp",EDGE,"E88"),sQuery(id+"F0.wireOp",EDGE,"E89"),sQuery(id+"F0.wireOp",EDGE,"E90"),sQuery(id+"F0.wireOp",EDGE,"E91"),sQuery(id+"F0.wireOp",EDGE,"E92"),sQuery(id+"F0.wireOp",EDGE,"E93"),sQuery(id+"F0.wireOp",EDGE,"E94"),sQuery(id+"F0.wireOp",EDGE,"E95"),sQuery(id+"F0.wireOp",EDGE,"E96"),sQuery(id+"F0.wireOp",EDGE,"E97"),sQuery(id+"F0.wireOp",EDGE,"E98"),sQuery(id+"F0.wireOp",EDGE,"E99"),sQuery(id+"F0.wireOp",EDGE,"E100"),sQuery(id+"F0.wireOp",EDGE,"E101"),sQuery(id+"F0.wireOp",EDGE,"E102"),sQuery(id+"F0.wireOp",EDGE,"E103"),sQuery(id+"F0.wireOp",EDGE,"E104"),sQuery(id+"F0.wireOp",EDGE,"E105"),sQuery(id+"F0.wireOp",EDGE,"E106"),sQuery(id+"F0.wireOp",EDGE,"E107"),sQuery(id+"F0.wireOp",EDGE,"E108"),sQuery(id+"F0.wireOp",EDGE,"E109"),sQuery(id+"F0.wireOp",EDGE,"E110"),sQuery(id+"F0.wireOp",EDGE,"E111"),sQuery(id+"F0.wireOp",EDGE,"E112"),sQuery(id+"F0.wireOp",EDGE,"E113"),sQuery(id+"F0.wireOp",EDGE,"E114"),sQuery(id+"F0.wireOp",EDGE,"E115"),sQuery(id+"F0.wireOp",EDGE,"E116"),sQuery(id+"F0.wireOp",EDGE,"E117"),sQuery(id+"F0.wireOp",EDGE,"E118"),sQuery(id+"F0.wireOp",EDGE,"E119"),sQuery(id+"F0.wireOp",EDGE,"E120"),sQuery(id+"F0.wireOp",EDGE,"E121"),sQuery(id+"F0.wireOp",EDGE,"E122"),sQuery(id+"F0.wireOp",EDGE,"E123"),sQuery(id+"F0.wireOp",EDGE,"E124"),sQuery(id+"F0.wireOp",EDGE,"E125"),sQuery(id+"F0.wireOp",EDGE,"E126"),sQuery(id+"F0.wireOp",EDGE,"E127"),sQuery(id+"F0.wireOp",EDGE,"E128"),sQuery(id+"F0.wireOp",EDGE,"E129"),sQuery(id+"F0.wireOp",EDGE,"E130"),sQuery(id+"F0.wireOp",EDGE,"E131"),sQuery(id+"F0.wireOp",EDGE,"E132"),sQuery(id+"F0.wireOp",EDGE,"E133"),sQuery(id+"F0.wireOp",EDGE,"E134"),sQuery(id+"F0.wireOp",EDGE,"E135"),sQuery(id+"F0.wireOp",EDGE,"E136"),sQuery(id+"F0.wireOp",EDGE,"E137"),sQuery(id+"F0.wireOp",EDGE,"E138"),sQuery(id+"F0.wireOp",EDGE,"E139"),sQuery(id+"F0.wireOp",EDGE,"E140"),sQuery(id+"F0.wireOp",EDGE,"E141"),sQuery(id+"F0.wireOp",EDGE,"E142"),sQuery(id+"F0.wireOp",EDGE,"E143"),sQuery(id+"F0.wireOp",EDGE,"E144"),sQuery(id+"F0.wireOp",EDGE,"E145"),sQuery(id+"F0.wireOp",EDGE,"E146"),sQuery(id+"F0.wireOp",EDGE,"E147"),sQuery(id+"F0.wireOp",EDGE,"E148"),sQuery(id+"F0.wireOp",EDGE,"E149"),sQuery(id+"F0.wireOp",EDGE,"E150"),sQuery(id+"F0.wireOp",EDGE,"E151"),sQuery(id+"F0.wireOp",EDGE,"E152"),sQuery(id+"F0.wireOp",EDGE,"E153"),sQuery(id+"F0.wireOp",EDGE,"E154"),sQuery(id+"F0.wireOp",EDGE,"E155"),sQuery(id+"F0.wireOp",EDGE,"E156"),sQuery(id+"F0.wireOp",EDGE,"E157"),sQuery(id+"F0.wireOp",EDGE,"E158"),sQuery(id+"F0.wireOp",EDGE,"E159"),sQuery(id+"F0.wireOp",EDGE,"E160"),sQuery(id+"F0.wireOp",EDGE,"E161"),sQuery(id+"F0.wireOp",EDGE,"E162"),sQuery(id+"F0.wireOp",EDGE,"E163"),sQuery(id+"F0.wireOp",EDGE,"E164"),sQuery(id+"F0.wireOp",EDGE,"E165"),sQuery(id+"F0.wireOp",EDGE,"E166"),sQuery(id+"F0.wireOp",EDGE,"E167"),sQuery(id+"F0.wireOp",EDGE,"E168"),sQuery(id+"F0.wireOp",EDGE,"E169"),sQuery(id+"F0.wireOp",EDGE,"E170"),sQuery(id+"F0.wireOp",EDGE,"E171"),sQuery(id+"F0.wireOp",EDGE,"E172"),sQuery(id+"F0.wireOp",EDGE,"E173"),sQuery(id+"F0.wireOp",EDGE,"E174"),sQuery(id+"F0.wireOp",EDGE,"E175"),sQuery(id+"F0.wireOp",EDGE,"E176"),sQuery(id+"F0.wireOp",EDGE,"E177"),sQuery(id+"F0.wireOp",EDGE,"E178"),sQuery(id+"F0.wireOp",EDGE,"E179"),sQuery(id+"F0.wireOp",EDGE,"E180"),sQuery(id+"F0.wireOp",EDGE,"E181"),sQuery(id+"F0.wireOp",EDGE,"E182"),sQuery(id+"F0.wireOp",EDGE,"E183"),sQuery(id+"F0.wireOp",EDGE,"E184"),sQuery(id+"F0.wireOp",EDGE,"E185"),sQuery(id+"F0.wireOp",EDGE,"E186"),sQuery(id+"F0.wireOp",EDGE,"E187"),sQuery(id+"F0.wireOp",EDGE,"E188"),sQuery(id+"F0.wireOp",EDGE,"E189"),sQuery(id+"F0.wireOp",EDGE,"E190"),sQuery(id+"F0.wireOp",EDGE,"E191"),sQuery(id+"F0.wireOp",EDGE,"E192"),sQuery(id+"F0.wireOp",EDGE,"E193"),sQuery(id+"F0.wireOp",EDGE,"E194"),sQuery(id+"F0.wireOp",EDGE,"E195"),sQuery(id+"F0.wireOp",EDGE,"E196"),sQuery(id+"F0.wireOp",EDGE,"E197"),sQuery(id+"F0.wireOp",EDGE,"E198"),sQuery(id+"F0.wireOp",EDGE,"E199"),sQuery(id+"F0.wireOp",EDGE,"E200"),sQuery(id+"F0.wireOp",EDGE,"E201"),sQuery(id+"F0.wireOp",EDGE,"E202"),sQuery(id+"F0.wireOp",EDGE,"E203"),sQuery(id+"F0.wireOp",EDGE,"E204"),sQuery(id+"F0.wireOp",EDGE,"E205"),sQuery(id+"F0.wireOp",EDGE,"E206"),sQuery(id+"F0.wireOp",EDGE,"E207"),sQuery(id+"F0.wireOp",EDGE,"E208"),sQuery(id+"F0.wireOp",EDGE,"E209"),sQuery(id+"F0.wireOp",EDGE,"E210"),sQuery(id+"F0.wireOp",EDGE,"E211"),sQuery(id+"F0.wireOp",EDGE,"E212"),sQuery(id+"F0.wireOp",EDGE,"E213"),sQuery(id+"F0.wireOp",EDGE,"E214"),sQuery(id+"F0.wireOp",EDGE,"E215"),sQuery(id+"F0.wireOp",EDGE,"E216"),sQuery(id+"F0.wireOp",EDGE,"E217"),sQuery(id+"F0.wireOp",EDGE,"E218"),sQuery(id+"F0.wireOp",EDGE,"E219"),sQuery(id+"F0.wireOp",EDGE,"E220"),sQuery(id+"F0.wireOp",EDGE,"E221"),sQuery(id+"F0.wireOp",EDGE,"E222"),sQuery(id+"F0.wireOp",EDGE,"E223"),sQuery(id+"F0.wireOp",EDGE,"E224"),sQuery(id+"F0.wireOp",EDGE,"E225"),sQuery(id+"F0.wireOp",EDGE,"E226"),sQuery(id+"F0.wireOp",EDGE,"E227"),sQuery(id+"F0.wireOp",EDGE,"E228"),sQuery(id+"F0.wireOp",EDGE,"E229"),sQuery(id+"F0.wireOp",EDGE,"E230"),sQuery(id+"F0.wireOp",EDGE,"E231"),sQuery(id+"F0.wireOp",EDGE,"E232"),sQuery(id+"F0.wireOp",EDGE,"E233"),sQuery(id+"F0.wireOp",EDGE,"E234"),sQuery(id+"F0.wireOp",EDGE,"E235"),sQuery(id+"F0.wireOp",EDGE,"E236"),sQuery(id+"F0.wireOp",EDGE,"E237"),sQuery(id+"F0.wireOp",EDGE,"E238"),sQuery(id+"F0.wireOp",EDGE,"E239"),sQuery(id+"F0.wireOp",EDGE,"E240"),sQuery(id+"F0.wireOp",EDGE,"E241"),sQuery(id+"F0.wireOp",EDGE,"E242"),sQuery(id+"F0.wireOp",EDGE,"E243"),sQuery(id+"F0.wireOp",EDGE,"E244"),sQuery(id+"F0.wireOp",EDGE,"E245"),sQuery(id+"F0.wireOp",EDGE,"E246"),sQuery(id+"F0.wireOp",EDGE,"E247"),sQuery(id+"F0.wireOp",EDGE,"E248"),sQuery(id+"F0.wireOp",EDGE,"E249"),sQuery(id+"F0.wireOp",EDGE,"E250"),sQuery(id+"F0.wireOp",EDGE,"E251"),sQuery(id+"F0.wireOp",EDGE,"E252"),sQuery(id+"F0.wireOp",EDGE,"E253"),sQuery(id+"F0.wireOp",EDGE,"E254"),sQuery(id+"F0.wireOp",EDGE,"E255"),sQuery(id+"F0.wireOp",EDGE,"E256"),sQuery(id+"F0.wireOp",EDGE,"E257"),sQuery(id+"F0.wireOp",EDGE,"E258"),sQuery(id+"F0.wireOp",EDGE,"E259"),sQuery(id+"F0.wireOp",EDGE,"E260"),sQuery(id+"F0.wireOp",EDGE,"E261"),sQuery(id+"F0.wireOp",EDGE,"E262"),sQuery(id+"F0.wireOp",EDGE,"E263"),sQuery(id+"F0.wireOp",EDGE,"E264"),sQuery(id+"F0.wireOp",EDGE,"E265"),subQ8,subQ7,sQuery(id+"F0.wireOp",EDGE,"E268"),sQuery(id+"F0.wireOp",EDGE,"E269"),sQuery(id+"F0.wireOp",EDGE,"E270"),subQ6,sQuery(id+"F0.wireOp",EDGE,"E272"),sQuery(id+"F0.wireOp",EDGE,"E273"),sQuery(id+"F0.wireOp",EDGE,"E274"),sQuery(id+"F0.wireOp",EDGE,"E275"),sQuery(id+"F0.wireOp",EDGE,"E276"),sQuery(id+"F0.wireOp",EDGE,"E277"),sQuery(id+"F0.wireOp",EDGE,"E278"),sQuery(id+"F0.wireOp",EDGE,"E279"),sQuery(id+"F0.wireOp",EDGE,"E280"),sQuery(id+"F0.wireOp",EDGE,"E281"),sQuery(id+"F0.wireOp",EDGE,"E282"),sQuery(id+"F0.wireOp",EDGE,"E283"),sQuery(id+"F0.wireOp",EDGE,"E284"),sQuery(id+"F0.wireOp",EDGE,"E285"),sQuery(id+"F0.wireOp",EDGE,"E286"),sQuery(id+"F0.wireOp",EDGE,"E287"),sQuery(id+"F0.wireOp",EDGE,"E288"),sQuery(id+"F0.wireOp",EDGE,"E289"),sQuery(id+"F0.wireOp",EDGE,"E290"),sQuery(id+"F0.wireOp",EDGE,"E291"),sQuery(id+"F0.wireOp",EDGE,"E292"),sQuery(id+"F0.wireOp",EDGE,"E293"),sQuery(id+"F0.wireOp",EDGE,"E294"),sQuery(id+"F0.wireOp",EDGE,"E295"),sQuery(id+"F0.wireOp",EDGE,"E296"),sQuery(id+"F0.wireOp",EDGE,"E297"),sQuery(id+"F0.wireOp",EDGE,"E298"),sQuery(id+"F0.wireOp",EDGE,"E299"),sQuery(id+"F0.wireOp",EDGE,"E300"),sQuery(id+"F0.wireOp",EDGE,"E301"),sQuery(id+"F0.wireOp",EDGE,"E302"),sQuery(id+"F0.wireOp",EDGE,"E303"),sQuery(id+"F0.wireOp",EDGE,"E304"),sQuery(id+"F0.wireOp",EDGE,"E305"),sQuery(id+"F0.wireOp",EDGE,"E306"),sQuery(id+"F0.wireOp",EDGE,"E307"),sQuery(id+"F0.wireOp",EDGE,"E308"),sQuery(id+"F0.wireOp",EDGE,"E309"),sQuery(id+"F0.wireOp",EDGE,"E310"),sQuery(id+"F0.wireOp",EDGE,"E311"),sQuery(id+"F0.wireOp",EDGE,"E312"),sQuery(id+"F0.wireOp",EDGE,"E313"),sQuery(id+"F0.wireOp",EDGE,"E314"),sQuery(id+"F0.wireOp",EDGE,"E315"),sQuery(id+"F0.wireOp",EDGE,"E316"),sQuery(id+"F0.wireOp",EDGE,"E317"),sQuery(id+"F0.wireOp",EDGE,"E318"),sQuery(id+"F0.wireOp",EDGE,"E319"),sQuery(id+"F0.wireOp",EDGE,"E320"),sQuery(id+"F0.wireOp",EDGE,"E321"),sQuery(id+"F0.wireOp",EDGE,"E322"),sQuery(id+"F0.wireOp",EDGE,"E323"),sQuery(id+"F0.wireOp",EDGE,"E324"),sQuery(id+"F0.wireOp",EDGE,"E325"),sQuery(id+"F0.wireOp",EDGE,"E326"),sQuery(id+"F0.wireOp",EDGE,"E327"),sQuery(id+"F0.wireOp",EDGE,"E328"),sQuery(id+"F0.wireOp",EDGE,"E329"),sQuery(id+"F0.wireOp",EDGE,"E330"),sQuery(id+"F0.wireOp",EDGE,"E331"),sQuery(id+"F0.wireOp",EDGE,"E332"),sQuery(id+"F0.wireOp",EDGE,"E333"),sQuery(id+"F0.wireOp",EDGE,"E334"),sQuery(id+"F0.wireOp",EDGE,"E335"),sQuery(id+"F0.wireOp",EDGE,"E336"),sQuery(id+"F0.wireOp",EDGE,"E337"),sQuery(id+"F0.wireOp",EDGE,"E338"),sQuery(id+"F0.wireOp",EDGE,"E339"),sQuery(id+"F0.wireOp",EDGE,"E340"),sQuery(id+"F0.wireOp",EDGE,"E341"),sQuery(id+"F0.wireOp",EDGE,"E342"),sQuery(id+"F0.wireOp",EDGE,"E343"),sQuery(id+"F0.wireOp",EDGE,"E344"),sQuery(id+"F0.wireOp",EDGE,"E345"),sQuery(id+"F0.wireOp",EDGE,"E346"),sQuery(id+"F0.wireOp",EDGE,"E347"),sQuery(id+"F0.wireOp",EDGE,"E348"),sQuery(id+"F0.wireOp",EDGE,"E349"),sQuery(id+"F0.wireOp",EDGE,"E350"),sQuery(id+"F0.wireOp",EDGE,"E351"),sQuery(id+"F0.wireOp",EDGE,"E352"),sQuery(id+"F0.wireOp",EDGE,"E353"),sQuery(id+"F0.wireOp",EDGE,"E354"),sQuery(id+"F0.wireOp",EDGE,"E355"),sQuery(id+"F0.wireOp",EDGE,"E356"),sQuery(id+"F0.wireOp",EDGE,"E357"),sQuery(id+"F0.wireOp",EDGE,"E358"),sQuery(id+"F0.wireOp",EDGE,"E359"),sQuery(id+"F0.wireOp",EDGE,"E360"),sQuery(id+"F0.wireOp",EDGE,"E361"),sQuery(id+"F0.wireOp",EDGE,"E362"),sQuery(id+"F0.wireOp",EDGE,"E363"),sQuery(id+"F0.wireOp",EDGE,"E364"),sQuery(id+"F0.wireOp",EDGE,"E365"),sQuery(id+"F0.wireOp",EDGE,"E366"),sQuery(id+"F0.wireOp",EDGE,"E367"),sQuery(id+"F0.wireOp",EDGE,"E368"),sQuery(id+"F0.wireOp",EDGE,"E369"),sQuery(id+"F0.wireOp",EDGE,"E370"),sQuery(id+"F0.wireOp",EDGE,"E371"),sQuery(id+"F0.wireOp",EDGE,"E372"),sQuery(id+"F0.wireOp",EDGE,"E373"),sQuery(id+"F0.wireOp",EDGE,"E374"),sQuery(id+"F0.wireOp",EDGE,"E375"),sQuery(id+"F0.wireOp",EDGE,"E376"),sQuery(id+"F0.wireOp",EDGE,"E377"),sQuery(id+"F0.wireOp",EDGE,"E378"),sQuery(id+"F0.wireOp",EDGE,"E379"),sQuery(id+"F0.wireOp",EDGE,"E380"),sQuery(id+"F0.wireOp",EDGE,"E381"),sQuery(id+"F0.wireOp",EDGE,"E382"),sQuery(id+"F0.wireOp",EDGE,"E383"),sQuery(id+"F0.wireOp",EDGE,"E384"),sQuery(id+"F0.wireOp",EDGE,"E385"),sQuery(id+"F0.wireOp",EDGE,"E386"),sQuery(id+"F0.wireOp",EDGE,"E387"),sQuery(id+"F0.wireOp",EDGE,"E388"),sQuery(id+"F0.wireOp",EDGE,"E389"),sQuery(id+"F0.wireOp",EDGE,"E390"),sQuery(id+"F0.wireOp",EDGE,"E391"),sQuery(id+"F0.wireOp",EDGE,"E392"),sQuery(id+"F0.wireOp",EDGE,"E393"),sQuery(id+"F0.wireOp",EDGE,"E394"),sQuery(id+"F0.wireOp",EDGE,"E395"),sQuery(id+"F0.wireOp",EDGE,"E396"),sQuery(id+"F0.wireOp",EDGE,"E397"),sQuery(id+"F0.wireOp",EDGE,"E398"),sQuery(id+"F0.wireOp",EDGE,"E399"),sQuery(id+"F0.wireOp",EDGE,"E400"),sQuery(id+"F0.wireOp",EDGE,"E401"),sQuery(id+"F0.wireOp",EDGE,"E402"),sQuery(id+"F0.wireOp",EDGE,"E403"),sQuery(id+"F0.wireOp",EDGE,"E404"),sQuery(id+"F0.wireOp",EDGE,"E405"),sQuery(id+"F0.wireOp",EDGE,"E406"),sQuery(id+"F0.wireOp",EDGE,"E407"),sQuery(id+"F0.wireOp",EDGE,"E408"),sQuery(id+"F0.wireOp",EDGE,"E409"),sQuery(id+"F0.wireOp",EDGE,"E410"),sQuery(id+"F0.wireOp",EDGE,"E411"),sQuery(id+"F0.wireOp",EDGE,"E412"),sQuery(id+"F0.wireOp",EDGE,"E413"),sQuery(id+"F0.wireOp",EDGE,"E414"),sQuery(id+"F0.wireOp",EDGE,"E415"),sQuery(id+"F0.wireOp",EDGE,"E416"),sQuery(id+"F0.wireOp",EDGE,"E417"),sQuery(id+"F0.wireOp",EDGE,"E418"),sQuery(id+"F0.wireOp",EDGE,"E419"),sQuery(id+"F0.wireOp",EDGE,"E420"),sQuery(id+"F0.wireOp",EDGE,"E421"),sQuery(id+"F0.wireOp",EDGE,"E422"),sQuery(id+"F0.wireOp",EDGE,"E423"),sQuery(id+"F0.wireOp",EDGE,"E424"),sQuery(id+"F0.wireOp",EDGE,"E425"),sQuery(id+"F0.wireOp",EDGE,"E426"),sQuery(id+"F0.wireOp",EDGE,"E427"),sQuery(id+"F0.wireOp",EDGE,"E428"),sQuery(id+"F0.wireOp",EDGE,"E429"),sQuery(id+"F0.wireOp",EDGE,"E430"),sQuery(id+"F0.wireOp",EDGE,"E431"),sQuery(id+"F0.wireOp",EDGE,"E432"),sQuery(id+"F0.wireOp",EDGE,"E433"),sQuery(id+"F0.wireOp",EDGE,"E434"),sQuery(id+"F0.wireOp",EDGE,"E435"),sQuery(id+"F0.wireOp",EDGE,"E436"),sQuery(id+"F0.wireOp",EDGE,"E437"),sQuery(id+"F0.wireOp",EDGE,"E438"),sQuery(id+"F0.wireOp",EDGE,"E439"),sQuery(id+"F0.wireOp",EDGE,"E440"),sQuery(id+"F0.wireOp",EDGE,"E441"),sQuery(id+"F0.wireOp",EDGE,"E442"),sQuery(id+"F0.wireOp",EDGE,"E443"),sQuery(id+"F0.wireOp",EDGE,"E444"),sQuery(id+"F0.wireOp",EDGE,"E445"),sQuery(id+"F0.wireOp",EDGE,"E446"),sQuery(id+"F0.wireOp",EDGE,"E447"),sQuery(id+"F0.wireOp",EDGE,"E448"),sQuery(id+"F0.wireOp",EDGE,"E449"),sQuery(id+"F0.wireOp",EDGE,"E450"),sQuery(id+"F0.wireOp",EDGE,"E451"),sQuery(id+"F0.wireOp",EDGE,"E452"),sQuery(id+"F0.wireOp",EDGE,"E453"),sQuery(id+"F0.wireOp",EDGE,"E454"),sQuery(id+"F0.wireOp",EDGE,"E455"),sQuery(id+"F0.wireOp",EDGE,"E456"),sQuery(id+"F0.wireOp",EDGE,"E457"),sQuery(id+"F0.wireOp",EDGE,"E458"),sQuery(id+"F0.wireOp",EDGE,"E459"),sQuery(id+"F0.wireOp",EDGE,"E460"),sQuery(id+"F0.wireOp",EDGE,"E461"),sQuery(id+"F0.wireOp",EDGE,"E462"),sQuery(id+"F0.wireOp",EDGE,"E463"),sQuery(id+"F0.wireOp",EDGE,"E464"),sQuery(id+"F0.wireOp",EDGE,"E465"),sQuery(id+"F0.wireOp",EDGE,"E466"),sQuery(id+"F0.wireOp",EDGE,"E467"),sQuery(id+"F0.wireOp",EDGE,"E468"),sQuery(id+"F0.wireOp",EDGE,"E469"),sQuery(id+"F0.wireOp",EDGE,"E470"),sQuery(id+"F0.wireOp",EDGE,"E471"),sQuery(id+"F0.wireOp",EDGE,"E472"),sQuery(id+"F0.wireOp",EDGE,"E473"),sQuery(id+"F0.wireOp",EDGE,"E474"),sQuery(id+"F0.wireOp",EDGE,"E475"),sQuery(id+"F0.wireOp",EDGE,"E476"),sQuery(id+"F0.wireOp",EDGE,"E477"),sQuery(id+"F0.wireOp",EDGE,"E478"),sQuery(id+"F0.wireOp",EDGE,"E479"),sQuery(id+"F0.wireOp",EDGE,"E480"),sQuery(id+"F0.wireOp",EDGE,"E481"),sQuery(id+"F0.wireOp",EDGE,"E482"),sQuery(id+"F0.wireOp",EDGE,"E483"),sQuery(id+"F0.wireOp",EDGE,"E484"),sQuery(id+"F0.wireOp",EDGE,"E485"),sQuery(id+"F0.wireOp",EDGE,"E486"),sQuery(id+"F0.wireOp",EDGE,"E487"),sQuery(id+"F0.wireOp",EDGE,"E488"),sQuery(id+"F0.wireOp",EDGE,"E489"),sQuery(id+"F0.wireOp",EDGE,"E490"),sQuery(id+"F0.wireOp",EDGE,"E491"),sQuery(id+"F0.wireOp",EDGE,"E492"),sQuery(id+"F0.wireOp",EDGE,"E493"),sQuery(id+"F0.wireOp",EDGE,"E494"),sQuery(id+"F0.wireOp",EDGE,"E495"),sQuery(id+"F0.wireOp",EDGE,"E496"),sQuery(id+"F0.wireOp",EDGE,"E497"),sQuery(id+"F0.wireOp",EDGE,"E498"),sQuery(id+"F0.wireOp",EDGE,"E499"),sQuery(id+"F0.wireOp",EDGE,"E500"),sQuery(id+"F0.wireOp",EDGE,"E501"),sQuery(id+"F0.wireOp",EDGE,"E502"),sQuery(id+"F0.wireOp",EDGE,"E503"),sQuery(id+"F0.wireOp",EDGE,"E504"),sQuery(id+"F0.wireOp",EDGE,"E505"),sQuery(id+"F0.wireOp",EDGE,"E506"),sQuery(id+"F0.wireOp",EDGE,"E507"),sQuery(id+"F0.wireOp",EDGE,"E508"),sQuery(id+"F0.wireOp",EDGE,"E509"),sQuery(id+"F0.wireOp",EDGE,"E510"),sQuery(id+"F0.wireOp",EDGE,"E511"),sQuery(id+"F0.wireOp",EDGE,"E512"),sQuery(id+"F0.wireOp",EDGE,"E513"),sQuery(id+"F0.wireOp",EDGE,"E514"),sQuery(id+"F0.wireOp",EDGE,"E515"),sQuery(id+"F0.wireOp",EDGE,"E516"),sQuery(id+"F0.wireOp",EDGE,"E517"),sQuery(id+"F0.wireOp",EDGE,"E518"),sQuery(id+"F0.wireOp",EDGE,"E519"),sQuery(id+"F0.wireOp",EDGE,"E520"),sQuery(id+"F0.wireOp",EDGE,"E521"),sQuery(id+"F0.wireOp",EDGE,"E522"),sQuery(id+"F0.wireOp",EDGE,"E523"),sQuery(id+"F0.wireOp",EDGE,"E524"),sQuery(id+"F0.wireOp",EDGE,"E525"),sQuery(id+"F0.wireOp",EDGE,"E526"),sQuery(id+"F0.wireOp",EDGE,"E527"),sQuery(id+"F0.wireOp",EDGE,"E528"),sQuery(id+"F0.wireOp",EDGE,"E529"),sQuery(id+"F0.wireOp",EDGE,"E530"),sQuery(id+"F0.wireOp",EDGE,"E531"),sQuery(id+"F0.wireOp",EDGE,"E532"),sQuery(id+"F0.wireOp",EDGE,"E533"),sQuery(id+"F0.wireOp",EDGE,"E534"),sQuery(id+"F0.wireOp",EDGE,"E535"),sQuery(id+"F0.wireOp",EDGE,"E536"),sQuery(id+"F0.wireOp",EDGE,"E537"),sQuery(id+"F0.wireOp",EDGE,"E538"),sQuery(id+"F0.wireOp",EDGE,"E539"),sQuery(id+"F0.wireOp",EDGE,"E540"),sQuery(id+"F0.wireOp",EDGE,"E541"),sQuery(id+"F0.wireOp",EDGE,"E542"),sQuery(id+"F0.wireOp",EDGE,"E543"),subQ3,subQ2,sQuery(id+"F0.wireOp",EDGE,"E546"),sQuery(id+"F0.wireOp",EDGE,"E547"),sQuery(id+"F0.wireOp",EDGE,"E548"),subQ1,subQ0,sQuery(id+"F0.wireOp",EDGE,"E551"),sQuery(id+"F0.wireOp",EDGE,"E552"),sQuery(id+"F0.wireOp",EDGE,"E553"),sQuery(id+"F0.wireOp",EDGE,"E554"),sQuery(id+"F0.wireOp",EDGE,"E555"),sQuery(id+"F0.wireOp",EDGE,"E556"),sQuery(id+"F0.wireOp",EDGE,"E557"),sQuery(id+"F0.wireOp",EDGE,"E558"),sQuery(id+"F0.wireOp",EDGE,"E559"),sQuery(id+"F0.wireOp",EDGE,"E560"),sQuery(id+"F0.wireOp",EDGE,"E561"),sQuery(id+"F0.wireOp",EDGE,"E562"),sQuery(id+"F0.wireOp",EDGE,"E563"),sQuery(id+"F0.wireOp",EDGE,"E564"),sQuery(id+"F0.wireOp",EDGE,"E565"),sQuery(id+"F0.wireOp",EDGE,"E566"),sQuery(id+"F0.wireOp",EDGE,"E567"),sQuery(id+"F0.wireOp",EDGE,"E568"),sQuery(id+"F0.wireOp",EDGE,"E569"),sQuery(id+"F0.wireOp",EDGE,"E570"),sQuery(id+"F0.wireOp",EDGE,"E571"),sQuery(id+"F0.wireOp",EDGE,"E572"),sQuery(id+"F0.wireOp",EDGE,"E573"),sQuery(id+"F0.wireOp",EDGE,"E574"),sQuery(id+"F0.wireOp",EDGE,"E575"),sQuery(id+"F0.wireOp",EDGE,"E576"),sQuery(id+"F0.wireOp",EDGE,"E577"),sQuery(id+"F0.wireOp",EDGE,"E578"),sQuery(id+"F0.wireOp",EDGE,"E579"),sQuery(id+"F0.wireOp",EDGE,"E580"),sQuery(id+"F0.wireOp",EDGE,"E581"),sQuery(id+"F0.wireOp",EDGE,"E582"),sQuery(id+"F0.wireOp",EDGE,"E583"),sQuery(id+"F0.wireOp",EDGE,"E584"),sQuery(id+"F0.wireOp",EDGE,"E585"),sQuery(id+"F0.wireOp",EDGE,"E586"),sQuery(id+"F0.wireOp",EDGE,"E587"),sQuery(id+"F0.wireOp",EDGE,"E588"),sQuery(id+"F0.wireOp",EDGE,"E589"),sQuery(id+"F0.wireOp",EDGE,"E590"),sQuery(id+"F0.wireOp",EDGE,"E591"),sQuery(id+"F0.wireOp",EDGE,"E592"),sQuery(id+"F0.wireOp",EDGE,"E593"),sQuery(id+"F0.wireOp",EDGE,"E594"),sQuery(id+"F0.wireOp",EDGE,"E595"),sQuery(id+"F0.wireOp",EDGE,"E596"),sQuery(id+"F0.wireOp",EDGE,"E597"),sQuery(id+"F0.wireOp",EDGE,"E598"),sQuery(id+"F0.wireOp",EDGE,"E599"),sQuery(id+"F0.wireOp",EDGE,"E600"),sQuery(id+"F0.wireOp",EDGE,"E601"),sQuery(id+"F0.wireOp",EDGE,"E602"),sQuery(id+"F0.wireOp",EDGE,"E603"),sQuery(id+"F0.wireOp",EDGE,"E604"),sQuery(id+"F0.wireOp",EDGE,"E605"),sQuery(id+"F0.wireOp",EDGE,"E606"),sQuery(id+"F0.wireOp",EDGE,"E607"),sQuery(id+"F0.wireOp",EDGE,"E608"),sQuery(id+"F0.wireOp",EDGE,"E609"),sQuery(id+"F0.wireOp",EDGE,"E610"),sQuery(id+"F0.wireOp",EDGE,"E611"),sQuery(id+"F0.wireOp",EDGE,"E612"),sQuery(id+"F0.wireOp",EDGE,"E613"),sQuery(id+"F0.wireOp",EDGE,"E614"),sQuery(id+"F0.wireOp",EDGE,"E615"),sQuery(id+"F0.wireOp",EDGE,"E616"),sQuery(id+"F0.wireOp",EDGE,"E617"),sQuery(id+"F0.wireOp",EDGE,"E618"),sQuery(id+"F0.wireOp",EDGE,"E619"),sQuery(id+"F0.wireOp",EDGE,"E620"),sQuery(id+"F0.wireOp",EDGE,"E621"),sQuery(id+"F0.wireOp",EDGE,"E622"),sQuery(id+"F0.wireOp",EDGE,"E623"),sQuery(id+"F0.wireOp",EDGE,"E624"),sQuery(id+"F0.wireOp",EDGE,"E625"),sQuery(id+"F0.wireOp",EDGE,"E626"),sQuery(id+"F0.wireOp",EDGE,"E627"),sQuery(id+"F0.wireOp",EDGE,"E628"),sQuery(id+"F0.wireOp",EDGE,"E629"),sQuery(id+"F0.wireOp",EDGE,"E630"),sQuery(id+"F0.wireOp",EDGE,"E631"),sQuery(id+"F0.wireOp",EDGE,"E632"),sQuery(id+"F0.wireOp",EDGE,"E633"),sQuery(id+"F0.wireOp",EDGE,"E634"),sQuery(id+"F0.wireOp",EDGE,"E635"),sQuery(id+"F0.wireOp",EDGE,"E636"),sQuery(id+"F0.wireOp",EDGE,"E637"),sQuery(id+"F0.wireOp",EDGE,"E638"),sQuery(id+"F0.wireOp",EDGE,"E639"),sQuery(id+"F0.wireOp",EDGE,"E640"),sQuery(id+"F0.wireOp",EDGE,"E641"),sQuery(id+"F0.wireOp",EDGE,"E642"),sQuery(id+"F0.wireOp",EDGE,"E643"),sQuery(id+"F0.wireOp",EDGE,"E644"),sQuery(id+"F0.wireOp",EDGE,"E645"),sQuery(id+"F0.wireOp",EDGE,"E646"),sQuery(id+"F0.wireOp",EDGE,"E647"),sQuery(id+"F0.wireOp",EDGE,"E648"),sQuery(id+"F0.wireOp",EDGE,"E649"),sQuery(id+"F0.wireOp",EDGE,"E650"),sQuery(id+"F0.wireOp",EDGE,"E651"),sQuery(id+"F0.wireOp",EDGE,"E652"),sQuery(id+"F0.wireOp",EDGE,"E653"),sQuery(id+"F0.wireOp",EDGE,"E654"),sQuery(id+"F0.wireOp",EDGE,"E655"),sQuery(id+"F0.wireOp",EDGE,"E656"),sQuery(id+"F0.wireOp",EDGE,"E657"),sQuery(id+"F0.wireOp",EDGE,"E658"),sQuery(id+"F0.wireOp",EDGE,"E659"),sQuery(id+"F0.wireOp",EDGE,"E660"),sQuery(id+"F0.wireOp",EDGE,"E661"),sQuery(id+"F0.wireOp",EDGE,"E662"),sQuery(id+"F0.wireOp",EDGE,"E663"),sQuery(id+"F0.wireOp",EDGE,"E664"),sQuery(id+"F0.wireOp",EDGE,"E665"),sQuery(id+"F0.wireOp",EDGE,"E666"),sQuery(id+"F0.wireOp",EDGE,"E667"),sQuery(id+"F0.wireOp",EDGE,"E668"),sQuery(id+"F0.wireOp",EDGE,"E669"),sQuery(id+"F0.wireOp",EDGE,"E670"),sQuery(id+"F0.wireOp",EDGE,"E671"),sQuery(id+"F0.wireOp",EDGE,"E672"),sQuery(id+"F0.wireOp",EDGE,"E673"),sQuery(id+"F0.wireOp",EDGE,"E674"),sQuery(id+"F0.wireOp",EDGE,"E675"),sQuery(id+"F0.wireOp",EDGE,"E676"),sQuery(id+"F0.wireOp",EDGE,"E677"),sQuery(id+"F0.wireOp",EDGE,"E678"),sQuery(id+"F0.wireOp",EDGE,"E679"),sQuery(id+"F0.wireOp",EDGE,"E680"),sQuery(id+"F0.wireOp",EDGE,"E681"),sQuery(id+"F0.wireOp",EDGE,"E682"),sQuery(id+"F0.wireOp",EDGE,"E683"),sQuery(id+"F0.wireOp",EDGE,"E684"),sQuery(id+"F0.wireOp",EDGE,"E685"),sQuery(id+"F0.wireOp",EDGE,"E686"),sQuery(id+"F0.wireOp",EDGE,"E687"),sQuery(id+"F0.wireOp",EDGE,"E688"),sQuery(id+"F0.wireOp",EDGE,"E689"),sQuery(id+"F0.wireOp",EDGE,"E690"),sQuery(id+"F0.wireOp",EDGE,"E691"),sQuery(id+"F0.wireOp",EDGE,"E692"),sQuery(id+"F0.wireOp",EDGE,"E693"),sQuery(id+"F0.wireOp",EDGE,"E694"),sQuery(id+"F0.wireOp",EDGE,"E695"),sQuery(id+"F0.wireOp",EDGE,"E696"),sQuery(id+"F0.wireOp",EDGE,"E697"),sQuery(id+"F0.wireOp",EDGE,"E698"),sQuery(id+"F0.wireOp",EDGE,"E699"),sQuery(id+"F0.wireOp",EDGE,"E700"),sQuery(id+"F0.wireOp",EDGE,"E701"),sQuery(id+"F0.wireOp",EDGE,"E702"),sQuery(id+"F0.wireOp",EDGE,"E703"),sQuery(id+"F0.wireOp",EDGE,"E704"),sQuery(id+"F0.wireOp",EDGE,"E705"),sQuery(id+"F0.wireOp",EDGE,"E706"),sQuery(id+"F0.wireOp",EDGE,"E707"),sQuery(id+"F0.wireOp",EDGE,"E708"),sQuery(id+"F0.wireOp",EDGE,"E709"),sQuery(id+"F0.wireOp",EDGE,"E710"),sQuery(id+"F0.wireOp",EDGE,"E711"),sQuery(id+"F0.wireOp",EDGE,"E712"),sQuery(id+"F0.wireOp",EDGE,"E713"),sQuery(id+"F0.wireOp",EDGE,"E714"),sQuery(id+"F0.wireOp",EDGE,"E715"),sQuery(id+"F0.wireOp",EDGE,"E716"),sQuery(id+"F0.wireOp",EDGE,"E717"),sQuery(id+"F0.wireOp",EDGE,"E718"),sQuery(id+"F0.wireOp",EDGE,"E719"),sQuery(id+"F0.wireOp",EDGE,"E720"),sQuery(id+"F0.wireOp",EDGE,"E721"),sQuery(id+"F0.wireOp",EDGE,"E722"),sQuery(id+"F0.wireOp",EDGE,"E723"),sQuery(id+"F0.wireOp",EDGE,"E724"),sQuery(id+"F0.wireOp",EDGE,"E725"),sQuery(id+"F0.wireOp",EDGE,"E726"),sQuery(id+"F0.wireOp",EDGE,"E727"),sQuery(id+"F0.wireOp",EDGE,"E728"),sQuery(id+"F0.wireOp",EDGE,"E729"),sQuery(id+"F0.wireOp",EDGE,"E730"),sQuery(id+"F0.wireOp",EDGE,"E731"),sQuery(id+"F0.wireOp",EDGE,"E732"),sQuery(id+"F0.wireOp",EDGE,"E733"),sQuery(id+"F0.wireOp",EDGE,"E734"),sQuery(id+"F0.wireOp",EDGE,"E735"),sQuery(id+"F0.wireOp",EDGE,"E736"),sQuery(id+"F0.wireOp",EDGE,"E737"),sQuery(id+"F0.wireOp",EDGE,"E738"),sQuery(id+"F0.wireOp",EDGE,"E739"),sQuery(id+"F0.wireOp",EDGE,"E740"),sQuery(id+"F0.wireOp",EDGE,"E741"),sQuery(id+"F0.wireOp",EDGE,"E742"),sQuery(id+"F0.wireOp",EDGE,"E743"),sQuery(id+"F0.wireOp",EDGE,"E744"),sQuery(id+"F0.wireOp",EDGE,"E745"),sQuery(id+"F0.wireOp",EDGE,"E746"),sQuery(id+"F0.wireOp",EDGE,"E747"),sQuery(id+"F0.wireOp",EDGE,"E748"),sQuery(id+"F0.wireOp",EDGE,"E749"),sQuery(id+"F0.wireOp",EDGE,"E750"),sQuery(id+"F0.wireOp",EDGE,"E751"),sQuery(id+"F0.wireOp",EDGE,"E752"),sQuery(id+"F0.wireOp",EDGE,"E753"),sQuery(id+"F0.wireOp",EDGE,"E754"),sQuery(id+"F0.wireOp",EDGE,"E755"),sQuery(id+"F0.wireOp",EDGE,"E756"),sQuery(id+"F0.wireOp",EDGE,"E757"),sQuery(id+"F0.wireOp",EDGE,"E758"),sQuery(id+"F0.wireOp",EDGE,"E759"),sQuery(id+"F0.wireOp",EDGE,"E760"),sQuery(id+"F0.wireOp",EDGE,"E761"),sQuery(id+"F0.wireOp",EDGE,"E762"),sQuery(id+"F0.wireOp",EDGE,"E763"),sQuery(id+"F0.wireOp",EDGE,"E764"),sQuery(id+"F0.wireOp",EDGE,"E765"),sQuery(id+"F0.wireOp",EDGE,"E766"),sQuery(id+"F0.wireOp",EDGE,"E767"),sQuery(id+"F0.wireOp",EDGE,"E768"),sQuery(id+"F0.wireOp",EDGE,"E769"),sQuery(id+"F0.wireOp",EDGE,"E770"),sQuery(id+"F0.wireOp",EDGE,"E771"),sQuery(id+"F0.wireOp",EDGE,"E772"),sQuery(id+"F0.wireOp",EDGE,"E773"),sQuery(id+"F0.wireOp",EDGE,"E774"),sQuery(id+"F0.wireOp",EDGE,"E775"),sQuery(id+"F0.wireOp",EDGE,"E776"),sQuery(id+"F0.wireOp",EDGE,"E777"),sQuery(id+"F0.wireOp",EDGE,"E778"),sQuery(id+"F0.wireOp",EDGE,"E779"),sQuery(id+"F0.wireOp",EDGE,"E780"),sQuery(id+"F0.wireOp",EDGE,"E781"),sQuery(id+"F0.wireOp",EDGE,"E782"),sQuery(id+"F0.wireOp",EDGE,"E783"),sQuery(id+"F0.wireOp",EDGE,"E784"),sQuery(id+"F0.wireOp",EDGE,"E785"),sQuery(id+"F0.wireOp",EDGE,"E786"),sQuery(id+"F0.wireOp",EDGE,"E787"),sQuery(id+"F0.wireOp",EDGE,"E788"),sQuery(id+"F0.wireOp",EDGE,"E789"),sQuery(id+"F0.wireOp",EDGE,"E790"),sQuery(id+"F0.wireOp",EDGE,"E791"),sQuery(id+"F0.wireOp",EDGE,"E792"),sQuery(id+"F0.wireOp",EDGE,"E793"),sQuery(id+"F0.wireOp",EDGE,"E794"),sQuery(id+"F0.wireOp",EDGE,"E795"),sQuery(id+"F0.wireOp",EDGE,"E796"),sQuery(id+"F0.wireOp",EDGE,"E797"),sQuery(id+"F0.wireOp",EDGE,"E798"),sQuery(id+"F0.wireOp",EDGE,"E799"),sQuery(id+"F0.wireOp",EDGE,"E800"),sQuery(id+"F0.wireOp",EDGE,"E801"),sQuery(id+"F0.wireOp",EDGE,"E802"),sQuery(id+"F0.wireOp",EDGE,"E803"),sQuery(id+"F0.wireOp",EDGE,"E804"),sQuery(id+"F0.wireOp",EDGE,"E805"),sQuery(id+"F0.wireOp",EDGE,"E806"),sQuery(id+"F0.wireOp",EDGE,"E807"),sQuery(id+"F0.wireOp",EDGE,"E808"),sQuery(id+"F0.wireOp",EDGE,"E809"),sQuery(id+"F0.wireOp",EDGE,"E810"),sQuery(id+"F0.wireOp",EDGE,"E811"),sQuery(id+"F0.wireOp",EDGE,"E812"),sQuery(id+"F0.wireOp",EDGE,"E813"),subQ4,sQuery(id+"F0.wireOp",EDGE,"E815"),sQuery(id+"F0.wireOp",EDGE,"E816")])],"isStart":false}),makeQuery(id+"F3.opExtrude","CAP_FACE",FACE,{"disambiguationData":[OSD([subQ8,subQ7,subQ6,sQuery(id+"F2.wireOp",EDGE,"E820"),sQuery(id+"F2.wireOp",EDGE,"E825")])],"isStart":true}),makeQuery(id+"F3.opExtrude","CAP_FACE",FACE,{"disambiguationData":[OSD([subQ5,subQ4,sQuery(id+"F2.wireOp",EDGE,"E821"),sQuery(id+"F2.wireOp",EDGE,"E824")])],"isStart":true}),makeQuery(id+"F3.opExtrude","CAP_FACE",FACE,{"disambiguationData":[OSD([subQ3,subQ2,subQ1,subQ0,sQuery(id+"F2.wireOp",EDGE,"E822"),sQuery(id+"F2.wireOp",EDGE,"E823")])],"isStart":true})]});}
            var Q1;
            {var subQ0=sQuery(id+"F0.wireOp",EDGE,"E550");var subQ1=sQuery(id+"F0.wireOp",EDGE,"E549");var subQ2=sQuery(id+"F0.wireOp",EDGE,"E545");var subQ3=sQuery(id+"F0.wireOp",EDGE,"E544");var subQ4=sQuery(id+"F0.wireOp",EDGE,"E814");var subQ5=sQuery(id+"F0.wireOp",EDGE,"E1");var subQ6=sQuery(id+"F0.wireOp",EDGE,"E271");var subQ7=sQuery(id+"F0.wireOp",EDGE,"E267");var subQ8=sQuery(id+"F0.wireOp",EDGE,"E266");Q1=makeQuery(id+"F3.boolean.opBoolean","MERGE",FACE,{"derivedFrom":[makeQuery(id+"F1.opExtrude","CAP_FACE",FACE,{"disambiguationData":[OSD([sQuery(id+"F0.wireOp",EDGE,"E0"),subQ5,sQuery(id+"F0.wireOp",EDGE,"E2"),sQuery(id+"F0.wireOp",EDGE,"E3"),sQuery(id+"F0.wireOp",EDGE,"E4"),sQuery(id+"F0.wireOp",EDGE,"E5"),sQuery(id+"F0.wireOp",EDGE,"E6"),sQuery(id+"F0.wireOp",EDGE,"E7"),sQuery(id+"F0.wireOp",EDGE,"E8"),sQuery(id+"F0.wireOp",EDGE,"E9"),sQuery(id+"F0.wireOp",EDGE,"E10"),sQuery(id+"F0.wireOp",EDGE,"E11"),sQuery(id+"F0.wireOp",EDGE,"E12"),sQuery(id+"F0.wireOp",EDGE,"E13"),sQuery(id+"F0.wireOp",EDGE,"E14"),sQuery(id+"F0.wireOp",EDGE,"E15"),sQuery(id+"F0.wireOp",EDGE,"E16"),sQuery(id+"F0.wireOp",EDGE,"E17"),sQuery(id+"F0.wireOp",EDGE,"E18"),sQuery(id+"F0.wireOp",EDGE,"E19"),sQuery(id+"F0.wireOp",EDGE,"E20"),sQuery(id+"F0.wireOp",EDGE,"E21"),sQuery(id+"F0.wireOp",EDGE,"E22"),sQuery(id+"F0.wireOp",EDGE,"E23"),sQuery(id+"F0.wireOp",EDGE,"E24"),sQuery(id+"F0.wireOp",EDGE,"E25"),sQuery(id+"F0.wireOp",EDGE,"E26"),sQuery(id+"F0.wireOp",EDGE,"E27"),sQuery(id+"F0.wireOp",EDGE,"E28"),sQuery(id+"F0.wireOp",EDGE,"E29"),sQuery(id+"F0.wireOp",EDGE,"E30"),sQuery(id+"F0.wireOp",EDGE,"E31"),sQuery(id+"F0.wireOp",EDGE,"E32"),sQuery(id+"F0.wireOp",EDGE,"E33"),sQuery(id+"F0.wireOp",EDGE,"E34"),sQuery(id+"F0.wireOp",EDGE,"E35"),sQuery(id+"F0.wireOp",EDGE,"E36"),sQuery(id+"F0.wireOp",EDGE,"E37"),sQuery(id+"F0.wireOp",EDGE,"E38"),sQuery(id+"F0.wireOp",EDGE,"E39"),sQuery(id+"F0.wireOp",EDGE,"E40"),sQuery(id+"F0.wireOp",EDGE,"E41"),sQuery(id+"F0.wireOp",EDGE,"E42"),sQuery(id+"F0.wireOp",EDGE,"E43"),sQuery(id+"F0.wireOp",EDGE,"E44"),sQuery(id+"F0.wireOp",EDGE,"E45"),sQuery(id+"F0.wireOp",EDGE,"E46"),sQuery(id+"F0.wireOp",EDGE,"E47"),sQuery(id+"F0.wireOp",EDGE,"E48"),sQuery(id+"F0.wireOp",EDGE,"E49"),sQuery(id+"F0.wireOp",EDGE,"E50"),sQuery(id+"F0.wireOp",EDGE,"E51"),sQuery(id+"F0.wireOp",EDGE,"E52"),sQuery(id+"F0.wireOp",EDGE,"E53"),sQuery(id+"F0.wireOp",EDGE,"E54"),sQuery(id+"F0.wireOp",EDGE,"E55"),sQuery(id+"F0.wireOp",EDGE,"E56"),sQuery(id+"F0.wireOp",EDGE,"E57"),sQuery(id+"F0.wireOp",EDGE,"E58"),sQuery(id+"F0.wireOp",EDGE,"E59"),sQuery(id+"F0.wireOp",EDGE,"E60"),sQuery(id+"F0.wireOp",EDGE,"E61"),sQuery(id+"F0.wireOp",EDGE,"E62"),sQuery(id+"F0.wireOp",EDGE,"E63"),sQuery(id+"F0.wireOp",EDGE,"E64"),sQuery(id+"F0.wireOp",EDGE,"E65"),sQuery(id+"F0.wireOp",EDGE,"E66"),sQuery(id+"F0.wireOp",EDGE,"E67"),sQuery(id+"F0.wireOp",EDGE,"E68"),sQuery(id+"F0.wireOp",EDGE,"E69"),sQuery(id+"F0.wireOp",EDGE,"E70"),sQuery(id+"F0.wireOp",EDGE,"E71"),sQuery(id+"F0.wireOp",EDGE,"E72"),sQuery(id+"F0.wireOp",EDGE,"E73"),sQuery(id+"F0.wireOp",EDGE,"E74"),sQuery(id+"F0.wireOp",EDGE,"E75"),sQuery(id+"F0.wireOp",EDGE,"E76"),sQuery(id+"F0.wireOp",EDGE,"E77"),sQuery(id+"F0.wireOp",EDGE,"E78"),sQuery(id+"F0.wireOp",EDGE,"E79"),sQuery(id+"F0.wireOp",EDGE,"E80"),sQuery(id+"F0.wireOp",EDGE,"E81"),sQuery(id+"F0.wireOp",EDGE,"E82"),sQuery(id+"F0.wireOp",EDGE,"E83"),sQuery(id+"F0.wireOp",EDGE,"E84"),sQuery(id+"F0.wireOp",EDGE,"E85"),sQuery(id+"F0.wireOp",EDGE,"E86"),sQuery(id+"F0.wireOp",EDGE,"E87"),sQuery(id+"F0.wireOp",EDGE,"E88"),sQuery(id+"F0.wireOp",EDGE,"E89"),sQuery(id+"F0.wireOp",EDGE,"E90"),sQuery(id+"F0.wireOp",EDGE,"E91"),sQuery(id+"F0.wireOp",EDGE,"E92"),sQuery(id+"F0.wireOp",EDGE,"E93"),sQuery(id+"F0.wireOp",EDGE,"E94"),sQuery(id+"F0.wireOp",EDGE,"E95"),sQuery(id+"F0.wireOp",EDGE,"E96"),sQuery(id+"F0.wireOp",EDGE,"E97"),sQuery(id+"F0.wireOp",EDGE,"E98"),sQuery(id+"F0.wireOp",EDGE,"E99"),sQuery(id+"F0.wireOp",EDGE,"E100"),sQuery(id+"F0.wireOp",EDGE,"E101"),sQuery(id+"F0.wireOp",EDGE,"E102"),sQuery(id+"F0.wireOp",EDGE,"E103"),sQuery(id+"F0.wireOp",EDGE,"E104"),sQuery(id+"F0.wireOp",EDGE,"E105"),sQuery(id+"F0.wireOp",EDGE,"E106"),sQuery(id+"F0.wireOp",EDGE,"E107"),sQuery(id+"F0.wireOp",EDGE,"E108"),sQuery(id+"F0.wireOp",EDGE,"E109"),sQuery(id+"F0.wireOp",EDGE,"E110"),sQuery(id+"F0.wireOp",EDGE,"E111"),sQuery(id+"F0.wireOp",EDGE,"E112"),sQuery(id+"F0.wireOp",EDGE,"E113"),sQuery(id+"F0.wireOp",EDGE,"E114"),sQuery(id+"F0.wireOp",EDGE,"E115"),sQuery(id+"F0.wireOp",EDGE,"E116"),sQuery(id+"F0.wireOp",EDGE,"E117"),sQuery(id+"F0.wireOp",EDGE,"E118"),sQuery(id+"F0.wireOp",EDGE,"E119"),sQuery(id+"F0.wireOp",EDGE,"E120"),sQuery(id+"F0.wireOp",EDGE,"E121"),sQuery(id+"F0.wireOp",EDGE,"E122"),sQuery(id+"F0.wireOp",EDGE,"E123"),sQuery(id+"F0.wireOp",EDGE,"E124"),sQuery(id+"F0.wireOp",EDGE,"E125"),sQuery(id+"F0.wireOp",EDGE,"E126"),sQuery(id+"F0.wireOp",EDGE,"E127"),sQuery(id+"F0.wireOp",EDGE,"E128"),sQuery(id+"F0.wireOp",EDGE,"E129"),sQuery(id+"F0.wireOp",EDGE,"E130"),sQuery(id+"F0.wireOp",EDGE,"E131"),sQuery(id+"F0.wireOp",EDGE,"E132"),sQuery(id+"F0.wireOp",EDGE,"E133"),sQuery(id+"F0.wireOp",EDGE,"E134"),sQuery(id+"F0.wireOp",EDGE,"E135"),sQuery(id+"F0.wireOp",EDGE,"E136"),sQuery(id+"F0.wireOp",EDGE,"E137"),sQuery(id+"F0.wireOp",EDGE,"E138"),sQuery(id+"F0.wireOp",EDGE,"E139"),sQuery(id+"F0.wireOp",EDGE,"E140"),sQuery(id+"F0.wireOp",EDGE,"E141"),sQuery(id+"F0.wireOp",EDGE,"E142"),sQuery(id+"F0.wireOp",EDGE,"E143"),sQuery(id+"F0.wireOp",EDGE,"E144"),sQuery(id+"F0.wireOp",EDGE,"E145"),sQuery(id+"F0.wireOp",EDGE,"E146"),sQuery(id+"F0.wireOp",EDGE,"E147"),sQuery(id+"F0.wireOp",EDGE,"E148"),sQuery(id+"F0.wireOp",EDGE,"E149"),sQuery(id+"F0.wireOp",EDGE,"E150"),sQuery(id+"F0.wireOp",EDGE,"E151"),sQuery(id+"F0.wireOp",EDGE,"E152"),sQuery(id+"F0.wireOp",EDGE,"E153"),sQuery(id+"F0.wireOp",EDGE,"E154"),sQuery(id+"F0.wireOp",EDGE,"E155"),sQuery(id+"F0.wireOp",EDGE,"E156"),sQuery(id+"F0.wireOp",EDGE,"E157"),sQuery(id+"F0.wireOp",EDGE,"E158"),sQuery(id+"F0.wireOp",EDGE,"E159"),sQuery(id+"F0.wireOp",EDGE,"E160"),sQuery(id+"F0.wireOp",EDGE,"E161"),sQuery(id+"F0.wireOp",EDGE,"E162"),sQuery(id+"F0.wireOp",EDGE,"E163"),sQuery(id+"F0.wireOp",EDGE,"E164"),sQuery(id+"F0.wireOp",EDGE,"E165"),sQuery(id+"F0.wireOp",EDGE,"E166"),sQuery(id+"F0.wireOp",EDGE,"E167"),sQuery(id+"F0.wireOp",EDGE,"E168"),sQuery(id+"F0.wireOp",EDGE,"E169"),sQuery(id+"F0.wireOp",EDGE,"E170"),sQuery(id+"F0.wireOp",EDGE,"E171"),sQuery(id+"F0.wireOp",EDGE,"E172"),sQuery(id+"F0.wireOp",EDGE,"E173"),sQuery(id+"F0.wireOp",EDGE,"E174"),sQuery(id+"F0.wireOp",EDGE,"E175"),sQuery(id+"F0.wireOp",EDGE,"E176"),sQuery(id+"F0.wireOp",EDGE,"E177"),sQuery(id+"F0.wireOp",EDGE,"E178"),sQuery(id+"F0.wireOp",EDGE,"E179"),sQuery(id+"F0.wireOp",EDGE,"E180"),sQuery(id+"F0.wireOp",EDGE,"E181"),sQuery(id+"F0.wireOp",EDGE,"E182"),sQuery(id+"F0.wireOp",EDGE,"E183"),sQuery(id+"F0.wireOp",EDGE,"E184"),sQuery(id+"F0.wireOp",EDGE,"E185"),sQuery(id+"F0.wireOp",EDGE,"E186"),sQuery(id+"F0.wireOp",EDGE,"E187"),sQuery(id+"F0.wireOp",EDGE,"E188"),sQuery(id+"F0.wireOp",EDGE,"E189"),sQuery(id+"F0.wireOp",EDGE,"E190"),sQuery(id+"F0.wireOp",EDGE,"E191"),sQuery(id+"F0.wireOp",EDGE,"E192"),sQuery(id+"F0.wireOp",EDGE,"E193"),sQuery(id+"F0.wireOp",EDGE,"E194"),sQuery(id+"F0.wireOp",EDGE,"E195"),sQuery(id+"F0.wireOp",EDGE,"E196"),sQuery(id+"F0.wireOp",EDGE,"E197"),sQuery(id+"F0.wireOp",EDGE,"E198"),sQuery(id+"F0.wireOp",EDGE,"E199"),sQuery(id+"F0.wireOp",EDGE,"E200"),sQuery(id+"F0.wireOp",EDGE,"E201"),sQuery(id+"F0.wireOp",EDGE,"E202"),sQuery(id+"F0.wireOp",EDGE,"E203"),sQuery(id+"F0.wireOp",EDGE,"E204"),sQuery(id+"F0.wireOp",EDGE,"E205"),sQuery(id+"F0.wireOp",EDGE,"E206"),sQuery(id+"F0.wireOp",EDGE,"E207"),sQuery(id+"F0.wireOp",EDGE,"E208"),sQuery(id+"F0.wireOp",EDGE,"E209"),sQuery(id+"F0.wireOp",EDGE,"E210"),sQuery(id+"F0.wireOp",EDGE,"E211"),sQuery(id+"F0.wireOp",EDGE,"E212"),sQuery(id+"F0.wireOp",EDGE,"E213"),sQuery(id+"F0.wireOp",EDGE,"E214"),sQuery(id+"F0.wireOp",EDGE,"E215"),sQuery(id+"F0.wireOp",EDGE,"E216"),sQuery(id+"F0.wireOp",EDGE,"E217"),sQuery(id+"F0.wireOp",EDGE,"E218"),sQuery(id+"F0.wireOp",EDGE,"E219"),sQuery(id+"F0.wireOp",EDGE,"E220"),sQuery(id+"F0.wireOp",EDGE,"E221"),sQuery(id+"F0.wireOp",EDGE,"E222"),sQuery(id+"F0.wireOp",EDGE,"E223"),sQuery(id+"F0.wireOp",EDGE,"E224"),sQuery(id+"F0.wireOp",EDGE,"E225"),sQuery(id+"F0.wireOp",EDGE,"E226"),sQuery(id+"F0.wireOp",EDGE,"E227"),sQuery(id+"F0.wireOp",EDGE,"E228"),sQuery(id+"F0.wireOp",EDGE,"E229"),sQuery(id+"F0.wireOp",EDGE,"E230"),sQuery(id+"F0.wireOp",EDGE,"E231"),sQuery(id+"F0.wireOp",EDGE,"E232"),sQuery(id+"F0.wireOp",EDGE,"E233"),sQuery(id+"F0.wireOp",EDGE,"E234"),sQuery(id+"F0.wireOp",EDGE,"E235"),sQuery(id+"F0.wireOp",EDGE,"E236"),sQuery(id+"F0.wireOp",EDGE,"E237"),sQuery(id+"F0.wireOp",EDGE,"E238"),sQuery(id+"F0.wireOp",EDGE,"E239"),sQuery(id+"F0.wireOp",EDGE,"E240"),sQuery(id+"F0.wireOp",EDGE,"E241"),sQuery(id+"F0.wireOp",EDGE,"E242"),sQuery(id+"F0.wireOp",EDGE,"E243"),sQuery(id+"F0.wireOp",EDGE,"E244"),sQuery(id+"F0.wireOp",EDGE,"E245"),sQuery(id+"F0.wireOp",EDGE,"E246"),sQuery(id+"F0.wireOp",EDGE,"E247"),sQuery(id+"F0.wireOp",EDGE,"E248"),sQuery(id+"F0.wireOp",EDGE,"E249"),sQuery(id+"F0.wireOp",EDGE,"E250"),sQuery(id+"F0.wireOp",EDGE,"E251"),sQuery(id+"F0.wireOp",EDGE,"E252"),sQuery(id+"F0.wireOp",EDGE,"E253"),sQuery(id+"F0.wireOp",EDGE,"E254"),sQuery(id+"F0.wireOp",EDGE,"E255"),sQuery(id+"F0.wireOp",EDGE,"E256"),sQuery(id+"F0.wireOp",EDGE,"E257"),sQuery(id+"F0.wireOp",EDGE,"E258"),sQuery(id+"F0.wireOp",EDGE,"E259"),sQuery(id+"F0.wireOp",EDGE,"E260"),sQuery(id+"F0.wireOp",EDGE,"E261"),sQuery(id+"F0.wireOp",EDGE,"E262"),sQuery(id+"F0.wireOp",EDGE,"E263"),sQuery(id+"F0.wireOp",EDGE,"E264"),sQuery(id+"F0.wireOp",EDGE,"E265"),subQ8,subQ7,sQuery(id+"F0.wireOp",EDGE,"E268"),sQuery(id+"F0.wireOp",EDGE,"E269"),sQuery(id+"F0.wireOp",EDGE,"E270"),subQ6,sQuery(id+"F0.wireOp",EDGE,"E272"),sQuery(id+"F0.wireOp",EDGE,"E273"),sQuery(id+"F0.wireOp",EDGE,"E274"),sQuery(id+"F0.wireOp",EDGE,"E275"),sQuery(id+"F0.wireOp",EDGE,"E276"),sQuery(id+"F0.wireOp",EDGE,"E277"),sQuery(id+"F0.wireOp",EDGE,"E278"),sQuery(id+"F0.wireOp",EDGE,"E279"),sQuery(id+"F0.wireOp",EDGE,"E280"),sQuery(id+"F0.wireOp",EDGE,"E281"),sQuery(id+"F0.wireOp",EDGE,"E282"),sQuery(id+"F0.wireOp",EDGE,"E283"),sQuery(id+"F0.wireOp",EDGE,"E284"),sQuery(id+"F0.wireOp",EDGE,"E285"),sQuery(id+"F0.wireOp",EDGE,"E286"),sQuery(id+"F0.wireOp",EDGE,"E287"),sQuery(id+"F0.wireOp",EDGE,"E288"),sQuery(id+"F0.wireOp",EDGE,"E289"),sQuery(id+"F0.wireOp",EDGE,"E290"),sQuery(id+"F0.wireOp",EDGE,"E291"),sQuery(id+"F0.wireOp",EDGE,"E292"),sQuery(id+"F0.wireOp",EDGE,"E293"),sQuery(id+"F0.wireOp",EDGE,"E294"),sQuery(id+"F0.wireOp",EDGE,"E295"),sQuery(id+"F0.wireOp",EDGE,"E296"),sQuery(id+"F0.wireOp",EDGE,"E297"),sQuery(id+"F0.wireOp",EDGE,"E298"),sQuery(id+"F0.wireOp",EDGE,"E299"),sQuery(id+"F0.wireOp",EDGE,"E300"),sQuery(id+"F0.wireOp",EDGE,"E301"),sQuery(id+"F0.wireOp",EDGE,"E302"),sQuery(id+"F0.wireOp",EDGE,"E303"),sQuery(id+"F0.wireOp",EDGE,"E304"),sQuery(id+"F0.wireOp",EDGE,"E305"),sQuery(id+"F0.wireOp",EDGE,"E306"),sQuery(id+"F0.wireOp",EDGE,"E307"),sQuery(id+"F0.wireOp",EDGE,"E308"),sQuery(id+"F0.wireOp",EDGE,"E309"),sQuery(id+"F0.wireOp",EDGE,"E310"),sQuery(id+"F0.wireOp",EDGE,"E311"),sQuery(id+"F0.wireOp",EDGE,"E312"),sQuery(id+"F0.wireOp",EDGE,"E313"),sQuery(id+"F0.wireOp",EDGE,"E314"),sQuery(id+"F0.wireOp",EDGE,"E315"),sQuery(id+"F0.wireOp",EDGE,"E316"),sQuery(id+"F0.wireOp",EDGE,"E317"),sQuery(id+"F0.wireOp",EDGE,"E318"),sQuery(id+"F0.wireOp",EDGE,"E319"),sQuery(id+"F0.wireOp",EDGE,"E320"),sQuery(id+"F0.wireOp",EDGE,"E321"),sQuery(id+"F0.wireOp",EDGE,"E322"),sQuery(id+"F0.wireOp",EDGE,"E323"),sQuery(id+"F0.wireOp",EDGE,"E324"),sQuery(id+"F0.wireOp",EDGE,"E325"),sQuery(id+"F0.wireOp",EDGE,"E326"),sQuery(id+"F0.wireOp",EDGE,"E327"),sQuery(id+"F0.wireOp",EDGE,"E328"),sQuery(id+"F0.wireOp",EDGE,"E329"),sQuery(id+"F0.wireOp",EDGE,"E330"),sQuery(id+"F0.wireOp",EDGE,"E331"),sQuery(id+"F0.wireOp",EDGE,"E332"),sQuery(id+"F0.wireOp",EDGE,"E333"),sQuery(id+"F0.wireOp",EDGE,"E334"),sQuery(id+"F0.wireOp",EDGE,"E335"),sQuery(id+"F0.wireOp",EDGE,"E336"),sQuery(id+"F0.wireOp",EDGE,"E337"),sQuery(id+"F0.wireOp",EDGE,"E338"),sQuery(id+"F0.wireOp",EDGE,"E339"),sQuery(id+"F0.wireOp",EDGE,"E340"),sQuery(id+"F0.wireOp",EDGE,"E341"),sQuery(id+"F0.wireOp",EDGE,"E342"),sQuery(id+"F0.wireOp",EDGE,"E343"),sQuery(id+"F0.wireOp",EDGE,"E344"),sQuery(id+"F0.wireOp",EDGE,"E345"),sQuery(id+"F0.wireOp",EDGE,"E346"),sQuery(id+"F0.wireOp",EDGE,"E347"),sQuery(id+"F0.wireOp",EDGE,"E348"),sQuery(id+"F0.wireOp",EDGE,"E349"),sQuery(id+"F0.wireOp",EDGE,"E350"),sQuery(id+"F0.wireOp",EDGE,"E351"),sQuery(id+"F0.wireOp",EDGE,"E352"),sQuery(id+"F0.wireOp",EDGE,"E353"),sQuery(id+"F0.wireOp",EDGE,"E354"),sQuery(id+"F0.wireOp",EDGE,"E355"),sQuery(id+"F0.wireOp",EDGE,"E356"),sQuery(id+"F0.wireOp",EDGE,"E357"),sQuery(id+"F0.wireOp",EDGE,"E358"),sQuery(id+"F0.wireOp",EDGE,"E359"),sQuery(id+"F0.wireOp",EDGE,"E360"),sQuery(id+"F0.wireOp",EDGE,"E361"),sQuery(id+"F0.wireOp",EDGE,"E362"),sQuery(id+"F0.wireOp",EDGE,"E363"),sQuery(id+"F0.wireOp",EDGE,"E364"),sQuery(id+"F0.wireOp",EDGE,"E365"),sQuery(id+"F0.wireOp",EDGE,"E366"),sQuery(id+"F0.wireOp",EDGE,"E367"),sQuery(id+"F0.wireOp",EDGE,"E368"),sQuery(id+"F0.wireOp",EDGE,"E369"),sQuery(id+"F0.wireOp",EDGE,"E370"),sQuery(id+"F0.wireOp",EDGE,"E371"),sQuery(id+"F0.wireOp",EDGE,"E372"),sQuery(id+"F0.wireOp",EDGE,"E373"),sQuery(id+"F0.wireOp",EDGE,"E374"),sQuery(id+"F0.wireOp",EDGE,"E375"),sQuery(id+"F0.wireOp",EDGE,"E376"),sQuery(id+"F0.wireOp",EDGE,"E377"),sQuery(id+"F0.wireOp",EDGE,"E378"),sQuery(id+"F0.wireOp",EDGE,"E379"),sQuery(id+"F0.wireOp",EDGE,"E380"),sQuery(id+"F0.wireOp",EDGE,"E381"),sQuery(id+"F0.wireOp",EDGE,"E382"),sQuery(id+"F0.wireOp",EDGE,"E383"),sQuery(id+"F0.wireOp",EDGE,"E384"),sQuery(id+"F0.wireOp",EDGE,"E385"),sQuery(id+"F0.wireOp",EDGE,"E386"),sQuery(id+"F0.wireOp",EDGE,"E387"),sQuery(id+"F0.wireOp",EDGE,"E388"),sQuery(id+"F0.wireOp",EDGE,"E389"),sQuery(id+"F0.wireOp",EDGE,"E390"),sQuery(id+"F0.wireOp",EDGE,"E391"),sQuery(id+"F0.wireOp",EDGE,"E392"),sQuery(id+"F0.wireOp",EDGE,"E393"),sQuery(id+"F0.wireOp",EDGE,"E394"),sQuery(id+"F0.wireOp",EDGE,"E395"),sQuery(id+"F0.wireOp",EDGE,"E396"),sQuery(id+"F0.wireOp",EDGE,"E397"),sQuery(id+"F0.wireOp",EDGE,"E398"),sQuery(id+"F0.wireOp",EDGE,"E399"),sQuery(id+"F0.wireOp",EDGE,"E400"),sQuery(id+"F0.wireOp",EDGE,"E401"),sQuery(id+"F0.wireOp",EDGE,"E402"),sQuery(id+"F0.wireOp",EDGE,"E403"),sQuery(id+"F0.wireOp",EDGE,"E404"),sQuery(id+"F0.wireOp",EDGE,"E405"),sQuery(id+"F0.wireOp",EDGE,"E406"),sQuery(id+"F0.wireOp",EDGE,"E407"),sQuery(id+"F0.wireOp",EDGE,"E408"),sQuery(id+"F0.wireOp",EDGE,"E409"),sQuery(id+"F0.wireOp",EDGE,"E410"),sQuery(id+"F0.wireOp",EDGE,"E411"),sQuery(id+"F0.wireOp",EDGE,"E412"),sQuery(id+"F0.wireOp",EDGE,"E413"),sQuery(id+"F0.wireOp",EDGE,"E414"),sQuery(id+"F0.wireOp",EDGE,"E415"),sQuery(id+"F0.wireOp",EDGE,"E416"),sQuery(id+"F0.wireOp",EDGE,"E417"),sQuery(id+"F0.wireOp",EDGE,"E418"),sQuery(id+"F0.wireOp",EDGE,"E419"),sQuery(id+"F0.wireOp",EDGE,"E420"),sQuery(id+"F0.wireOp",EDGE,"E421"),sQuery(id+"F0.wireOp",EDGE,"E422"),sQuery(id+"F0.wireOp",EDGE,"E423"),sQuery(id+"F0.wireOp",EDGE,"E424"),sQuery(id+"F0.wireOp",EDGE,"E425"),sQuery(id+"F0.wireOp",EDGE,"E426"),sQuery(id+"F0.wireOp",EDGE,"E427"),sQuery(id+"F0.wireOp",EDGE,"E428"),sQuery(id+"F0.wireOp",EDGE,"E429"),sQuery(id+"F0.wireOp",EDGE,"E430"),sQuery(id+"F0.wireOp",EDGE,"E431"),sQuery(id+"F0.wireOp",EDGE,"E432"),sQuery(id+"F0.wireOp",EDGE,"E433"),sQuery(id+"F0.wireOp",EDGE,"E434"),sQuery(id+"F0.wireOp",EDGE,"E435"),sQuery(id+"F0.wireOp",EDGE,"E436"),sQuery(id+"F0.wireOp",EDGE,"E437"),sQuery(id+"F0.wireOp",EDGE,"E438"),sQuery(id+"F0.wireOp",EDGE,"E439"),sQuery(id+"F0.wireOp",EDGE,"E440"),sQuery(id+"F0.wireOp",EDGE,"E441"),sQuery(id+"F0.wireOp",EDGE,"E442"),sQuery(id+"F0.wireOp",EDGE,"E443"),sQuery(id+"F0.wireOp",EDGE,"E444"),sQuery(id+"F0.wireOp",EDGE,"E445"),sQuery(id+"F0.wireOp",EDGE,"E446"),sQuery(id+"F0.wireOp",EDGE,"E447"),sQuery(id+"F0.wireOp",EDGE,"E448"),sQuery(id+"F0.wireOp",EDGE,"E449"),sQuery(id+"F0.wireOp",EDGE,"E450"),sQuery(id+"F0.wireOp",EDGE,"E451"),sQuery(id+"F0.wireOp",EDGE,"E452"),sQuery(id+"F0.wireOp",EDGE,"E453"),sQuery(id+"F0.wireOp",EDGE,"E454"),sQuery(id+"F0.wireOp",EDGE,"E455"),sQuery(id+"F0.wireOp",EDGE,"E456"),sQuery(id+"F0.wireOp",EDGE,"E457"),sQuery(id+"F0.wireOp",EDGE,"E458"),sQuery(id+"F0.wireOp",EDGE,"E459"),sQuery(id+"F0.wireOp",EDGE,"E460"),sQuery(id+"F0.wireOp",EDGE,"E461"),sQuery(id+"F0.wireOp",EDGE,"E462"),sQuery(id+"F0.wireOp",EDGE,"E463"),sQuery(id+"F0.wireOp",EDGE,"E464"),sQuery(id+"F0.wireOp",EDGE,"E465"),sQuery(id+"F0.wireOp",EDGE,"E466"),sQuery(id+"F0.wireOp",EDGE,"E467"),sQuery(id+"F0.wireOp",EDGE,"E468"),sQuery(id+"F0.wireOp",EDGE,"E469"),sQuery(id+"F0.wireOp",EDGE,"E470"),sQuery(id+"F0.wireOp",EDGE,"E471"),sQuery(id+"F0.wireOp",EDGE,"E472"),sQuery(id+"F0.wireOp",EDGE,"E473"),sQuery(id+"F0.wireOp",EDGE,"E474"),sQuery(id+"F0.wireOp",EDGE,"E475"),sQuery(id+"F0.wireOp",EDGE,"E476"),sQuery(id+"F0.wireOp",EDGE,"E477"),sQuery(id+"F0.wireOp",EDGE,"E478"),sQuery(id+"F0.wireOp",EDGE,"E479"),sQuery(id+"F0.wireOp",EDGE,"E480"),sQuery(id+"F0.wireOp",EDGE,"E481"),sQuery(id+"F0.wireOp",EDGE,"E482"),sQuery(id+"F0.wireOp",EDGE,"E483"),sQuery(id+"F0.wireOp",EDGE,"E484"),sQuery(id+"F0.wireOp",EDGE,"E485"),sQuery(id+"F0.wireOp",EDGE,"E486"),sQuery(id+"F0.wireOp",EDGE,"E487"),sQuery(id+"F0.wireOp",EDGE,"E488"),sQuery(id+"F0.wireOp",EDGE,"E489"),sQuery(id+"F0.wireOp",EDGE,"E490"),sQuery(id+"F0.wireOp",EDGE,"E491"),sQuery(id+"F0.wireOp",EDGE,"E492"),sQuery(id+"F0.wireOp",EDGE,"E493"),sQuery(id+"F0.wireOp",EDGE,"E494"),sQuery(id+"F0.wireOp",EDGE,"E495"),sQuery(id+"F0.wireOp",EDGE,"E496"),sQuery(id+"F0.wireOp",EDGE,"E497"),sQuery(id+"F0.wireOp",EDGE,"E498"),sQuery(id+"F0.wireOp",EDGE,"E499"),sQuery(id+"F0.wireOp",EDGE,"E500"),sQuery(id+"F0.wireOp",EDGE,"E501"),sQuery(id+"F0.wireOp",EDGE,"E502"),sQuery(id+"F0.wireOp",EDGE,"E503"),sQuery(id+"F0.wireOp",EDGE,"E504"),sQuery(id+"F0.wireOp",EDGE,"E505"),sQuery(id+"F0.wireOp",EDGE,"E506"),sQuery(id+"F0.wireOp",EDGE,"E507"),sQuery(id+"F0.wireOp",EDGE,"E508"),sQuery(id+"F0.wireOp",EDGE,"E509"),sQuery(id+"F0.wireOp",EDGE,"E510"),sQuery(id+"F0.wireOp",EDGE,"E511"),sQuery(id+"F0.wireOp",EDGE,"E512"),sQuery(id+"F0.wireOp",EDGE,"E513"),sQuery(id+"F0.wireOp",EDGE,"E514"),sQuery(id+"F0.wireOp",EDGE,"E515"),sQuery(id+"F0.wireOp",EDGE,"E516"),sQuery(id+"F0.wireOp",EDGE,"E517"),sQuery(id+"F0.wireOp",EDGE,"E518"),sQuery(id+"F0.wireOp",EDGE,"E519"),sQuery(id+"F0.wireOp",EDGE,"E520"),sQuery(id+"F0.wireOp",EDGE,"E521"),sQuery(id+"F0.wireOp",EDGE,"E522"),sQuery(id+"F0.wireOp",EDGE,"E523"),sQuery(id+"F0.wireOp",EDGE,"E524"),sQuery(id+"F0.wireOp",EDGE,"E525"),sQuery(id+"F0.wireOp",EDGE,"E526"),sQuery(id+"F0.wireOp",EDGE,"E527"),sQuery(id+"F0.wireOp",EDGE,"E528"),sQuery(id+"F0.wireOp",EDGE,"E529"),sQuery(id+"F0.wireOp",EDGE,"E530"),sQuery(id+"F0.wireOp",EDGE,"E531"),sQuery(id+"F0.wireOp",EDGE,"E532"),sQuery(id+"F0.wireOp",EDGE,"E533"),sQuery(id+"F0.wireOp",EDGE,"E534"),sQuery(id+"F0.wireOp",EDGE,"E535"),sQuery(id+"F0.wireOp",EDGE,"E536"),sQuery(id+"F0.wireOp",EDGE,"E537"),sQuery(id+"F0.wireOp",EDGE,"E538"),sQuery(id+"F0.wireOp",EDGE,"E539"),sQuery(id+"F0.wireOp",EDGE,"E540"),sQuery(id+"F0.wireOp",EDGE,"E541"),sQuery(id+"F0.wireOp",EDGE,"E542"),sQuery(id+"F0.wireOp",EDGE,"E543"),subQ3,subQ2,sQuery(id+"F0.wireOp",EDGE,"E546"),sQuery(id+"F0.wireOp",EDGE,"E547"),sQuery(id+"F0.wireOp",EDGE,"E548"),subQ1,subQ0,sQuery(id+"F0.wireOp",EDGE,"E551"),sQuery(id+"F0.wireOp",EDGE,"E552"),sQuery(id+"F0.wireOp",EDGE,"E553"),sQuery(id+"F0.wireOp",EDGE,"E554"),sQuery(id+"F0.wireOp",EDGE,"E555"),sQuery(id+"F0.wireOp",EDGE,"E556"),sQuery(id+"F0.wireOp",EDGE,"E557"),sQuery(id+"F0.wireOp",EDGE,"E558"),sQuery(id+"F0.wireOp",EDGE,"E559"),sQuery(id+"F0.wireOp",EDGE,"E560"),sQuery(id+"F0.wireOp",EDGE,"E561"),sQuery(id+"F0.wireOp",EDGE,"E562"),sQuery(id+"F0.wireOp",EDGE,"E563"),sQuery(id+"F0.wireOp",EDGE,"E564"),sQuery(id+"F0.wireOp",EDGE,"E565"),sQuery(id+"F0.wireOp",EDGE,"E566"),sQuery(id+"F0.wireOp",EDGE,"E567"),sQuery(id+"F0.wireOp",EDGE,"E568"),sQuery(id+"F0.wireOp",EDGE,"E569"),sQuery(id+"F0.wireOp",EDGE,"E570"),sQuery(id+"F0.wireOp",EDGE,"E571"),sQuery(id+"F0.wireOp",EDGE,"E572"),sQuery(id+"F0.wireOp",EDGE,"E573"),sQuery(id+"F0.wireOp",EDGE,"E574"),sQuery(id+"F0.wireOp",EDGE,"E575"),sQuery(id+"F0.wireOp",EDGE,"E576"),sQuery(id+"F0.wireOp",EDGE,"E577"),sQuery(id+"F0.wireOp",EDGE,"E578"),sQuery(id+"F0.wireOp",EDGE,"E579"),sQuery(id+"F0.wireOp",EDGE,"E580"),sQuery(id+"F0.wireOp",EDGE,"E581"),sQuery(id+"F0.wireOp",EDGE,"E582"),sQuery(id+"F0.wireOp",EDGE,"E583"),sQuery(id+"F0.wireOp",EDGE,"E584"),sQuery(id+"F0.wireOp",EDGE,"E585"),sQuery(id+"F0.wireOp",EDGE,"E586"),sQuery(id+"F0.wireOp",EDGE,"E587"),sQuery(id+"F0.wireOp",EDGE,"E588"),sQuery(id+"F0.wireOp",EDGE,"E589"),sQuery(id+"F0.wireOp",EDGE,"E590"),sQuery(id+"F0.wireOp",EDGE,"E591"),sQuery(id+"F0.wireOp",EDGE,"E592"),sQuery(id+"F0.wireOp",EDGE,"E593"),sQuery(id+"F0.wireOp",EDGE,"E594"),sQuery(id+"F0.wireOp",EDGE,"E595"),sQuery(id+"F0.wireOp",EDGE,"E596"),sQuery(id+"F0.wireOp",EDGE,"E597"),sQuery(id+"F0.wireOp",EDGE,"E598"),sQuery(id+"F0.wireOp",EDGE,"E599"),sQuery(id+"F0.wireOp",EDGE,"E600"),sQuery(id+"F0.wireOp",EDGE,"E601"),sQuery(id+"F0.wireOp",EDGE,"E602"),sQuery(id+"F0.wireOp",EDGE,"E603"),sQuery(id+"F0.wireOp",EDGE,"E604"),sQuery(id+"F0.wireOp",EDGE,"E605"),sQuery(id+"F0.wireOp",EDGE,"E606"),sQuery(id+"F0.wireOp",EDGE,"E607"),sQuery(id+"F0.wireOp",EDGE,"E608"),sQuery(id+"F0.wireOp",EDGE,"E609"),sQuery(id+"F0.wireOp",EDGE,"E610"),sQuery(id+"F0.wireOp",EDGE,"E611"),sQuery(id+"F0.wireOp",EDGE,"E612"),sQuery(id+"F0.wireOp",EDGE,"E613"),sQuery(id+"F0.wireOp",EDGE,"E614"),sQuery(id+"F0.wireOp",EDGE,"E615"),sQuery(id+"F0.wireOp",EDGE,"E616"),sQuery(id+"F0.wireOp",EDGE,"E617"),sQuery(id+"F0.wireOp",EDGE,"E618"),sQuery(id+"F0.wireOp",EDGE,"E619"),sQuery(id+"F0.wireOp",EDGE,"E620"),sQuery(id+"F0.wireOp",EDGE,"E621"),sQuery(id+"F0.wireOp",EDGE,"E622"),sQuery(id+"F0.wireOp",EDGE,"E623"),sQuery(id+"F0.wireOp",EDGE,"E624"),sQuery(id+"F0.wireOp",EDGE,"E625"),sQuery(id+"F0.wireOp",EDGE,"E626"),sQuery(id+"F0.wireOp",EDGE,"E627"),sQuery(id+"F0.wireOp",EDGE,"E628"),sQuery(id+"F0.wireOp",EDGE,"E629"),sQuery(id+"F0.wireOp",EDGE,"E630"),sQuery(id+"F0.wireOp",EDGE,"E631"),sQuery(id+"F0.wireOp",EDGE,"E632"),sQuery(id+"F0.wireOp",EDGE,"E633"),sQuery(id+"F0.wireOp",EDGE,"E634"),sQuery(id+"F0.wireOp",EDGE,"E635"),sQuery(id+"F0.wireOp",EDGE,"E636"),sQuery(id+"F0.wireOp",EDGE,"E637"),sQuery(id+"F0.wireOp",EDGE,"E638"),sQuery(id+"F0.wireOp",EDGE,"E639"),sQuery(id+"F0.wireOp",EDGE,"E640"),sQuery(id+"F0.wireOp",EDGE,"E641"),sQuery(id+"F0.wireOp",EDGE,"E642"),sQuery(id+"F0.wireOp",EDGE,"E643"),sQuery(id+"F0.wireOp",EDGE,"E644"),sQuery(id+"F0.wireOp",EDGE,"E645"),sQuery(id+"F0.wireOp",EDGE,"E646"),sQuery(id+"F0.wireOp",EDGE,"E647"),sQuery(id+"F0.wireOp",EDGE,"E648"),sQuery(id+"F0.wireOp",EDGE,"E649"),sQuery(id+"F0.wireOp",EDGE,"E650"),sQuery(id+"F0.wireOp",EDGE,"E651"),sQuery(id+"F0.wireOp",EDGE,"E652"),sQuery(id+"F0.wireOp",EDGE,"E653"),sQuery(id+"F0.wireOp",EDGE,"E654"),sQuery(id+"F0.wireOp",EDGE,"E655"),sQuery(id+"F0.wireOp",EDGE,"E656"),sQuery(id+"F0.wireOp",EDGE,"E657"),sQuery(id+"F0.wireOp",EDGE,"E658"),sQuery(id+"F0.wireOp",EDGE,"E659"),sQuery(id+"F0.wireOp",EDGE,"E660"),sQuery(id+"F0.wireOp",EDGE,"E661"),sQuery(id+"F0.wireOp",EDGE,"E662"),sQuery(id+"F0.wireOp",EDGE,"E663"),sQuery(id+"F0.wireOp",EDGE,"E664"),sQuery(id+"F0.wireOp",EDGE,"E665"),sQuery(id+"F0.wireOp",EDGE,"E666"),sQuery(id+"F0.wireOp",EDGE,"E667"),sQuery(id+"F0.wireOp",EDGE,"E668"),sQuery(id+"F0.wireOp",EDGE,"E669"),sQuery(id+"F0.wireOp",EDGE,"E670"),sQuery(id+"F0.wireOp",EDGE,"E671"),sQuery(id+"F0.wireOp",EDGE,"E672"),sQuery(id+"F0.wireOp",EDGE,"E673"),sQuery(id+"F0.wireOp",EDGE,"E674"),sQuery(id+"F0.wireOp",EDGE,"E675"),sQuery(id+"F0.wireOp",EDGE,"E676"),sQuery(id+"F0.wireOp",EDGE,"E677"),sQuery(id+"F0.wireOp",EDGE,"E678"),sQuery(id+"F0.wireOp",EDGE,"E679"),sQuery(id+"F0.wireOp",EDGE,"E680"),sQuery(id+"F0.wireOp",EDGE,"E681"),sQuery(id+"F0.wireOp",EDGE,"E682"),sQuery(id+"F0.wireOp",EDGE,"E683"),sQuery(id+"F0.wireOp",EDGE,"E684"),sQuery(id+"F0.wireOp",EDGE,"E685"),sQuery(id+"F0.wireOp",EDGE,"E686"),sQuery(id+"F0.wireOp",EDGE,"E687"),sQuery(id+"F0.wireOp",EDGE,"E688"),sQuery(id+"F0.wireOp",EDGE,"E689"),sQuery(id+"F0.wireOp",EDGE,"E690"),sQuery(id+"F0.wireOp",EDGE,"E691"),sQuery(id+"F0.wireOp",EDGE,"E692"),sQuery(id+"F0.wireOp",EDGE,"E693"),sQuery(id+"F0.wireOp",EDGE,"E694"),sQuery(id+"F0.wireOp",EDGE,"E695"),sQuery(id+"F0.wireOp",EDGE,"E696"),sQuery(id+"F0.wireOp",EDGE,"E697"),sQuery(id+"F0.wireOp",EDGE,"E698"),sQuery(id+"F0.wireOp",EDGE,"E699"),sQuery(id+"F0.wireOp",EDGE,"E700"),sQuery(id+"F0.wireOp",EDGE,"E701"),sQuery(id+"F0.wireOp",EDGE,"E702"),sQuery(id+"F0.wireOp",EDGE,"E703"),sQuery(id+"F0.wireOp",EDGE,"E704"),sQuery(id+"F0.wireOp",EDGE,"E705"),sQuery(id+"F0.wireOp",EDGE,"E706"),sQuery(id+"F0.wireOp",EDGE,"E707"),sQuery(id+"F0.wireOp",EDGE,"E708"),sQuery(id+"F0.wireOp",EDGE,"E709"),sQuery(id+"F0.wireOp",EDGE,"E710"),sQuery(id+"F0.wireOp",EDGE,"E711"),sQuery(id+"F0.wireOp",EDGE,"E712"),sQuery(id+"F0.wireOp",EDGE,"E713"),sQuery(id+"F0.wireOp",EDGE,"E714"),sQuery(id+"F0.wireOp",EDGE,"E715"),sQuery(id+"F0.wireOp",EDGE,"E716"),sQuery(id+"F0.wireOp",EDGE,"E717"),sQuery(id+"F0.wireOp",EDGE,"E718"),sQuery(id+"F0.wireOp",EDGE,"E719"),sQuery(id+"F0.wireOp",EDGE,"E720"),sQuery(id+"F0.wireOp",EDGE,"E721"),sQuery(id+"F0.wireOp",EDGE,"E722"),sQuery(id+"F0.wireOp",EDGE,"E723"),sQuery(id+"F0.wireOp",EDGE,"E724"),sQuery(id+"F0.wireOp",EDGE,"E725"),sQuery(id+"F0.wireOp",EDGE,"E726"),sQuery(id+"F0.wireOp",EDGE,"E727"),sQuery(id+"F0.wireOp",EDGE,"E728"),sQuery(id+"F0.wireOp",EDGE,"E729"),sQuery(id+"F0.wireOp",EDGE,"E730"),sQuery(id+"F0.wireOp",EDGE,"E731"),sQuery(id+"F0.wireOp",EDGE,"E732"),sQuery(id+"F0.wireOp",EDGE,"E733"),sQuery(id+"F0.wireOp",EDGE,"E734"),sQuery(id+"F0.wireOp",EDGE,"E735"),sQuery(id+"F0.wireOp",EDGE,"E736"),sQuery(id+"F0.wireOp",EDGE,"E737"),sQuery(id+"F0.wireOp",EDGE,"E738"),sQuery(id+"F0.wireOp",EDGE,"E739"),sQuery(id+"F0.wireOp",EDGE,"E740"),sQuery(id+"F0.wireOp",EDGE,"E741"),sQuery(id+"F0.wireOp",EDGE,"E742"),sQuery(id+"F0.wireOp",EDGE,"E743"),sQuery(id+"F0.wireOp",EDGE,"E744"),sQuery(id+"F0.wireOp",EDGE,"E745"),sQuery(id+"F0.wireOp",EDGE,"E746"),sQuery(id+"F0.wireOp",EDGE,"E747"),sQuery(id+"F0.wireOp",EDGE,"E748"),sQuery(id+"F0.wireOp",EDGE,"E749"),sQuery(id+"F0.wireOp",EDGE,"E750"),sQuery(id+"F0.wireOp",EDGE,"E751"),sQuery(id+"F0.wireOp",EDGE,"E752"),sQuery(id+"F0.wireOp",EDGE,"E753"),sQuery(id+"F0.wireOp",EDGE,"E754"),sQuery(id+"F0.wireOp",EDGE,"E755"),sQuery(id+"F0.wireOp",EDGE,"E756"),sQuery(id+"F0.wireOp",EDGE,"E757"),sQuery(id+"F0.wireOp",EDGE,"E758"),sQuery(id+"F0.wireOp",EDGE,"E759"),sQuery(id+"F0.wireOp",EDGE,"E760"),sQuery(id+"F0.wireOp",EDGE,"E761"),sQuery(id+"F0.wireOp",EDGE,"E762"),sQuery(id+"F0.wireOp",EDGE,"E763"),sQuery(id+"F0.wireOp",EDGE,"E764"),sQuery(id+"F0.wireOp",EDGE,"E765"),sQuery(id+"F0.wireOp",EDGE,"E766"),sQuery(id+"F0.wireOp",EDGE,"E767"),sQuery(id+"F0.wireOp",EDGE,"E768"),sQuery(id+"F0.wireOp",EDGE,"E769"),sQuery(id+"F0.wireOp",EDGE,"E770"),sQuery(id+"F0.wireOp",EDGE,"E771"),sQuery(id+"F0.wireOp",EDGE,"E772"),sQuery(id+"F0.wireOp",EDGE,"E773"),sQuery(id+"F0.wireOp",EDGE,"E774"),sQuery(id+"F0.wireOp",EDGE,"E775"),sQuery(id+"F0.wireOp",EDGE,"E776"),sQuery(id+"F0.wireOp",EDGE,"E777"),sQuery(id+"F0.wireOp",EDGE,"E778"),sQuery(id+"F0.wireOp",EDGE,"E779"),sQuery(id+"F0.wireOp",EDGE,"E780"),sQuery(id+"F0.wireOp",EDGE,"E781"),sQuery(id+"F0.wireOp",EDGE,"E782"),sQuery(id+"F0.wireOp",EDGE,"E783"),sQuery(id+"F0.wireOp",EDGE,"E784"),sQuery(id+"F0.wireOp",EDGE,"E785"),sQuery(id+"F0.wireOp",EDGE,"E786"),sQuery(id+"F0.wireOp",EDGE,"E787"),sQuery(id+"F0.wireOp",EDGE,"E788"),sQuery(id+"F0.wireOp",EDGE,"E789"),sQuery(id+"F0.wireOp",EDGE,"E790"),sQuery(id+"F0.wireOp",EDGE,"E791"),sQuery(id+"F0.wireOp",EDGE,"E792"),sQuery(id+"F0.wireOp",EDGE,"E793"),sQuery(id+"F0.wireOp",EDGE,"E794"),sQuery(id+"F0.wireOp",EDGE,"E795"),sQuery(id+"F0.wireOp",EDGE,"E796"),sQuery(id+"F0.wireOp",EDGE,"E797"),sQuery(id+"F0.wireOp",EDGE,"E798"),sQuery(id+"F0.wireOp",EDGE,"E799"),sQuery(id+"F0.wireOp",EDGE,"E800"),sQuery(id+"F0.wireOp",EDGE,"E801"),sQuery(id+"F0.wireOp",EDGE,"E802"),sQuery(id+"F0.wireOp",EDGE,"E803"),sQuery(id+"F0.wireOp",EDGE,"E804"),sQuery(id+"F0.wireOp",EDGE,"E805"),sQuery(id+"F0.wireOp",EDGE,"E806"),sQuery(id+"F0.wireOp",EDGE,"E807"),sQuery(id+"F0.wireOp",EDGE,"E808"),sQuery(id+"F0.wireOp",EDGE,"E809"),sQuery(id+"F0.wireOp",EDGE,"E810"),sQuery(id+"F0.wireOp",EDGE,"E811"),sQuery(id+"F0.wireOp",EDGE,"E812"),sQuery(id+"F0.wireOp",EDGE,"E813"),subQ4,sQuery(id+"F0.wireOp",EDGE,"E815"),sQuery(id+"F0.wireOp",EDGE,"E816")])],"isStart":true}),makeQuery(id+"F3.opExtrude","CAP_FACE",FACE,{"disambiguationData":[OSD([subQ8,subQ7,subQ6,sQuery(id+"F2.wireOp",EDGE,"E820"),sQuery(id+"F2.wireOp",EDGE,"E825")])],"isStart":false}),makeQuery(id+"F3.opExtrude","CAP_FACE",FACE,{"disambiguationData":[OSD([subQ5,subQ4,sQuery(id+"F2.wireOp",EDGE,"E821"),sQuery(id+"F2.wireOp",EDGE,"E824")])],"isStart":false}),makeQuery(id+"F3.opExtrude","CAP_FACE",FACE,{"disambiguationData":[OSD([subQ3,subQ2,subQ1,subQ0,sQuery(id+"F2.wireOp",EDGE,"E822"),sQuery(id+"F2.wireOp",EDGE,"E823")])],"isStart":false})]});}
            fillet(context, id + "F4", {"entities" : qUnion([Q0, Q1]), "radius" : 0.5 * mm, "tangentPropagation" : true, "allowEdgeOverflow" : false});
        }
        {
            var Q0;
            {var subQ0=makeQuery(id+"F1.opExtrude","CAP_EDGE",EDGE,{"disambiguationData":[OSD([sQuery(id+"F0.wireOp",EDGE,"E268")])],"isStart":false});Q0=makeQuery(id+"F2.imprint","IMPRINT",FACE,{"disambiguationData":[TD([[makeQuery(id+"F2.imprint","IMPRINT",EDGE,{"derivedFrom":subQ0}),1.0]])]});}
            var Q1;
            {var subQ1=makeQuery(id+"F1.opExtrude","CAP_EDGE",EDGE,{"disambiguationData":[OSD([sQuery(id+"F0.wireOp",EDGE,"E546")])],"isStart":false});Q1=makeQuery(id+"F2.imprint","IMPRINT",FACE,{"disambiguationData":[TD([[makeQuery(id+"F2.imprint","IMPRINT",EDGE,{"derivedFrom":subQ1}),1.0]])]});}
            var Q2;
            {var subQ5=makeQuery(id+"F1.opExtrude","CAP_EDGE",EDGE,{"disambiguationData":[OSD([sQuery(id+"F0.wireOp",EDGE,"E816")])],"isStart":false});Q2=makeQuery(id+"F2.imprint","IMPRINT",FACE,{"disambiguationData":[TD([[makeQuery(id+"F2.imprint","IMPRINT",EDGE,{"derivedFrom":subQ5}),1.0]])]});}
            extrude(context, id + "F5", {"entities" : qUnion([Q0, Q1, Q2]), "operationType" : NewBodyOperationType.REMOVE, "oppositeDirection" : true, "depth" : 25 * mm});
        }
    });
